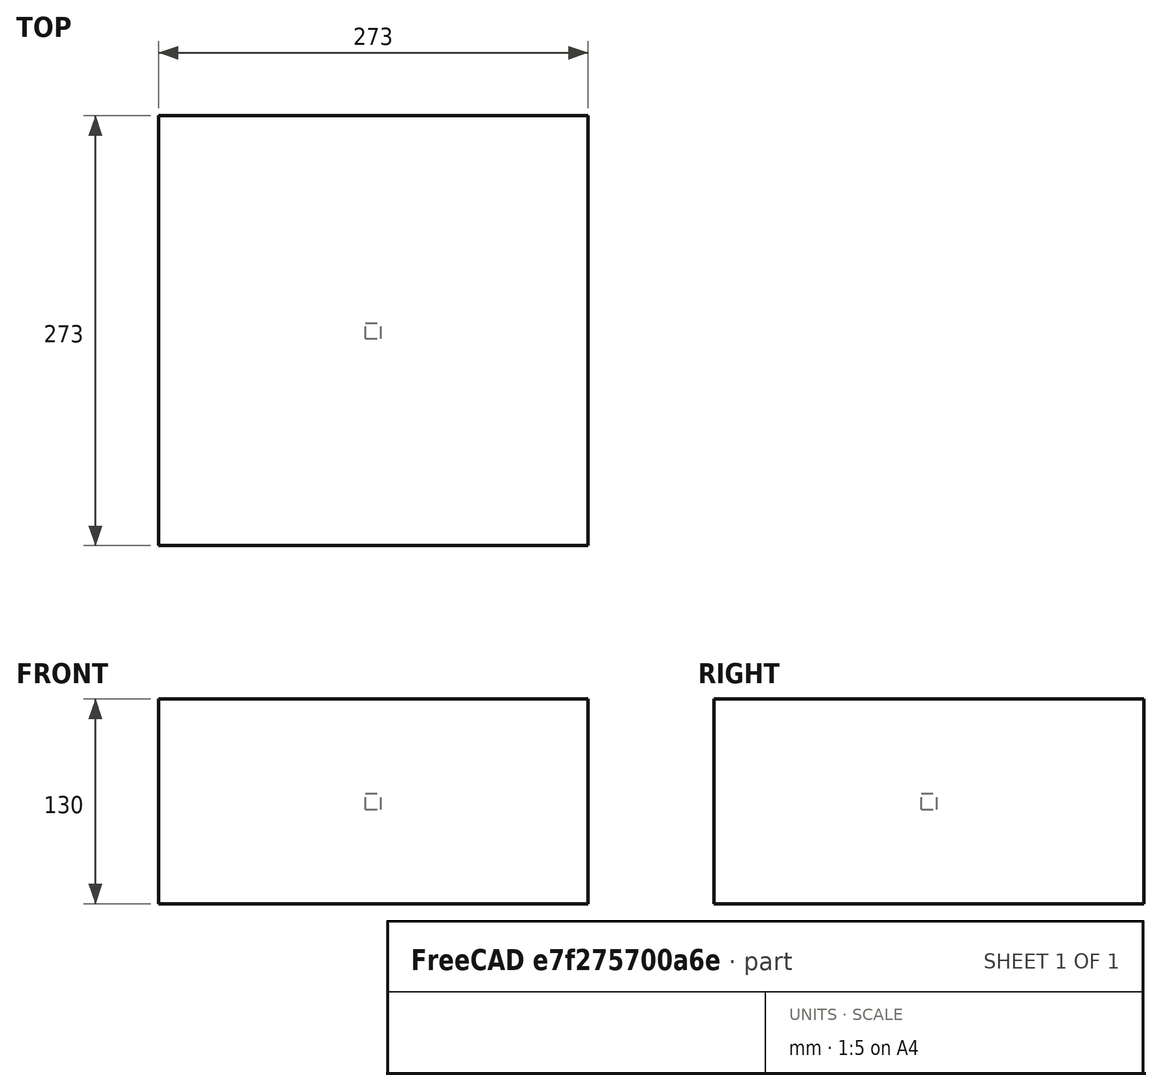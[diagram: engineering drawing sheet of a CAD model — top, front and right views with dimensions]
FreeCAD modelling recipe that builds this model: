
FCSTD DOCUMENT  (FreeCAD 0.20RUnknown)
Label: polarArray-3
License: All rights reserved
LicenseURL: http://en.wikipedia.org/wiki/All_rights_reserved
objects: App::DocumentObjectGroupPython×1251, Part::FeaturePython×3, App::Part×3
note: 2 computed .brp shape members not serialized (recipe doc carries the construction recipe); baked Part::Feature solids carry a one-line shape summary decoded from their .brp

FEATURE [App::DocumentObjectGroupPython] HALFPI  # scripted group (container) (typed FeaturePython)
  name = HALFPI
  value = pi/2.
FEATURE [App::DocumentObjectGroupPython] PI  # scripted group (container) (typed FeaturePython)
  name = PI
  value = 1.*pi
FEATURE [App::DocumentObjectGroupPython] TWOPI  # scripted group (container) (typed FeaturePython)
  name = TWOPI
  value = 2.*pi
FEATURE [App::DocumentObjectGroupPython] Constants  # scripted group (container) (typed FeaturePython)
  Group = -> [HALFPI,PI,TWOPI]
FEATURE [App::DocumentObjectGroupPython] Variables  # scripted group (container) (typed FeaturePython)
FEATURE [App::DocumentObjectGroupPython] Quantities  # scripted group (container) (typed FeaturePython)
FEATURE [App::DocumentObjectGroupPython] Isotopes  # scripted group (container) (typed FeaturePython)
FEATURE [App::DocumentObjectGroupPython] Elements  # scripted group (container) (typed FeaturePython)
FEATURE [App::DocumentObjectGroupPython] Matrix  # scripted group (container) (typed FeaturePython)
FEATURE [App::DocumentObjectGroupPython] Surfaces  # scripted group (container) (typed FeaturePython)
FEATURE [App::DocumentObjectGroupPython] Opticals  # scripted group (container) (typed FeaturePython)
  Group = -> [Matrix,Surfaces]
FEATURE [App::DocumentObjectGroupPython] G4Isotopes  # scripted group (container) (typed FeaturePython)
FEATURE [App::DocumentObjectGroupPython] H_element  # scripted group (container) (typed FeaturePython)
  Z = 1
  atom_value = 1.008
  formula = H
  name = H_element
FEATURE [App::DocumentObjectGroupPython] He_element  # scripted group (container) (typed FeaturePython)
  Z = 2
  atom_value = 4.0026
  formula = He
  name = He_element
FEATURE [App::DocumentObjectGroupPython] Li_element  # scripted group (container) (typed FeaturePython)
  Z = 3
  atom_value = 6.94
  formula = Li
  name = Li_element
FEATURE [App::DocumentObjectGroupPython] Be_element  # scripted group (container) (typed FeaturePython)
  Z = 4
  atom_value = 9.01218
  formula = Be
  name = Be_element
FEATURE [App::DocumentObjectGroupPython] B_element  # scripted group (container) (typed FeaturePython)
  Z = 5
  atom_value = 10.81
  formula = B
  name = B_element
FEATURE [App::DocumentObjectGroupPython] C_element  # scripted group (container) (typed FeaturePython)
  Z = 6
  atom_value = 12.011
  formula = C
  name = C_element
FEATURE [App::DocumentObjectGroupPython] N_element  # scripted group (container) (typed FeaturePython)
  Z = 7
  atom_value = 14.007
  formula = N
  name = N_element
FEATURE [App::DocumentObjectGroupPython] O_element  # scripted group (container) (typed FeaturePython)
  Z = 8
  atom_value = 15.999
  formula = O
  name = O_element
FEATURE [App::DocumentObjectGroupPython] F_element  # scripted group (container) (typed FeaturePython)
  Z = 9
  atom_value = 18.9984
  formula = F
  name = F_element
FEATURE [App::DocumentObjectGroupPython] Ne_element  # scripted group (container) (typed FeaturePython)
  Z = 10
  atom_value = 20.1797
  formula = Ne
  name = Ne_element
FEATURE [App::DocumentObjectGroupPython] Na_element  # scripted group (container) (typed FeaturePython)
  Z = 11
  atom_value = 22.9898
  formula = Na
  name = Na_element
FEATURE [App::DocumentObjectGroupPython] Mg_element  # scripted group (container) (typed FeaturePython)
  Z = 12
  atom_value = 24.305
  formula = Mg
  name = Mg_element
FEATURE [App::DocumentObjectGroupPython] Al_element  # scripted group (container) (typed FeaturePython)
  Z = 13
  atom_value = 26.9815
  formula = Al
  name = Al_element
FEATURE [App::DocumentObjectGroupPython] Si_element  # scripted group (container) (typed FeaturePython)
  Z = 14
  atom_value = 28.085
  formula = Si
  name = Si_element
FEATURE [App::DocumentObjectGroupPython] P_element  # scripted group (container) (typed FeaturePython)
  Z = 15
  atom_value = 30.9738
  formula = P
  name = P_element
FEATURE [App::DocumentObjectGroupPython] S_element  # scripted group (container) (typed FeaturePython)
  Z = 16
  atom_value = 32.06
  formula = S
  name = S_element
FEATURE [App::DocumentObjectGroupPython] Cl_element  # scripted group (container) (typed FeaturePython)
  Z = 17
  atom_value = 35.45
  formula = Cl
  name = Cl_element
FEATURE [App::DocumentObjectGroupPython] Ar_element  # scripted group (container) (typed FeaturePython)
  Z = 18
  atom_value = 39.95
  formula = Ar
  name = Ar_element
FEATURE [App::DocumentObjectGroupPython] K_element  # scripted group (container) (typed FeaturePython)
  Z = 19
  atom_value = 39.0983
  formula = K
  name = K_element
FEATURE [App::DocumentObjectGroupPython] Ca_element  # scripted group (container) (typed FeaturePython)
  Z = 20
  atom_value = 40.078
  formula = Ca
  name = Ca_element
FEATURE [App::DocumentObjectGroupPython] Sc_element  # scripted group (container) (typed FeaturePython)
  Z = 21
  atom_value = 44.9559
  formula = Sc
  name = Sc_element
FEATURE [App::DocumentObjectGroupPython] Ti_element  # scripted group (container) (typed FeaturePython)
  Z = 22
  atom_value = 47.867
  formula = Ti
  name = Ti_element
FEATURE [App::DocumentObjectGroupPython] V_element  # scripted group (container) (typed FeaturePython)
  Z = 23
  atom_value = 50.9415
  formula = V
  name = V_element
FEATURE [App::DocumentObjectGroupPython] Cr_element  # scripted group (container) (typed FeaturePython)
  Z = 24
  atom_value = 51.9961
  formula = Cr
  name = Cr_element
FEATURE [App::DocumentObjectGroupPython] Mn_element  # scripted group (container) (typed FeaturePython)
  Z = 25
  atom_value = 54.938
  formula = Mn
  name = Mn_element
FEATURE [App::DocumentObjectGroupPython] Fe_element  # scripted group (container) (typed FeaturePython)
  Z = 26
  atom_value = 55.845
  formula = Fe
  name = Fe_element
FEATURE [App::DocumentObjectGroupPython] Co_element  # scripted group (container) (typed FeaturePython)
  Z = 27
  atom_value = 58.9332
  formula = Co
  name = Co_element
FEATURE [App::DocumentObjectGroupPython] Ni_element  # scripted group (container) (typed FeaturePython)
  Z = 28
  atom_value = 58.6934
  formula = Ni
  name = Ni_element
FEATURE [App::DocumentObjectGroupPython] Cu_element  # scripted group (container) (typed FeaturePython)
  Z = 29
  atom_value = 63.546
  formula = Cu
  name = Cu_element
FEATURE [App::DocumentObjectGroupPython] Zn_element  # scripted group (container) (typed FeaturePython)
  Z = 30
  atom_value = 65.38
  formula = Zn
  name = Zn_element
FEATURE [App::DocumentObjectGroupPython] Ga_element  # scripted group (container) (typed FeaturePython)
  Z = 31
  atom_value = 69.723
  formula = Ga
  name = Ga_element
FEATURE [App::DocumentObjectGroupPython] Ge_element  # scripted group (container) (typed FeaturePython)
  Z = 32
  atom_value = 72.63
  formula = Ge
  name = Ge_element
FEATURE [App::DocumentObjectGroupPython] As_element  # scripted group (container) (typed FeaturePython)
  Z = 33
  atom_value = 74.9216
  formula = As
  name = As_element
FEATURE [App::DocumentObjectGroupPython] Se_element  # scripted group (container) (typed FeaturePython)
  Z = 34
  atom_value = 78.971
  formula = Se
  name = Se_element
FEATURE [App::DocumentObjectGroupPython] Br_element  # scripted group (container) (typed FeaturePython)
  Z = 35
  atom_value = 79.904
  formula = Br
  name = Br_element
FEATURE [App::DocumentObjectGroupPython] Kr_element  # scripted group (container) (typed FeaturePython)
  Z = 36
  atom_value = 83.798
  formula = Kr
  name = Kr_element
FEATURE [App::DocumentObjectGroupPython] Rb_element  # scripted group (container) (typed FeaturePython)
  Z = 37
  atom_value = 85.4678
  formula = Rb
  name = Rb_element
FEATURE [App::DocumentObjectGroupPython] Sr_element  # scripted group (container) (typed FeaturePython)
  Z = 38
  atom_value = 87.62
  formula = Sr
  name = Sr_element
FEATURE [App::DocumentObjectGroupPython] Y_element  # scripted group (container) (typed FeaturePython)
  Z = 39
  atom_value = 88.9058
  formula = Y
  name = Y_element
FEATURE [App::DocumentObjectGroupPython] Zr_element  # scripted group (container) (typed FeaturePython)
  Z = 40
  atom_value = 91.224
  formula = Zr
  name = Zr_element
FEATURE [App::DocumentObjectGroupPython] Nb_element  # scripted group (container) (typed FeaturePython)
  Z = 41
  atom_value = 92.9064
  formula = Nb
  name = Nb_element
FEATURE [App::DocumentObjectGroupPython] Mo_element  # scripted group (container) (typed FeaturePython)
  Z = 42
  atom_value = 95.95
  formula = Mo
  name = Mo_element
FEATURE [App::DocumentObjectGroupPython] Tc_element  # scripted group (container) (typed FeaturePython)
  Z = 43
  atom_value = 97
  formula = Tc
  name = Tc_element
FEATURE [App::DocumentObjectGroupPython] Ru_element  # scripted group (container) (typed FeaturePython)
  Z = 44
  atom_value = 101.07
  formula = Ru
  name = Ru_element
FEATURE [App::DocumentObjectGroupPython] Rh_element  # scripted group (container) (typed FeaturePython)
  Z = 45
  atom_value = 102.905
  formula = Rh
  name = Rh_element
FEATURE [App::DocumentObjectGroupPython] Pd_element  # scripted group (container) (typed FeaturePython)
  Z = 46
  atom_value = 106.42
  formula = Pd
  name = Pd_element
FEATURE [App::DocumentObjectGroupPython] Ag_element  # scripted group (container) (typed FeaturePython)
  Z = 47
  atom_value = 107.868
  formula = Ag
  name = Ag_element
FEATURE [App::DocumentObjectGroupPython] Cd_element  # scripted group (container) (typed FeaturePython)
  Z = 48
  atom_value = 112.414
  formula = Cd
  name = Cd_element
FEATURE [App::DocumentObjectGroupPython] In_element  # scripted group (container) (typed FeaturePython)
  Z = 49
  atom_value = 114.818
  formula = In
  name = In_element
FEATURE [App::DocumentObjectGroupPython] Sn_element  # scripted group (container) (typed FeaturePython)
  Z = 50
  atom_value = 118.71
  formula = Sn
  name = Sn_element
FEATURE [App::DocumentObjectGroupPython] Sb_element  # scripted group (container) (typed FeaturePython)
  Z = 51
  atom_value = 121.76
  formula = Sb
  name = Sb_element
FEATURE [App::DocumentObjectGroupPython] Te_element  # scripted group (container) (typed FeaturePython)
  Z = 52
  atom_value = 127.6
  formula = Te
  name = Te_element
FEATURE [App::DocumentObjectGroupPython] I_element  # scripted group (container) (typed FeaturePython)
  Z = 53
  atom_value = 126.904
  formula = I
  name = I_element
FEATURE [App::DocumentObjectGroupPython] Xe_element  # scripted group (container) (typed FeaturePython)
  Z = 54
  atom_value = 131.293
  formula = Xe
  name = Xe_element
FEATURE [App::DocumentObjectGroupPython] Cs_element  # scripted group (container) (typed FeaturePython)
  Z = 55
  atom_value = 132.905
  formula = Cs
  name = Cs_element
FEATURE [App::DocumentObjectGroupPython] Ba_element  # scripted group (container) (typed FeaturePython)
  Z = 56
  atom_value = 137.327
  formula = Ba
  name = Ba_element
FEATURE [App::DocumentObjectGroupPython] La_element  # scripted group (container) (typed FeaturePython)
  Z = 57
  atom_value = 138.905
  formula = La
  name = La_element
FEATURE [App::DocumentObjectGroupPython] Ce_element  # scripted group (container) (typed FeaturePython)
  Z = 58
  atom_value = 140.116
  formula = Ce
  name = Ce_element
FEATURE [App::DocumentObjectGroupPython] Pr_element  # scripted group (container) (typed FeaturePython)
  Z = 59
  atom_value = 140.908
  formula = Pr
  name = Pr_element
FEATURE [App::DocumentObjectGroupPython] Nd_element  # scripted group (container) (typed FeaturePython)
  Z = 60
  atom_value = 144.242
  formula = Nd
  name = Nd_element
FEATURE [App::DocumentObjectGroupPython] Pm_element  # scripted group (container) (typed FeaturePython)
  Z = 61
  atom_value = 145
  formula = Pm
  name = Pm_element
FEATURE [App::DocumentObjectGroupPython] Sm_element  # scripted group (container) (typed FeaturePython)
  Z = 62
  atom_value = 150.36
  formula = Sm
  name = Sm_element
FEATURE [App::DocumentObjectGroupPython] Eu_element  # scripted group (container) (typed FeaturePython)
  Z = 63
  atom_value = 151.964
  formula = Eu
  name = Eu_element
FEATURE [App::DocumentObjectGroupPython] Gd_element  # scripted group (container) (typed FeaturePython)
  Z = 64
  atom_value = 157.25
  formula = Gd
  name = Gd_element
FEATURE [App::DocumentObjectGroupPython] Tb_element  # scripted group (container) (typed FeaturePython)
  Z = 65
  atom_value = 158.925
  formula = Tb
  name = Tb_element
FEATURE [App::DocumentObjectGroupPython] Dy_element  # scripted group (container) (typed FeaturePython)
  Z = 66
  atom_value = 162.5
  formula = Dy
  name = Dy_element
FEATURE [App::DocumentObjectGroupPython] Ho_element  # scripted group (container) (typed FeaturePython)
  Z = 67
  atom_value = 164.93
  formula = Ho
  name = Ho_element
FEATURE [App::DocumentObjectGroupPython] Er_element  # scripted group (container) (typed FeaturePython)
  Z = 68
  atom_value = 167.259
  formula = Er
  name = Er_element
FEATURE [App::DocumentObjectGroupPython] Tm_element  # scripted group (container) (typed FeaturePython)
  Z = 69
  atom_value = 168.934
  formula = Tm
  name = Tm_element
FEATURE [App::DocumentObjectGroupPython] Yb_element  # scripted group (container) (typed FeaturePython)
  Z = 70
  atom_value = 173.045
  formula = Yb
  name = Yb_element
FEATURE [App::DocumentObjectGroupPython] Lu_element  # scripted group (container) (typed FeaturePython)
  Z = 71
  atom_value = 174.967
  formula = Lu
  name = Lu_element
FEATURE [App::DocumentObjectGroupPython] Hf_element  # scripted group (container) (typed FeaturePython)
  Z = 72
  atom_value = 178.49
  formula = Hf
  name = Hf_element
FEATURE [App::DocumentObjectGroupPython] Ta_element  # scripted group (container) (typed FeaturePython)
  Z = 73
  atom_value = 180.948
  formula = Ta
  name = Ta_element
FEATURE [App::DocumentObjectGroupPython] W_element  # scripted group (container) (typed FeaturePython)
  Z = 74
  atom_value = 183.84
  formula = W
  name = W_element
FEATURE [App::DocumentObjectGroupPython] Re_element  # scripted group (container) (typed FeaturePython)
  Z = 75
  atom_value = 186.207
  formula = Re
  name = Re_element
FEATURE [App::DocumentObjectGroupPython] Os_element  # scripted group (container) (typed FeaturePython)
  Z = 76
  atom_value = 190.23
  formula = Os
  name = Os_element
FEATURE [App::DocumentObjectGroupPython] Ir_element  # scripted group (container) (typed FeaturePython)
  Z = 77
  atom_value = 192.217
  formula = Ir
  name = Ir_element
FEATURE [App::DocumentObjectGroupPython] Pt_element  # scripted group (container) (typed FeaturePython)
  Z = 78
  atom_value = 195.084
  formula = Pt
  name = Pt_element
FEATURE [App::DocumentObjectGroupPython] Au_element  # scripted group (container) (typed FeaturePython)
  Z = 79
  atom_value = 196.967
  formula = Au
  name = Au_element
FEATURE [App::DocumentObjectGroupPython] Hg_element  # scripted group (container) (typed FeaturePython)
  Z = 80
  atom_value = 200.592
  formula = Hg
  name = Hg_element
FEATURE [App::DocumentObjectGroupPython] Tl_element  # scripted group (container) (typed FeaturePython)
  Z = 81
  atom_value = 204.38
  formula = Tl
  name = Tl_element
FEATURE [App::DocumentObjectGroupPython] Pb_element  # scripted group (container) (typed FeaturePython)
  Z = 82
  atom_value = 207.2
  formula = Pb
  name = Pb_element
FEATURE [App::DocumentObjectGroupPython] Bi_element  # scripted group (container) (typed FeaturePython)
  Z = 83
  atom_value = 208.98
  formula = Bi
  name = Bi_element
FEATURE [App::DocumentObjectGroupPython] Po_element  # scripted group (container) (typed FeaturePython)
  Z = 84
  atom_value = 209
  formula = Po
  name = Po_element
FEATURE [App::DocumentObjectGroupPython] At_element  # scripted group (container) (typed FeaturePython)
  Z = 85
  atom_value = 210
  formula = At
  name = At_element
FEATURE [App::DocumentObjectGroupPython] Rn_element  # scripted group (container) (typed FeaturePython)
  Z = 86
  atom_value = 222
  formula = Rn
  name = Rn_element
FEATURE [App::DocumentObjectGroupPython] Fr_element  # scripted group (container) (typed FeaturePython)
  Z = 87
  atom_value = 223
  formula = Fr
  name = Fr_element
FEATURE [App::DocumentObjectGroupPython] Ra_element  # scripted group (container) (typed FeaturePython)
  Z = 88
  atom_value = 226
  formula = Ra
  name = Ra_element
FEATURE [App::DocumentObjectGroupPython] Ac_element  # scripted group (container) (typed FeaturePython)
  Z = 89
  atom_value = 227
  formula = Ac
  name = Ac_element
FEATURE [App::DocumentObjectGroupPython] Th_element  # scripted group (container) (typed FeaturePython)
  Z = 90
  atom_value = 232.038
  formula = Th
  name = Th_element
FEATURE [App::DocumentObjectGroupPython] Pa_element  # scripted group (container) (typed FeaturePython)
  Z = 91
  atom_value = 231.036
  formula = Pa
  name = Pa_element
FEATURE [App::DocumentObjectGroupPython] U_element  # scripted group (container) (typed FeaturePython)
  Z = 92
  atom_value = 238.029
  formula = U
  name = U_element
FEATURE [App::DocumentObjectGroupPython] Np_element  # scripted group (container) (typed FeaturePython)
  Z = 93
  atom_value = 237
  formula = Np
  name = Np_element
FEATURE [App::DocumentObjectGroupPython] Pu_element  # scripted group (container) (typed FeaturePython)
  Z = 94
  atom_value = 244
  formula = Pu
  name = Pu_element
FEATURE [App::DocumentObjectGroupPython] Am_element  # scripted group (container) (typed FeaturePython)
  Z = 95
  atom_value = 243
  formula = Am
  name = Am_element
FEATURE [App::DocumentObjectGroupPython] Cm_element  # scripted group (container) (typed FeaturePython)
  Z = 96
  atom_value = 247
  formula = Cm
  name = Cm_element
FEATURE [App::DocumentObjectGroupPython] Bk_element  # scripted group (container) (typed FeaturePython)
  Z = 97
  atom_value = 247
  formula = Bk
  name = Bk_element
FEATURE [App::DocumentObjectGroupPython] Cf_element  # scripted group (container) (typed FeaturePython)
  Z = 98
  atom_value = 251
  formula = Cf
  name = Cf_element
FEATURE [App::DocumentObjectGroupPython] G4Elements  # scripted group (container) (typed FeaturePython)
  Group = -> [H_element,He_element,Li_element,Be_element,B_element,C_element,N_element,O_element,F_element,Ne_element,Na_element,Mg_element,Al_element,Si_element,P_element,S_element,Cl_element,Ar_element,K_element,Ca_element,Sc_element,Ti_element,V_element,Cr_element,Mn_element,Fe_element,Co_element,Ni_element,Cu_element,Zn_element,Ga_element,Ge_element,As_element,Se_element,Br_element,Kr_element,Rb_element,+61 more]
FEATURE [App::DocumentObjectGroupPython] H_element001  label="H_element : 0.101"  # scripted group (container) (typed FeaturePython)
  n = 0.101327
FEATURE [App::DocumentObjectGroupPython] C_element001  label="C_element : 0.775"  # scripted group (container) (typed FeaturePython)
  n = 0.7755
FEATURE [App::DocumentObjectGroupPython] N_element001  label="N_element : 0.035"  # scripted group (container) (typed FeaturePython)
  n = 0.035057
FEATURE [App::DocumentObjectGroupPython] O_element001  label="O_element : 0.052"  # scripted group (container) (typed FeaturePython)
  n = 0.0523159
FEATURE [App::DocumentObjectGroupPython] F_element001  label="F_element : 0.017"  # scripted group (container) (typed FeaturePython)
  n = 0.017422
FEATURE [App::DocumentObjectGroupPython] Ca_element001  label="Ca_element : 0.018"  # scripted group (container) (typed FeaturePython)
  n = 0.018378
FEATURE [App::DocumentObjectGroupPython] G4_A_150_TISSUE  label="G4_A-150_TISSUE"  # scripted group (container) (typed FeaturePython)
  Dunit = g/cm3
  Dvalue = 1.127
  Group = -> [H_element001,C_element001,N_element001,O_element001,F_element001,Ca_element001]
  conduct = 2
  density = 1
  expand = 3
  formula = G4_A-150_TISSUE
  name = G4_A-150_TISSUE
  specific = 4
FEATURE [App::DocumentObjectGroupPython] C_element002  label="C_element : 3"  # scripted group (container) (typed FeaturePython)
  n = 3
  ref = C_element
FEATURE [App::DocumentObjectGroupPython] H_element002  label="H_element : 6"  # scripted group (container) (typed FeaturePython)
  n = 6
  ref = H_element
FEATURE [App::DocumentObjectGroupPython] O_element002  label="O_element : 1"  # scripted group (container) (typed FeaturePython)
  n = 1
  ref = O_element
FEATURE [App::DocumentObjectGroupPython] G4_ACETONE  # scripted group (container) (typed FeaturePython)
  Dunit = g/cm3
  Dvalue = 0.7899
  Group = -> [C_element002,H_element002,O_element002]
  conduct = 2
  density = 1
  expand = 3
  formula = G4_ACETONE
  name = G4_ACETONE
  specific = 4
FEATURE [App::DocumentObjectGroupPython] C_element003  label="C_element : 2"  # scripted group (container) (typed FeaturePython)
  n = 2
  ref = C_element
FEATURE [App::DocumentObjectGroupPython] H_element003  label="H_element : 2"  # scripted group (container) (typed FeaturePython)
  n = 2
  ref = H_element
FEATURE [App::DocumentObjectGroupPython] G4_ACETYLENE  # scripted group (container) (typed FeaturePython)
  Dunit = g/cm3
  Dvalue = 0.0010967
  Group = -> [C_element003,H_element003]
  conduct = 2
  density = 1
  expand = 3
  formula = G4_ACETYLENE
  name = G4_ACETYLENE
  specific = 4
FEATURE [App::DocumentObjectGroupPython] C_element004  label="C_element : 5"  # scripted group (container) (typed FeaturePython)
  n = 5
  ref = C_element
FEATURE [App::DocumentObjectGroupPython] H_element004  label="H_element : 5"  # scripted group (container) (typed FeaturePython)
  n = 5
  ref = H_element
FEATURE [App::DocumentObjectGroupPython] N_element002  label="N_element : 5"  # scripted group (container) (typed FeaturePython)
  n = 5
  ref = N_element
FEATURE [App::DocumentObjectGroupPython] G4_ADENINE  # scripted group (container) (typed FeaturePython)
  Dunit = g/cm3
  Dvalue = 1.6
  Group = -> [C_element004,H_element004,N_element002]
  conduct = 2
  density = 1
  expand = 3
  formula = G4_ADENINE
  name = G4_ADENINE
  specific = 4
FEATURE [App::DocumentObjectGroupPython] H_element005  label="H_element : 0.114"  # scripted group (container) (typed FeaturePython)
  n = 0.114
FEATURE [App::DocumentObjectGroupPython] C_element005  label="C_element : 0.598"  # scripted group (container) (typed FeaturePython)
  n = 0.598
FEATURE [App::DocumentObjectGroupPython] N_element003  label="N_element : 0.007"  # scripted group (container) (typed FeaturePython)
  n = 0.007
FEATURE [App::DocumentObjectGroupPython] O_element003  label="O_element : 0.278"  # scripted group (container) (typed FeaturePython)
  n = 0.278
FEATURE [App::DocumentObjectGroupPython] Na_element001  label="Na_element : 0.001"  # scripted group (container) (typed FeaturePython)
  n = 0.001
FEATURE [App::DocumentObjectGroupPython] S_element001  label="S_element : 0.001"  # scripted group (container) (typed FeaturePython)
  n = 0.001
FEATURE [App::DocumentObjectGroupPython] Cl_element001  label="Cl_element : 0.001"  # scripted group (container) (typed FeaturePython)
  n = 0.001
FEATURE [App::DocumentObjectGroupPython] G4_ADIPOSE_TISSUE_ICRP  # scripted group (container) (typed FeaturePython)
  Dunit = g/cm3
  Dvalue = 0.95
  Group = -> [H_element005,C_element005,N_element003,O_element003,Na_element001,S_element001,Cl_element001]
  conduct = 2
  density = 1
  expand = 3
  formula = G4_ADIPOSE_TISSUE_ICRP
  name = G4_ADIPOSE_TISSUE_ICRP
  specific = 4
FEATURE [App::DocumentObjectGroupPython] C_element006  label="C_element : 0.000"  # scripted group (container) (typed FeaturePython)
  n = 0.000124
FEATURE [App::DocumentObjectGroupPython] N_element004  label="N_element : 0.755"  # scripted group (container) (typed FeaturePython)
  n = 0.755268
FEATURE [App::DocumentObjectGroupPython] O_element004  label="O_element : 0.232"  # scripted group (container) (typed FeaturePython)
  n = 0.231781
FEATURE [App::DocumentObjectGroupPython] Ar_element001  label="Ar_element : 0.013"  # scripted group (container) (typed FeaturePython)
  n = 0.012827
FEATURE [App::DocumentObjectGroupPython] G4_AIR  # scripted group (container) (typed FeaturePython)
  Dunit = g/cm3
  Dvalue = 0.00120479
  Group = -> [C_element006,N_element004,O_element004,Ar_element001]
  conduct = 2
  density = 1
  expand = 3
  formula = G4_AIR
  name = G4_AIR
  specific = 4
FEATURE [App::DocumentObjectGroupPython] C_element007  label="C_element : 006"  # scripted group (container) (typed FeaturePython)
  n = 3
  ref = C_element
FEATURE [App::DocumentObjectGroupPython] H_element006  label="H_element : 7"  # scripted group (container) (typed FeaturePython)
  n = 7
  ref = H_element
FEATURE [App::DocumentObjectGroupPython] N_element005  label="N_element : 1"  # scripted group (container) (typed FeaturePython)
  n = 1
  ref = N_element
FEATURE [App::DocumentObjectGroupPython] O_element005  label="O_element : 2"  # scripted group (container) (typed FeaturePython)
  n = 2
  ref = O_element
FEATURE [App::DocumentObjectGroupPython] G4_ALANINE  # scripted group (container) (typed FeaturePython)
  Dunit = g/cm3
  Dvalue = 1.42
  Group = -> [C_element007,H_element006,N_element005,O_element005]
  conduct = 2
  density = 1
  expand = 3
  formula = G4_ALANINE
  name = G4_ALANINE
  specific = 4
FEATURE [App::DocumentObjectGroupPython] Al_element001  label="Al_element : 2"  # scripted group (container) (typed FeaturePython)
  n = 2
  ref = Al_element
FEATURE [App::DocumentObjectGroupPython] O_element006  label="O_element : 3"  # scripted group (container) (typed FeaturePython)
  n = 3
  ref = O_element
FEATURE [App::DocumentObjectGroupPython] G4_ALUMINUM_OXIDE  # scripted group (container) (typed FeaturePython)
  Dunit = g/cm3
  Dvalue = 3.97
  Group = -> [Al_element001,O_element006]
  conduct = 2
  density = 1
  expand = 3
  formula = G4_ALUMINUM_OXIDE
  name = G4_ALUMINUM_OXIDE
  specific = 4
FEATURE [App::DocumentObjectGroupPython] H_element007  label="H_element : 0.106"  # scripted group (container) (typed FeaturePython)
  n = 0.10593
FEATURE [App::DocumentObjectGroupPython] C_element008  label="C_element : 0.789"  # scripted group (container) (typed FeaturePython)
  n = 0.788974
FEATURE [App::DocumentObjectGroupPython] O_element007  label="O_element : 0.105"  # scripted group (container) (typed FeaturePython)
  n = 0.105096
FEATURE [App::DocumentObjectGroupPython] G4_AMBER  # scripted group (container) (typed FeaturePython)
  Dunit = g/cm3
  Dvalue = 1.1
  Group = -> [H_element007,C_element008,O_element007]
  conduct = 2
  density = 1
  expand = 3
  formula = G4_AMBER
  name = G4_AMBER
  specific = 4
FEATURE [App::DocumentObjectGroupPython] N_element006  label="N_element : 006"  # scripted group (container) (typed FeaturePython)
  n = 1
  ref = N_element
FEATURE [App::DocumentObjectGroupPython] H_element008  label="H_element : 3"  # scripted group (container) (typed FeaturePython)
  n = 3
  ref = H_element
FEATURE [App::DocumentObjectGroupPython] G4_AMMONIA  # scripted group (container) (typed FeaturePython)
  Dunit = g/cm3
  Dvalue = 0.000826019
  Group = -> [N_element006,H_element008]
  conduct = 2
  density = 1
  expand = 3
  formula = G4_AMMONIA
  name = G4_AMMONIA
  specific = 4
FEATURE [App::DocumentObjectGroupPython] C_element009  label="C_element : 6"  # scripted group (container) (typed FeaturePython)
  n = 6
  ref = C_element
FEATURE [App::DocumentObjectGroupPython] H_element009  label="H_element : 008"  # scripted group (container) (typed FeaturePython)
  n = 7
  ref = H_element
FEATURE [App::DocumentObjectGroupPython] N_element007  label="N_element : 007"  # scripted group (container) (typed FeaturePython)
  n = 1
  ref = N_element
FEATURE [App::DocumentObjectGroupPython] G4_ANILINE  # scripted group (container) (typed FeaturePython)
  Dunit = g/cm3
  Dvalue = 1.0235
  Group = -> [C_element009,H_element009,N_element007]
  conduct = 2
  density = 1
  expand = 3
  formula = G4_ANILINE
  name = G4_ANILINE
  specific = 4
FEATURE [App::DocumentObjectGroupPython] C_element010  label="C_element : 14"  # scripted group (container) (typed FeaturePython)
  n = 14
  ref = C_element
FEATURE [App::DocumentObjectGroupPython] H_element010  label="H_element : 10"  # scripted group (container) (typed FeaturePython)
  n = 10
  ref = H_element
FEATURE [App::DocumentObjectGroupPython] G4_ANTHRACENE  # scripted group (container) (typed FeaturePython)
  Dunit = g/cm3
  Dvalue = 1.283
  Group = -> [C_element010,H_element010]
  conduct = 2
  density = 1
  expand = 3
  formula = G4_ANTHRACENE
  name = G4_ANTHRACENE
  specific = 4
FEATURE [App::DocumentObjectGroupPython] H_element011  label="H_element : 0.065"  # scripted group (container) (typed FeaturePython)
  n = 0.0654709
FEATURE [App::DocumentObjectGroupPython] C_element011  label="C_element : 0.537"  # scripted group (container) (typed FeaturePython)
  n = 0.536944
FEATURE [App::DocumentObjectGroupPython] N_element008  label="N_element : 0.021"  # scripted group (container) (typed FeaturePython)
  n = 0.0215
FEATURE [App::DocumentObjectGroupPython] O_element008  label="O_element : 0.032"  # scripted group (container) (typed FeaturePython)
  n = 0.032085
FEATURE [App::DocumentObjectGroupPython] F_element002  label="F_element : 0.167"  # scripted group (container) (typed FeaturePython)
  n = 0.167411
FEATURE [App::DocumentObjectGroupPython] Ca_element002  label="Ca_element : 0.177"  # scripted group (container) (typed FeaturePython)
  n = 0.176589
FEATURE [App::DocumentObjectGroupPython] G4_B_100_BONE  label="G4_B-100_BONE"  # scripted group (container) (typed FeaturePython)
  Dunit = g/cm3
  Dvalue = 1.45
  Group = -> [H_element011,C_element011,N_element008,O_element008,F_element002,Ca_element002]
  conduct = 2
  density = 1
  expand = 3
  formula = G4_B-100_BONE
  name = G4_B-100_BONE
  specific = 4
FEATURE [App::DocumentObjectGroupPython] H_element012  label="H_element : 0.057"  # scripted group (container) (typed FeaturePython)
  n = 0.057441
FEATURE [App::DocumentObjectGroupPython] C_element012  label="C_element : 0.790"  # scripted group (container) (typed FeaturePython)
  n = 0.774591
FEATURE [App::DocumentObjectGroupPython] O_element009  label="O_element : 0.168"  # scripted group (container) (typed FeaturePython)
  n = 0.167968
FEATURE [App::DocumentObjectGroupPython] G4_BAKELITE  # scripted group (container) (typed FeaturePython)
  Dunit = g/cm3
  Dvalue = 1.25
  Group = -> [H_element012,C_element012,O_element009]
  conduct = 2
  density = 1
  expand = 3
  formula = G4_BAKELITE
  name = G4_BAKELITE
  specific = 4
FEATURE [App::DocumentObjectGroupPython] Ba_element001  label="Ba_element : 1"  # scripted group (container) (typed FeaturePython)
  n = 1
  ref = Ba_element
FEATURE [App::DocumentObjectGroupPython] F_element003  label="F_element : 2"  # scripted group (container) (typed FeaturePython)
  n = 2
  ref = F_element
FEATURE [App::DocumentObjectGroupPython] G4_BARIUM_FLUORIDE  # scripted group (container) (typed FeaturePython)
  Dunit = g/cm3
  Dvalue = 4.89
  Group = -> [Ba_element001,F_element003]
  conduct = 2
  density = 1
  expand = 3
  formula = G4_BARIUM_FLUORIDE
  name = G4_BARIUM_FLUORIDE
  specific = 4
FEATURE [App::DocumentObjectGroupPython] Ba_element002  label="Ba_element : 002"  # scripted group (container) (typed FeaturePython)
  n = 1
  ref = Ba_element
FEATURE [App::DocumentObjectGroupPython] S_element002  label="S_element : 1"  # scripted group (container) (typed FeaturePython)
  n = 1
  ref = S_element
FEATURE [App::DocumentObjectGroupPython] O_element010  label="O_element : 4"  # scripted group (container) (typed FeaturePython)
  n = 4
  ref = O_element
FEATURE [App::DocumentObjectGroupPython] G4_BARIUM_SULFATE  # scripted group (container) (typed FeaturePython)
  Dunit = g/cm3
  Dvalue = 4.5
  Group = -> [Ba_element002,S_element002,O_element010]
  conduct = 2
  density = 1
  expand = 3
  formula = G4_BARIUM_SULFATE
  name = G4_BARIUM_SULFATE
  specific = 4
FEATURE [App::DocumentObjectGroupPython] C_element013  label="C_element : 007"  # scripted group (container) (typed FeaturePython)
  n = 6
  ref = C_element
FEATURE [App::DocumentObjectGroupPython] H_element013  label="H_element : 009"  # scripted group (container) (typed FeaturePython)
  n = 6
  ref = H_element
FEATURE [App::DocumentObjectGroupPython] G4_BENZENE  # scripted group (container) (typed FeaturePython)
  Dunit = g/cm3
  Dvalue = 0.87865
  Group = -> [C_element013,H_element013]
  conduct = 2
  density = 1
  expand = 3
  formula = G4_BENZENE
  name = G4_BENZENE
  specific = 4
FEATURE [App::DocumentObjectGroupPython] Be_element001  label="Be_element : 1"  # scripted group (container) (typed FeaturePython)
  n = 1
  ref = Be_element
FEATURE [App::DocumentObjectGroupPython] O_element011  label="O_element : 005"  # scripted group (container) (typed FeaturePython)
  n = 1
  ref = O_element
FEATURE [App::DocumentObjectGroupPython] G4_BERYLLIUM_OXIDE  # scripted group (container) (typed FeaturePython)
  Dunit = g/cm3
  Dvalue = 3.01
  Group = -> [Be_element001,O_element011]
  conduct = 2
  density = 1
  expand = 3
  formula = G4_BERYLLIUM_OXIDE
  name = G4_BERYLLIUM_OXIDE
  specific = 4
FEATURE [App::DocumentObjectGroupPython] Bi_element001  label="Bi_element : 4"  # scripted group (container) (typed FeaturePython)
  n = 4
  ref = Bi_element
FEATURE [App::DocumentObjectGroupPython] Ge_element001  label="Ge_element : 3"  # scripted group (container) (typed FeaturePython)
  n = 3
  ref = Ge_element
FEATURE [App::DocumentObjectGroupPython] O_element012  label="O_element : 12"  # scripted group (container) (typed FeaturePython)
  n = 12
  ref = O_element
FEATURE [App::DocumentObjectGroupPython] G4_BGO  # scripted group (container) (typed FeaturePython)
  Dunit = g/cm3
  Dvalue = 7.13
  Group = -> [Bi_element001,Ge_element001,O_element012]
  conduct = 2
  density = 1
  expand = 3
  formula = G4_BGO
  name = G4_BGO
  specific = 4
FEATURE [App::DocumentObjectGroupPython] H_element014  label="H_element : 0.102"  # scripted group (container) (typed FeaturePython)
  n = 0.102
FEATURE [App::DocumentObjectGroupPython] C_element014  label="C_element : 0.110"  # scripted group (container) (typed FeaturePython)
  n = 0.11
FEATURE [App::DocumentObjectGroupPython] N_element009  label="N_element : 0.033"  # scripted group (container) (typed FeaturePython)
  n = 0.033
FEATURE [App::DocumentObjectGroupPython] O_element013  label="O_element : 0.745"  # scripted group (container) (typed FeaturePython)
  n = 0.745
FEATURE [App::DocumentObjectGroupPython] Na_element002  label="Na_element : 0.002"  # scripted group (container) (typed FeaturePython)
  n = 0.001
FEATURE [App::DocumentObjectGroupPython] P_element001  label="P_element : 0.001"  # scripted group (container) (typed FeaturePython)
  n = 0.001
FEATURE [App::DocumentObjectGroupPython] S_element003  label="S_element : 0.002"  # scripted group (container) (typed FeaturePython)
  n = 0.002
FEATURE [App::DocumentObjectGroupPython] Cl_element002  label="Cl_element : 0.003"  # scripted group (container) (typed FeaturePython)
  n = 0.003
FEATURE [App::DocumentObjectGroupPython] K_element001  label="K_element : 0.002"  # scripted group (container) (typed FeaturePython)
  n = 0.002
FEATURE [App::DocumentObjectGroupPython] Fe_element001  label="Fe_element : 0.001"  # scripted group (container) (typed FeaturePython)
  n = 0.001
FEATURE [App::DocumentObjectGroupPython] G4_BLOOD_ICRP  # scripted group (container) (typed FeaturePython)
  Dunit = g/cm3
  Dvalue = 1.06
  Group = -> [H_element014,C_element014,N_element009,O_element013,Na_element002,P_element001,S_element003,Cl_element002,K_element001,Fe_element001]
  conduct = 2
  density = 1
  expand = 3
  formula = G4_BLOOD_ICRP
  name = G4_BLOOD_ICRP
  specific = 4
FEATURE [App::DocumentObjectGroupPython] H_element015  label="H_element : 0.064"  # scripted group (container) (typed FeaturePython)
  n = 0.064
FEATURE [App::DocumentObjectGroupPython] C_element015  label="C_element : 0.278"  # scripted group (container) (typed FeaturePython)
  n = 0.278
FEATURE [App::DocumentObjectGroupPython] N_element010  label="N_element : 0.027"  # scripted group (container) (typed FeaturePython)
  n = 0.027
FEATURE [App::DocumentObjectGroupPython] O_element014  label="O_element : 0.410"  # scripted group (container) (typed FeaturePython)
  n = 0.41
FEATURE [App::DocumentObjectGroupPython] Mg_element001  label="Mg_element : 0.002"  # scripted group (container) (typed FeaturePython)
  n = 0.002
FEATURE [App::DocumentObjectGroupPython] P_element002  label="P_element : 0.070"  # scripted group (container) (typed FeaturePython)
  n = 0.07
FEATURE [App::DocumentObjectGroupPython] S_element004  label="S_element : 0.003"  # scripted group (container) (typed FeaturePython)
  n = 0.002
FEATURE [App::DocumentObjectGroupPython] Ca_element003  label="Ca_element : 0.147"  # scripted group (container) (typed FeaturePython)
  n = 0.147
FEATURE [App::DocumentObjectGroupPython] G4_BONE_COMPACT_ICRU  # scripted group (container) (typed FeaturePython)
  Dunit = g/cm3
  Dvalue = 1.85
  Group = -> [H_element015,C_element015,N_element010,O_element014,Mg_element001,P_element002,S_element004,Ca_element003]
  conduct = 2
  density = 1
  expand = 3
  formula = G4_BONE_COMPACT_ICRU
  name = G4_BONE_COMPACT_ICRU
  specific = 4
FEATURE [App::DocumentObjectGroupPython] H_element016  label="H_element : 0.034"  # scripted group (container) (typed FeaturePython)
  n = 0.034
FEATURE [App::DocumentObjectGroupPython] C_element016  label="C_element : 0.155"  # scripted group (container) (typed FeaturePython)
  n = 0.155
FEATURE [App::DocumentObjectGroupPython] N_element011  label="N_element : 0.042"  # scripted group (container) (typed FeaturePython)
  n = 0.042
FEATURE [App::DocumentObjectGroupPython] O_element015  label="O_element : 0.435"  # scripted group (container) (typed FeaturePython)
  n = 0.435
FEATURE [App::DocumentObjectGroupPython] Na_element003  label="Na_element : 0.003"  # scripted group (container) (typed FeaturePython)
  n = 0.001
FEATURE [App::DocumentObjectGroupPython] Mg_element002  label="Mg_element : 0.003"  # scripted group (container) (typed FeaturePython)
  n = 0.002
FEATURE [App::DocumentObjectGroupPython] P_element003  label="P_element : 0.103"  # scripted group (container) (typed FeaturePython)
  n = 0.103
FEATURE [App::DocumentObjectGroupPython] S_element005  label="S_element : 0.004"  # scripted group (container) (typed FeaturePython)
  n = 0.003
FEATURE [App::DocumentObjectGroupPython] Ca_element004  label="Ca_element : 0.225"  # scripted group (container) (typed FeaturePython)
  n = 0.225
FEATURE [App::DocumentObjectGroupPython] G4_BONE_CORTICAL_ICRP  # scripted group (container) (typed FeaturePython)
  Dunit = g/cm3
  Dvalue = 1.92
  Group = -> [H_element016,C_element016,N_element011,O_element015,Na_element003,Mg_element002,P_element003,S_element005,Ca_element004]
  conduct = 2
  density = 1
  expand = 3
  formula = G4_BONE_CORTICAL_ICRP
  name = G4_BONE_CORTICAL_ICRP
  specific = 4
FEATURE [App::DocumentObjectGroupPython] B_element001  label="B_element : 4"  # scripted group (container) (typed FeaturePython)
  n = 4
  ref = B_element
FEATURE [App::DocumentObjectGroupPython] C_element017  label="C_element : 1"  # scripted group (container) (typed FeaturePython)
  n = 1
  ref = C_element
FEATURE [App::DocumentObjectGroupPython] G4_BORON_CARBIDE  # scripted group (container) (typed FeaturePython)
  Dunit = g/cm3
  Dvalue = 2.52
  Group = -> [B_element001,C_element017]
  conduct = 2
  density = 1
  expand = 3
  formula = G4_BORON_CARBIDE
  name = G4_BORON_CARBIDE
  specific = 4
FEATURE [App::DocumentObjectGroupPython] B_element002  label="B_element : 2"  # scripted group (container) (typed FeaturePython)
  n = 2
  ref = B_element
FEATURE [App::DocumentObjectGroupPython] O_element016  label="O_element : 006"  # scripted group (container) (typed FeaturePython)
  n = 3
  ref = O_element
FEATURE [App::DocumentObjectGroupPython] G4_BORON_OXIDE  # scripted group (container) (typed FeaturePython)
  Dunit = g/cm3
  Dvalue = 1.812
  Group = -> [B_element002,O_element016]
  conduct = 2
  density = 1
  expand = 3
  formula = G4_BORON_OXIDE
  name = G4_BORON_OXIDE
  specific = 4
FEATURE [App::DocumentObjectGroupPython] H_element017  label="H_element : 0.107"  # scripted group (container) (typed FeaturePython)
  n = 0.107
FEATURE [App::DocumentObjectGroupPython] C_element018  label="C_element : 0.145"  # scripted group (container) (typed FeaturePython)
  n = 0.145
FEATURE [App::DocumentObjectGroupPython] N_element012  label="N_element : 0.022"  # scripted group (container) (typed FeaturePython)
  n = 0.022
FEATURE [App::DocumentObjectGroupPython] O_element017  label="O_element : 0.712"  # scripted group (container) (typed FeaturePython)
  n = 0.712
FEATURE [App::DocumentObjectGroupPython] Na_element004  label="Na_element : 0.004"  # scripted group (container) (typed FeaturePython)
  n = 0.002
FEATURE [App::DocumentObjectGroupPython] P_element004  label="P_element : 0.004"  # scripted group (container) (typed FeaturePython)
  n = 0.004
FEATURE [App::DocumentObjectGroupPython] S_element006  label="S_element : 0.005"  # scripted group (container) (typed FeaturePython)
  n = 0.002
FEATURE [App::DocumentObjectGroupPython] Cl_element003  label="Cl_element : 0.004"  # scripted group (container) (typed FeaturePython)
  n = 0.003
FEATURE [App::DocumentObjectGroupPython] K_element002  label="K_element : 0.003"  # scripted group (container) (typed FeaturePython)
  n = 0.003
FEATURE [App::DocumentObjectGroupPython] G4_BRAIN_ICRP  # scripted group (container) (typed FeaturePython)
  Dunit = g/cm3
  Dvalue = 1.04
  Group = -> [H_element017,C_element018,N_element012,O_element017,Na_element004,P_element004,S_element006,Cl_element003,K_element002]
  conduct = 2
  density = 1
  expand = 3
  formula = G4_BRAIN_ICRP
  name = G4_BRAIN_ICRP
  specific = 4
FEATURE [App::DocumentObjectGroupPython] C_element019  label="C_element : 4"  # scripted group (container) (typed FeaturePython)
  n = 4
  ref = C_element
FEATURE [App::DocumentObjectGroupPython] H_element018  label="H_element : 010"  # scripted group (container) (typed FeaturePython)
  n = 10
  ref = H_element
FEATURE [App::DocumentObjectGroupPython] G4_BUTANE  # scripted group (container) (typed FeaturePython)
  Dunit = g/cm3
  Dvalue = 0.00249343
  Group = -> [C_element019,H_element018]
  conduct = 2
  density = 1
  expand = 3
  formula = G4_BUTANE
  name = G4_BUTANE
  specific = 4
FEATURE [App::DocumentObjectGroupPython] C_element020  label="C_element : 008"  # scripted group (container) (typed FeaturePython)
  n = 4
  ref = C_element
FEATURE [App::DocumentObjectGroupPython] H_element019  label="H_element : 011"  # scripted group (container) (typed FeaturePython)
  n = 10
  ref = H_element
FEATURE [App::DocumentObjectGroupPython] O_element018  label="O_element : 007"  # scripted group (container) (typed FeaturePython)
  n = 1
  ref = O_element
FEATURE [App::DocumentObjectGroupPython] G4_N_BUTYL_ALCOHOL  label="G4_N-BUTYL_ALCOHOL"  # scripted group (container) (typed FeaturePython)
  Dunit = g/cm3
  Dvalue = 0.8098
  Group = -> [C_element020,H_element019,O_element018]
  conduct = 2
  density = 1
  expand = 3
  formula = G4_N-BUTYL_ALCOHOL
  name = G4_N-BUTYL_ALCOHOL
  specific = 4
FEATURE [App::DocumentObjectGroupPython] H_element020  label="H_element : 0.025"  # scripted group (container) (typed FeaturePython)
  n = 0.02468
FEATURE [App::DocumentObjectGroupPython] C_element021  label="C_element : 0.502"  # scripted group (container) (typed FeaturePython)
  n = 0.501611
FEATURE [App::DocumentObjectGroupPython] O_element019  label="O_element : 0.005"  # scripted group (container) (typed FeaturePython)
  n = 0.004527
FEATURE [App::DocumentObjectGroupPython] F_element004  label="F_element : 0.465"  # scripted group (container) (typed FeaturePython)
  n = 0.465209
FEATURE [App::DocumentObjectGroupPython] Si_element001  label="Si_element : 0.004"  # scripted group (container) (typed FeaturePython)
  n = 0.003973
FEATURE [App::DocumentObjectGroupPython] G4_C_552  label="G4_C-552"  # scripted group (container) (typed FeaturePython)
  Dunit = g/cm3
  Dvalue = 1.76
  Group = -> [H_element020,C_element021,O_element019,F_element004,Si_element001]
  conduct = 2
  density = 1
  expand = 3
  formula = G4_C-552
  name = G4_C-552
  specific = 4
FEATURE [App::DocumentObjectGroupPython] Cd_element001  label="Cd_element : 1"  # scripted group (container) (typed FeaturePython)
  n = 1
  ref = Cd_element
FEATURE [App::DocumentObjectGroupPython] Te_element001  label="Te_element : 1"  # scripted group (container) (typed FeaturePython)
  n = 1
  ref = Te_element
FEATURE [App::DocumentObjectGroupPython] G4_CADMIUM_TELLURIDE  # scripted group (container) (typed FeaturePython)
  Dunit = g/cm3
  Dvalue = 6.2
  Group = -> [Cd_element001,Te_element001]
  conduct = 2
  density = 1
  expand = 3
  formula = G4_CADMIUM_TELLURIDE
  name = G4_CADMIUM_TELLURIDE
  specific = 4
FEATURE [App::DocumentObjectGroupPython] Cd_element002  label="Cd_element : 002"  # scripted group (container) (typed FeaturePython)
  n = 1
  ref = Cd_element
FEATURE [App::DocumentObjectGroupPython] W_element001  label="W_element : 1"  # scripted group (container) (typed FeaturePython)
  n = 1
  ref = W_element
FEATURE [App::DocumentObjectGroupPython] O_element020  label="O_element : 008"  # scripted group (container) (typed FeaturePython)
  n = 4
  ref = O_element
FEATURE [App::DocumentObjectGroupPython] G4_CADMIUM_TUNGSTATE  # scripted group (container) (typed FeaturePython)
  Dunit = g/cm3
  Dvalue = 7.9
  Group = -> [Cd_element002,W_element001,O_element020]
  conduct = 2
  density = 1
  expand = 3
  formula = G4_CADMIUM_TUNGSTATE
  name = G4_CADMIUM_TUNGSTATE
  specific = 4
FEATURE [App::DocumentObjectGroupPython] Ca_element005  label="Ca_element : 1"  # scripted group (container) (typed FeaturePython)
  n = 1
  ref = Ca_element
FEATURE [App::DocumentObjectGroupPython] C_element022  label="C_element : 009"  # scripted group (container) (typed FeaturePython)
  n = 1
  ref = C_element
FEATURE [App::DocumentObjectGroupPython] O_element021  label="O_element : 009"  # scripted group (container) (typed FeaturePython)
  n = 3
  ref = O_element
FEATURE [App::DocumentObjectGroupPython] G4_CALCIUM_CARBONATE  # scripted group (container) (typed FeaturePython)
  Dunit = g/cm3
  Dvalue = 2.8
  Group = -> [Ca_element005,C_element022,O_element021]
  conduct = 2
  density = 1
  expand = 3
  formula = G4_CALCIUM_CARBONATE
  name = G4_CALCIUM_CARBONATE
  specific = 4
FEATURE [App::DocumentObjectGroupPython] Ca_element006  label="Ca_element : 002"  # scripted group (container) (typed FeaturePython)
  n = 1
  ref = Ca_element
FEATURE [App::DocumentObjectGroupPython] F_element005  label="F_element : 003"  # scripted group (container) (typed FeaturePython)
  n = 2
  ref = F_element
FEATURE [App::DocumentObjectGroupPython] G4_CALCIUM_FLUORIDE  # scripted group (container) (typed FeaturePython)
  Dunit = g/cm3
  Dvalue = 3.18
  Group = -> [Ca_element006,F_element005]
  conduct = 2
  density = 1
  expand = 3
  formula = G4_CALCIUM_FLUORIDE
  name = G4_CALCIUM_FLUORIDE
  specific = 4
FEATURE [App::DocumentObjectGroupPython] Ca_element007  label="Ca_element : 003"  # scripted group (container) (typed FeaturePython)
  n = 1
  ref = Ca_element
FEATURE [App::DocumentObjectGroupPython] O_element022  label="O_element : 010"  # scripted group (container) (typed FeaturePython)
  n = 1
  ref = O_element
FEATURE [App::DocumentObjectGroupPython] G4_CALCIUM_OXIDE  # scripted group (container) (typed FeaturePython)
  Dunit = g/cm3
  Dvalue = 3.3
  Group = -> [Ca_element007,O_element022]
  conduct = 2
  density = 1
  expand = 3
  formula = G4_CALCIUM_OXIDE
  name = G4_CALCIUM_OXIDE
  specific = 4
FEATURE [App::DocumentObjectGroupPython] Ca_element008  label="Ca_element : 004"  # scripted group (container) (typed FeaturePython)
  n = 1
  ref = Ca_element
FEATURE [App::DocumentObjectGroupPython] S_element007  label="S_element : 002"  # scripted group (container) (typed FeaturePython)
  n = 1
  ref = S_element
FEATURE [App::DocumentObjectGroupPython] O_element023  label="O_element : 011"  # scripted group (container) (typed FeaturePython)
  n = 4
  ref = O_element
FEATURE [App::DocumentObjectGroupPython] G4_CALCIUM_SULFATE  # scripted group (container) (typed FeaturePython)
  Dunit = g/cm3
  Dvalue = 2.96
  Group = -> [Ca_element008,S_element007,O_element023]
  conduct = 2
  density = 1
  expand = 3
  formula = G4_CALCIUM_SULFATE
  name = G4_CALCIUM_SULFATE
  specific = 4
FEATURE [App::DocumentObjectGroupPython] Ca_element009  label="Ca_element : 005"  # scripted group (container) (typed FeaturePython)
  n = 1
  ref = Ca_element
FEATURE [App::DocumentObjectGroupPython] W_element002  label="W_element : 002"  # scripted group (container) (typed FeaturePython)
  n = 1
  ref = W_element
FEATURE [App::DocumentObjectGroupPython] O_element024  label="O_element : 012"  # scripted group (container) (typed FeaturePython)
  n = 4
  ref = O_element
FEATURE [App::DocumentObjectGroupPython] G4_CALCIUM_TUNGSTATE  # scripted group (container) (typed FeaturePython)
  Dunit = g/cm3
  Dvalue = 6.062
  Group = -> [Ca_element009,W_element002,O_element024]
  conduct = 2
  density = 1
  expand = 3
  formula = G4_CALCIUM_TUNGSTATE
  name = G4_CALCIUM_TUNGSTATE
  specific = 4
FEATURE [App::DocumentObjectGroupPython] C_element023  label="C_element : 010"  # scripted group (container) (typed FeaturePython)
  n = 1
  ref = C_element
FEATURE [App::DocumentObjectGroupPython] O_element025  label="O_element : 013"  # scripted group (container) (typed FeaturePython)
  n = 2
  ref = O_element
FEATURE [App::DocumentObjectGroupPython] G4_CARBON_DIOXIDE  # scripted group (container) (typed FeaturePython)
  Dunit = g/cm3
  Dvalue = 0.00184212
  Group = -> [C_element023,O_element025]
  conduct = 2
  density = 1
  expand = 3
  formula = G4_CARBON_DIOXIDE
  name = G4_CARBON_DIOXIDE
  specific = 4
FEATURE [App::DocumentObjectGroupPython] C_element024  label="C_element : 011"  # scripted group (container) (typed FeaturePython)
  n = 1
  ref = C_element
FEATURE [App::DocumentObjectGroupPython] Cl_element004  label="Cl_element : 4"  # scripted group (container) (typed FeaturePython)
  n = 4
  ref = Cl_element
FEATURE [App::DocumentObjectGroupPython] G4_CARBON_TETRACHLORIDE  # scripted group (container) (typed FeaturePython)
  Dunit = g/cm3
  Dvalue = 1.594
  Group = -> [C_element024,Cl_element004]
  conduct = 2
  density = 1
  expand = 3
  formula = G4_CARBON_TETRACHLORIDE
  name = G4_CARBON_TETRACHLORIDE
  specific = 4
FEATURE [App::DocumentObjectGroupPython] C_element025  label="C_element : 012"  # scripted group (container) (typed FeaturePython)
  n = 6
  ref = C_element
FEATURE [App::DocumentObjectGroupPython] H_element021  label="H_element : 012"  # scripted group (container) (typed FeaturePython)
  n = 10
  ref = H_element
FEATURE [App::DocumentObjectGroupPython] O_element026  label="O_element : 5"  # scripted group (container) (typed FeaturePython)
  n = 5
  ref = O_element
FEATURE [App::DocumentObjectGroupPython] G4_CELLULOSE_CELLOPHANE  # scripted group (container) (typed FeaturePython)
  Dunit = g/cm3
  Dvalue = 1.42
  Group = -> [C_element025,H_element021,O_element026]
  conduct = 2
  density = 1
  expand = 3
  formula = G4_CELLULOSE_CELLOPHANE
  name = G4_CELLULOSE_CELLOPHANE
  specific = 4
FEATURE [App::DocumentObjectGroupPython] H_element022  label="H_element : 0.067"  # scripted group (container) (typed FeaturePython)
  n = 0.067125
FEATURE [App::DocumentObjectGroupPython] C_element026  label="C_element : 0.545"  # scripted group (container) (typed FeaturePython)
  n = 0.545403
FEATURE [App::DocumentObjectGroupPython] O_element027  label="O_element : 0.387"  # scripted group (container) (typed FeaturePython)
  n = 0.387472
FEATURE [App::DocumentObjectGroupPython] G4_CELLULOSE_BUTYRATE  # scripted group (container) (typed FeaturePython)
  Dunit = g/cm3
  Dvalue = 1.2
  Group = -> [H_element022,C_element026,O_element027]
  conduct = 2
  density = 1
  expand = 3
  formula = G4_CELLULOSE_BUTYRATE
  name = G4_CELLULOSE_BUTYRATE
  specific = 4
FEATURE [App::DocumentObjectGroupPython] H_element023  label="H_element : 0.029"  # scripted group (container) (typed FeaturePython)
  n = 0.029216
FEATURE [App::DocumentObjectGroupPython] C_element027  label="C_element : 0.271"  # scripted group (container) (typed FeaturePython)
  n = 0.271296
FEATURE [App::DocumentObjectGroupPython] N_element013  label="N_element : 0.121"  # scripted group (container) (typed FeaturePython)
  n = 0.121276
FEATURE [App::DocumentObjectGroupPython] O_element028  label="O_element : 0.578"  # scripted group (container) (typed FeaturePython)
  n = 0.578212
FEATURE [App::DocumentObjectGroupPython] G4_CELLULOSE_NITRATE  # scripted group (container) (typed FeaturePython)
  Dunit = g/cm3
  Dvalue = 1.49
  Group = -> [H_element023,C_element027,N_element013,O_element028]
  conduct = 2
  density = 1
  expand = 3
  formula = G4_CELLULOSE_NITRATE
  name = G4_CELLULOSE_NITRATE
  specific = 4
FEATURE [App::DocumentObjectGroupPython] H_element024  label="H_element : 0.108"  # scripted group (container) (typed FeaturePython)
  n = 0.107596
FEATURE [App::DocumentObjectGroupPython] N_element014  label="N_element : 0.001"  # scripted group (container) (typed FeaturePython)
  n = 0.0008
FEATURE [App::DocumentObjectGroupPython] O_element029  label="O_element : 0.875"  # scripted group (container) (typed FeaturePython)
  n = 0.874976
FEATURE [App::DocumentObjectGroupPython] S_element008  label="S_element : 0.015"  # scripted group (container) (typed FeaturePython)
  n = 0.014627
FEATURE [App::DocumentObjectGroupPython] Ce_element001  label="Ce_element : 0.002"  # scripted group (container) (typed FeaturePython)
  n = 0.002001
FEATURE [App::DocumentObjectGroupPython] G4_CERIC_SULFATE  # scripted group (container) (typed FeaturePython)
  Dunit = g/cm3
  Dvalue = 1.03
  Group = -> [H_element024,N_element014,O_element029,S_element008,Ce_element001]
  conduct = 2
  density = 1
  expand = 3
  formula = G4_CERIC_SULFATE
  name = G4_CERIC_SULFATE
  specific = 4
FEATURE [App::DocumentObjectGroupPython] Cs_element001  label="Cs_element : 1"  # scripted group (container) (typed FeaturePython)
  n = 1
  ref = Cs_element
FEATURE [App::DocumentObjectGroupPython] F_element006  label="F_element : 1"  # scripted group (container) (typed FeaturePython)
  n = 1
  ref = F_element
FEATURE [App::DocumentObjectGroupPython] G4_CESIUM_FLUORIDE  # scripted group (container) (typed FeaturePython)
  Dunit = g/cm3
  Dvalue = 4.115
  Group = -> [Cs_element001,F_element006]
  conduct = 2
  density = 1
  expand = 3
  formula = G4_CESIUM_FLUORIDE
  name = G4_CESIUM_FLUORIDE
  specific = 4
FEATURE [App::DocumentObjectGroupPython] Cs_element002  label="Cs_element : 002"  # scripted group (container) (typed FeaturePython)
  n = 1
  ref = Cs_element
FEATURE [App::DocumentObjectGroupPython] I_element001  label="I_element : 1"  # scripted group (container) (typed FeaturePython)
  n = 1
  ref = I_element
FEATURE [App::DocumentObjectGroupPython] G4_CESIUM_IODIDE  # scripted group (container) (typed FeaturePython)
  Dunit = g/cm3
  Dvalue = 4.51
  Group = -> [Cs_element002,I_element001]
  conduct = 2
  density = 1
  expand = 3
  formula = G4_CESIUM_IODIDE
  name = G4_CESIUM_IODIDE
  specific = 4
FEATURE [App::DocumentObjectGroupPython] C_element028  label="C_element : 013"  # scripted group (container) (typed FeaturePython)
  n = 6
  ref = C_element
FEATURE [App::DocumentObjectGroupPython] H_element025  label="H_element : 013"  # scripted group (container) (typed FeaturePython)
  n = 5
  ref = H_element
FEATURE [App::DocumentObjectGroupPython] Cl_element005  label="Cl_element : 1"  # scripted group (container) (typed FeaturePython)
  n = 1
  ref = Cl_element
FEATURE [App::DocumentObjectGroupPython] G4_CHLOROBENZENE  # scripted group (container) (typed FeaturePython)
  Dunit = g/cm3
  Dvalue = 1.1058
  Group = -> [C_element028,H_element025,Cl_element005]
  conduct = 2
  density = 1
  expand = 3
  formula = G4_CHLOROBENZENE
  name = G4_CHLOROBENZENE
  specific = 4
FEATURE [App::DocumentObjectGroupPython] C_element029  label="C_element : 014"  # scripted group (container) (typed FeaturePython)
  n = 1
  ref = C_element
FEATURE [App::DocumentObjectGroupPython] H_element026  label="H_element : 1"  # scripted group (container) (typed FeaturePython)
  n = 1
  ref = H_element
FEATURE [App::DocumentObjectGroupPython] Cl_element006  label="Cl_element : 3"  # scripted group (container) (typed FeaturePython)
  n = 3
  ref = Cl_element
FEATURE [App::DocumentObjectGroupPython] G4_CHLOROFORM  # scripted group (container) (typed FeaturePython)
  Dunit = g/cm3
  Dvalue = 1.4832
  Group = -> [C_element029,H_element026,Cl_element006]
  conduct = 2
  density = 1
  expand = 3
  formula = G4_CHLOROFORM
  name = G4_CHLOROFORM
  specific = 4
FEATURE [App::DocumentObjectGroupPython] H_element027  label="H_element : 0.010"  # scripted group (container) (typed FeaturePython)
  n = 0.01
FEATURE [App::DocumentObjectGroupPython] C_element030  label="C_element : 0.001"  # scripted group (container) (typed FeaturePython)
  n = 0.001
FEATURE [App::DocumentObjectGroupPython] O_element030  label="O_element : 0.529"  # scripted group (container) (typed FeaturePython)
  n = 0.529107
FEATURE [App::DocumentObjectGroupPython] Na_element005  label="Na_element : 0.016"  # scripted group (container) (typed FeaturePython)
  n = 0.016
FEATURE [App::DocumentObjectGroupPython] Mg_element003  label="Mg_element : 0.004"  # scripted group (container) (typed FeaturePython)
  n = 0.002
FEATURE [App::DocumentObjectGroupPython] Al_element002  label="Al_element : 0.034"  # scripted group (container) (typed FeaturePython)
  n = 0.033872
FEATURE [App::DocumentObjectGroupPython] Si_element002  label="Si_element : 0.337"  # scripted group (container) (typed FeaturePython)
  n = 0.337021
FEATURE [App::DocumentObjectGroupPython] K_element003  label="K_element : 0.013"  # scripted group (container) (typed FeaturePython)
  n = 0.013
FEATURE [App::DocumentObjectGroupPython] Ca_element010  label="Ca_element : 0.044"  # scripted group (container) (typed FeaturePython)
  n = 0.044
FEATURE [App::DocumentObjectGroupPython] Fe_element002  label="Fe_element : 0.014"  # scripted group (container) (typed FeaturePython)
  n = 0.014
FEATURE [App::DocumentObjectGroupPython] G4_CONCRETE  # scripted group (container) (typed FeaturePython)
  Dunit = g/cm3
  Dvalue = 2.3
  Group = -> [H_element027,C_element030,O_element030,Na_element005,Mg_element003,Al_element002,Si_element002,K_element003,Ca_element010,Fe_element002]
  conduct = 2
  density = 1
  expand = 3
  formula = G4_CONCRETE
  name = G4_CONCRETE
  specific = 4
FEATURE [App::DocumentObjectGroupPython] C_element031  label="C_element : 015"  # scripted group (container) (typed FeaturePython)
  n = 6
  ref = C_element
FEATURE [App::DocumentObjectGroupPython] H_element028  label="H_element : 12"  # scripted group (container) (typed FeaturePython)
  n = 12
  ref = H_element
FEATURE [App::DocumentObjectGroupPython] G4_CYCLOHEXANE  # scripted group (container) (typed FeaturePython)
  Dunit = g/cm3
  Dvalue = 0.779
  Group = -> [C_element031,H_element028]
  conduct = 2
  density = 1
  expand = 3
  formula = G4_CYCLOHEXANE
  name = G4_CYCLOHEXANE
  specific = 4
FEATURE [App::DocumentObjectGroupPython] C_element032  label="C_element : 016"  # scripted group (container) (typed FeaturePython)
  n = 6
  ref = C_element
FEATURE [App::DocumentObjectGroupPython] H_element029  label="H_element : 4"  # scripted group (container) (typed FeaturePython)
  n = 4
  ref = H_element
FEATURE [App::DocumentObjectGroupPython] Cl_element007  label="Cl_element : 2"  # scripted group (container) (typed FeaturePython)
  n = 2
  ref = Cl_element
FEATURE [App::DocumentObjectGroupPython] G4_1_2_DICHLOROBENZENE  label="G4_1.2-DICHLOROBENZENE"  # scripted group (container) (typed FeaturePython)
  Dunit = g/cm3
  Dvalue = 1.3048
  Group = -> [C_element032,H_element029,Cl_element007]
  conduct = 2
  density = 1
  expand = 3
  formula = G4_1.2-DICHLOROBENZENE
  name = G4_1.2-DICHLOROBENZENE
  specific = 4
FEATURE [App::DocumentObjectGroupPython] C_element033  label="C_element : 017"  # scripted group (container) (typed FeaturePython)
  n = 4
  ref = C_element
FEATURE [App::DocumentObjectGroupPython] H_element030  label="H_element : 8"  # scripted group (container) (typed FeaturePython)
  n = 8
  ref = H_element
FEATURE [App::DocumentObjectGroupPython] O_element031  label="O_element : 014"  # scripted group (container) (typed FeaturePython)
  n = 1
  ref = O_element
FEATURE [App::DocumentObjectGroupPython] Cl_element008  label="Cl_element : 005"  # scripted group (container) (typed FeaturePython)
  n = 2
  ref = Cl_element
FEATURE [App::DocumentObjectGroupPython] G4_DICHLORODIETHYL_ETHER  # scripted group (container) (typed FeaturePython)
  Dunit = g/cm3
  Dvalue = 1.2199
  Group = -> [C_element033,H_element030,O_element031,Cl_element008]
  conduct = 2
  density = 1
  expand = 3
  formula = G4_DICHLORODIETHYL_ETHER
  name = G4_DICHLORODIETHYL_ETHER
  specific = 4
FEATURE [App::DocumentObjectGroupPython] C_element034  label="C_element : 018"  # scripted group (container) (typed FeaturePython)
  n = 2
  ref = C_element
FEATURE [App::DocumentObjectGroupPython] H_element031  label="H_element : 014"  # scripted group (container) (typed FeaturePython)
  n = 4
  ref = H_element
FEATURE [App::DocumentObjectGroupPython] Cl_element009  label="Cl_element : 006"  # scripted group (container) (typed FeaturePython)
  n = 2
  ref = Cl_element
FEATURE [App::DocumentObjectGroupPython] G4_1_2_DICHLOROETHANE  label="G4_1.2-DICHLOROETHANE"  # scripted group (container) (typed FeaturePython)
  Dunit = g/cm3
  Dvalue = 1.2351
  Group = -> [C_element034,H_element031,Cl_element009]
  conduct = 2
  density = 1
  expand = 3
  formula = G4_1.2-DICHLOROETHANE
  name = G4_1.2-DICHLOROETHANE
  specific = 4
FEATURE [App::DocumentObjectGroupPython] C_element035  label="C_element : 019"  # scripted group (container) (typed FeaturePython)
  n = 4
  ref = C_element
FEATURE [App::DocumentObjectGroupPython] H_element032  label="H_element : 015"  # scripted group (container) (typed FeaturePython)
  n = 10
  ref = H_element
FEATURE [App::DocumentObjectGroupPython] O_element032  label="O_element : 015"  # scripted group (container) (typed FeaturePython)
  n = 1
  ref = O_element
FEATURE [App::DocumentObjectGroupPython] G4_DIETHYL_ETHER  # scripted group (container) (typed FeaturePython)
  Dunit = g/cm3
  Dvalue = 0.71378
  Group = -> [C_element035,H_element032,O_element032]
  conduct = 2
  density = 1
  expand = 3
  formula = G4_DIETHYL_ETHER
  name = G4_DIETHYL_ETHER
  specific = 4
FEATURE [App::DocumentObjectGroupPython] C_element036  label="C_element : 020"  # scripted group (container) (typed FeaturePython)
  n = 3
  ref = C_element
FEATURE [App::DocumentObjectGroupPython] H_element033  label="H_element : 016"  # scripted group (container) (typed FeaturePython)
  n = 7
  ref = H_element
FEATURE [App::DocumentObjectGroupPython] N_element015  label="N_element : 008"  # scripted group (container) (typed FeaturePython)
  n = 1
  ref = N_element
FEATURE [App::DocumentObjectGroupPython] O_element033  label="O_element : 016"  # scripted group (container) (typed FeaturePython)
  n = 1
  ref = O_element
FEATURE [App::DocumentObjectGroupPython] G4_N_N_DIMETHYL_FORMAMIDE  label="G4_N.N-DIMETHYL_FORMAMIDE"  # scripted group (container) (typed FeaturePython)
  Dunit = g/cm3
  Dvalue = 0.9487
  Group = -> [C_element036,H_element033,N_element015,O_element033]
  conduct = 2
  density = 1
  expand = 3
  formula = G4_N.N-DIMETHYL_FORMAMIDE
  name = G4_N.N-DIMETHYL_FORMAMIDE
  specific = 4
FEATURE [App::DocumentObjectGroupPython] C_element037  label="C_element : 021"  # scripted group (container) (typed FeaturePython)
  n = 2
  ref = C_element
FEATURE [App::DocumentObjectGroupPython] H_element034  label="H_element : 017"  # scripted group (container) (typed FeaturePython)
  n = 6
  ref = H_element
FEATURE [App::DocumentObjectGroupPython] O_element034  label="O_element : 017"  # scripted group (container) (typed FeaturePython)
  n = 1
  ref = O_element
FEATURE [App::DocumentObjectGroupPython] S_element009  label="S_element : 003"  # scripted group (container) (typed FeaturePython)
  n = 1
  ref = S_element
FEATURE [App::DocumentObjectGroupPython] G4_DIMETHYL_SULFOXIDE  # scripted group (container) (typed FeaturePython)
  Dunit = g/cm3
  Dvalue = 1.1014
  Group = -> [C_element037,H_element034,O_element034,S_element009]
  conduct = 2
  density = 1
  expand = 3
  formula = G4_DIMETHYL_SULFOXIDE
  name = G4_DIMETHYL_SULFOXIDE
  specific = 4
FEATURE [App::DocumentObjectGroupPython] C_element038  label="C_element : 022"  # scripted group (container) (typed FeaturePython)
  n = 2
  ref = C_element
FEATURE [App::DocumentObjectGroupPython] H_element035  label="H_element : 018"  # scripted group (container) (typed FeaturePython)
  n = 6
  ref = H_element
FEATURE [App::DocumentObjectGroupPython] G4_ETHANE  # scripted group (container) (typed FeaturePython)
  Dunit = g/cm3
  Dvalue = 0.00125324
  Group = -> [C_element038,H_element035]
  conduct = 2
  density = 1
  expand = 3
  formula = G4_ETHANE
  name = G4_ETHANE
  specific = 4
FEATURE [App::DocumentObjectGroupPython] C_element039  label="C_element : 023"  # scripted group (container) (typed FeaturePython)
  n = 2
  ref = C_element
FEATURE [App::DocumentObjectGroupPython] H_element036  label="H_element : 019"  # scripted group (container) (typed FeaturePython)
  n = 6
  ref = H_element
FEATURE [App::DocumentObjectGroupPython] O_element035  label="O_element : 018"  # scripted group (container) (typed FeaturePython)
  n = 1
  ref = O_element
FEATURE [App::DocumentObjectGroupPython] G4_ETHYL_ALCOHOL  # scripted group (container) (typed FeaturePython)
  Dunit = g/cm3
  Dvalue = 0.7893
  Group = -> [C_element039,H_element036,O_element035]
  conduct = 2
  density = 1
  expand = 3
  formula = G4_ETHYL_ALCOHOL
  name = G4_ETHYL_ALCOHOL
  specific = 4
FEATURE [App::DocumentObjectGroupPython] H_element037  label="H_element : 0.090"  # scripted group (container) (typed FeaturePython)
  n = 0.090027
FEATURE [App::DocumentObjectGroupPython] C_element040  label="C_element : 0.585"  # scripted group (container) (typed FeaturePython)
  n = 0.585182
FEATURE [App::DocumentObjectGroupPython] O_element036  label="O_element : 0.325"  # scripted group (container) (typed FeaturePython)
  n = 0.324791
FEATURE [App::DocumentObjectGroupPython] G4_ETHYL_CELLULOSE  # scripted group (container) (typed FeaturePython)
  Dunit = g/cm3
  Dvalue = 1.13
  Group = -> [H_element037,C_element040,O_element036]
  conduct = 2
  density = 1
  expand = 3
  formula = G4_ETHYL_CELLULOSE
  name = G4_ETHYL_CELLULOSE
  specific = 4
FEATURE [App::DocumentObjectGroupPython] C_element041  label="C_element : 024"  # scripted group (container) (typed FeaturePython)
  n = 2
  ref = C_element
FEATURE [App::DocumentObjectGroupPython] H_element038  label="H_element : 020"  # scripted group (container) (typed FeaturePython)
  n = 4
  ref = H_element
FEATURE [App::DocumentObjectGroupPython] G4_ETHYLENE  # scripted group (container) (typed FeaturePython)
  Dunit = g/cm3
  Dvalue = 0.00117497
  Group = -> [C_element041,H_element038]
  conduct = 2
  density = 1
  expand = 3
  formula = G4_ETHYLENE
  name = G4_ETHYLENE
  specific = 4
FEATURE [App::DocumentObjectGroupPython] H_element039  label="H_element : 0.096"  # scripted group (container) (typed FeaturePython)
  n = 0.096
FEATURE [App::DocumentObjectGroupPython] C_element042  label="C_element : 0.195"  # scripted group (container) (typed FeaturePython)
  n = 0.195
FEATURE [App::DocumentObjectGroupPython] N_element016  label="N_element : 0.057"  # scripted group (container) (typed FeaturePython)
  n = 0.057
FEATURE [App::DocumentObjectGroupPython] O_element037  label="O_element : 0.646"  # scripted group (container) (typed FeaturePython)
  n = 0.646
FEATURE [App::DocumentObjectGroupPython] Na_element006  label="Na_element : 0.017"  # scripted group (container) (typed FeaturePython)
  n = 0.001
FEATURE [App::DocumentObjectGroupPython] P_element005  label="P_element : 0.104"  # scripted group (container) (typed FeaturePython)
  n = 0.001
FEATURE [App::DocumentObjectGroupPython] S_element010  label="S_element : 0.016"  # scripted group (container) (typed FeaturePython)
  n = 0.003
FEATURE [App::DocumentObjectGroupPython] Cl_element010  label="Cl_element : 0.005"  # scripted group (container) (typed FeaturePython)
  n = 0.001
FEATURE [App::DocumentObjectGroupPython] G4_EYE_LENS_ICRP  # scripted group (container) (typed FeaturePython)
  Dunit = g/cm3
  Dvalue = 1.07
  Group = -> [H_element039,C_element042,N_element016,O_element037,Na_element006,P_element005,S_element010,Cl_element010]
  conduct = 2
  density = 1
  expand = 3
  formula = G4_EYE_LENS_ICRP
  name = G4_EYE_LENS_ICRP
  specific = 4
FEATURE [App::DocumentObjectGroupPython] Fe_element003  label="Fe_element : 2"  # scripted group (container) (typed FeaturePython)
  n = 2
  ref = Fe_element
FEATURE [App::DocumentObjectGroupPython] O_element038  label="O_element : 019"  # scripted group (container) (typed FeaturePython)
  n = 3
  ref = O_element
FEATURE [App::DocumentObjectGroupPython] G4_FERRIC_OXIDE  # scripted group (container) (typed FeaturePython)
  Dunit = g/cm3
  Dvalue = 5.2
  Group = -> [Fe_element003,O_element038]
  conduct = 2
  density = 1
  expand = 3
  formula = G4_FERRIC_OXIDE
  name = G4_FERRIC_OXIDE
  specific = 4
FEATURE [App::DocumentObjectGroupPython] Fe_element004  label="Fe_element : 1"  # scripted group (container) (typed FeaturePython)
  n = 1
  ref = Fe_element
FEATURE [App::DocumentObjectGroupPython] B_element003  label="B_element : 1"  # scripted group (container) (typed FeaturePython)
  n = 1
  ref = B_element
FEATURE [App::DocumentObjectGroupPython] G4_FERROBORIDE  # scripted group (container) (typed FeaturePython)
  Dunit = g/cm3
  Dvalue = 7.15
  Group = -> [Fe_element004,B_element003]
  conduct = 2
  density = 1
  expand = 3
  formula = G4_FERROBORIDE
  name = G4_FERROBORIDE
  specific = 4
FEATURE [App::DocumentObjectGroupPython] Fe_element005  label="Fe_element : 003"  # scripted group (container) (typed FeaturePython)
  n = 1
  ref = Fe_element
FEATURE [App::DocumentObjectGroupPython] O_element039  label="O_element : 020"  # scripted group (container) (typed FeaturePython)
  n = 1
  ref = O_element
FEATURE [App::DocumentObjectGroupPython] G4_FERROUS_OXIDE  # scripted group (container) (typed FeaturePython)
  Dunit = g/cm3
  Dvalue = 5.7
  Group = -> [Fe_element005,O_element039]
  conduct = 2
  density = 1
  expand = 3
  formula = G4_FERROUS_OXIDE
  name = G4_FERROUS_OXIDE
  specific = 4
FEATURE [App::DocumentObjectGroupPython] H_element040  label="H_element : 0.115"  # scripted group (container) (typed FeaturePython)
  n = 0.108259
FEATURE [App::DocumentObjectGroupPython] N_element017  label="N_element : 0.000"  # scripted group (container) (typed FeaturePython)
  n = 2.7e-05
FEATURE [App::DocumentObjectGroupPython] O_element040  label="O_element : 0.879"  # scripted group (container) (typed FeaturePython)
  n = 0.878636
FEATURE [App::DocumentObjectGroupPython] Na_element007  label="Na_element : 0.000"  # scripted group (container) (typed FeaturePython)
  n = 2.2e-05
FEATURE [App::DocumentObjectGroupPython] S_element011  label="S_element : 0.013"  # scripted group (container) (typed FeaturePython)
  n = 0.012968
FEATURE [App::DocumentObjectGroupPython] Cl_element011  label="Cl_element : 0.000"  # scripted group (container) (typed FeaturePython)
  n = 3.4e-05
FEATURE [App::DocumentObjectGroupPython] Fe_element006  label="Fe_element : 0.000"  # scripted group (container) (typed FeaturePython)
  n = 5.4e-05
FEATURE [App::DocumentObjectGroupPython] G4_FERROUS_SULFATE  # scripted group (container) (typed FeaturePython)
  Dunit = g/cm3
  Dvalue = 1.024
  Group = -> [H_element040,N_element017,O_element040,Na_element007,S_element011,Cl_element011,Fe_element006]
  conduct = 2
  density = 1
  expand = 3
  formula = G4_FERROUS_SULFATE
  name = G4_FERROUS_SULFATE
  specific = 4
FEATURE [App::DocumentObjectGroupPython] C_element043  label="C_element : 0.099"  # scripted group (container) (typed FeaturePython)
  n = 0.099335
FEATURE [App::DocumentObjectGroupPython] F_element007  label="F_element : 0.314"  # scripted group (container) (typed FeaturePython)
  n = 0.314247
FEATURE [App::DocumentObjectGroupPython] Cl_element012  label="Cl_element : 0.586"  # scripted group (container) (typed FeaturePython)
  n = 0.586418
FEATURE [App::DocumentObjectGroupPython] G4_FREON_12  label="G4_FREON-12"  # scripted group (container) (typed FeaturePython)
  Dunit = g/cm3
  Dvalue = 1.12
  Group = -> [C_element043,F_element007,Cl_element012]
  conduct = 2
  density = 1
  expand = 3
  formula = G4_FREON-12
  name = G4_FREON-12
  specific = 4
FEATURE [App::DocumentObjectGroupPython] C_element044  label="C_element : 0.057"  # scripted group (container) (typed FeaturePython)
  n = 0.057245
FEATURE [App::DocumentObjectGroupPython] F_element008  label="F_element : 0.181"  # scripted group (container) (typed FeaturePython)
  n = 0.181096
FEATURE [App::DocumentObjectGroupPython] Br_element001  label="Br_element : 0.762"  # scripted group (container) (typed FeaturePython)
  n = 0.761659
FEATURE [App::DocumentObjectGroupPython] G4_FREON_12B2  label="G4_FREON-12B2"  # scripted group (container) (typed FeaturePython)
  Dunit = g/cm3
  Dvalue = 1.8
  Group = -> [C_element044,F_element008,Br_element001]
  conduct = 2
  density = 1
  expand = 3
  formula = G4_FREON-12B2
  name = G4_FREON-12B2
  specific = 4
FEATURE [App::DocumentObjectGroupPython] C_element045  label="C_element : 0.115"  # scripted group (container) (typed FeaturePython)
  n = 0.114983
FEATURE [App::DocumentObjectGroupPython] F_element009  label="F_element : 0.546"  # scripted group (container) (typed FeaturePython)
  n = 0.545621
FEATURE [App::DocumentObjectGroupPython] Cl_element013  label="Cl_element : 0.339"  # scripted group (container) (typed FeaturePython)
  n = 0.339396
FEATURE [App::DocumentObjectGroupPython] G4_FREON_13  label="G4_FREON-13"  # scripted group (container) (typed FeaturePython)
  Dunit = g/cm3
  Dvalue = 0.95
  Group = -> [C_element045,F_element009,Cl_element013]
  conduct = 2
  density = 1
  expand = 3
  formula = G4_FREON-13
  name = G4_FREON-13
  specific = 4
FEATURE [App::DocumentObjectGroupPython] C_element046  label="C_element : 025"  # scripted group (container) (typed FeaturePython)
  n = 1
  ref = C_element
FEATURE [App::DocumentObjectGroupPython] F_element010  label="F_element : 3"  # scripted group (container) (typed FeaturePython)
  n = 3
  ref = F_element
FEATURE [App::DocumentObjectGroupPython] Br_element002  label="Br_element : 1"  # scripted group (container) (typed FeaturePython)
  n = 1
  ref = Br_element
FEATURE [App::DocumentObjectGroupPython] G4_FREON_13B1  label="G4_FREON-13B1"  # scripted group (container) (typed FeaturePython)
  Dunit = g/cm3
  Dvalue = 1.5
  Group = -> [C_element046,F_element010,Br_element002]
  conduct = 2
  density = 1
  expand = 3
  formula = G4_FREON-13B1
  name = G4_FREON-13B1
  specific = 4
FEATURE [App::DocumentObjectGroupPython] C_element047  label="C_element : 0.061"  # scripted group (container) (typed FeaturePython)
  n = 0.061309
FEATURE [App::DocumentObjectGroupPython] F_element011  label="F_element : 0.291"  # scripted group (container) (typed FeaturePython)
  n = 0.290924
FEATURE [App::DocumentObjectGroupPython] I_element002  label="I_element : 0.648"  # scripted group (container) (typed FeaturePython)
  n = 0.647767
FEATURE [App::DocumentObjectGroupPython] G4_FREON_13I1  label="G4_FREON-13I1"  # scripted group (container) (typed FeaturePython)
  Dunit = g/cm3
  Dvalue = 1.8
  Group = -> [C_element047,F_element011,I_element002]
  conduct = 2
  density = 1
  expand = 3
  formula = G4_FREON-13I1
  name = G4_FREON-13I1
  specific = 4
FEATURE [App::DocumentObjectGroupPython] Gd_element001  label="Gd_element : 2"  # scripted group (container) (typed FeaturePython)
  n = 2
  ref = Gd_element
FEATURE [App::DocumentObjectGroupPython] O_element041  label="O_element : 021"  # scripted group (container) (typed FeaturePython)
  n = 2
  ref = O_element
FEATURE [App::DocumentObjectGroupPython] S_element012  label="S_element : 004"  # scripted group (container) (typed FeaturePython)
  n = 1
  ref = S_element
FEATURE [App::DocumentObjectGroupPython] G4_GADOLINIUM_OXYSULFIDE  # scripted group (container) (typed FeaturePython)
  Dunit = g/cm3
  Dvalue = 7.44
  Group = -> [Gd_element001,O_element041,S_element012]
  conduct = 2
  density = 1
  expand = 3
  formula = G4_GADOLINIUM_OXYSULFIDE
  name = G4_GADOLINIUM_OXYSULFIDE
  specific = 4
FEATURE [App::DocumentObjectGroupPython] Ga_element001  label="Ga_element : 1"  # scripted group (container) (typed FeaturePython)
  n = 1
  ref = Ga_element
FEATURE [App::DocumentObjectGroupPython] As_element001  label="As_element : 1"  # scripted group (container) (typed FeaturePython)
  n = 1
  ref = As_element
FEATURE [App::DocumentObjectGroupPython] G4_GALLIUM_ARSENIDE  # scripted group (container) (typed FeaturePython)
  Dunit = g/cm3
  Dvalue = 5.31
  Group = -> [Ga_element001,As_element001]
  conduct = 2
  density = 1
  expand = 3
  formula = G4_GALLIUM_ARSENIDE
  name = G4_GALLIUM_ARSENIDE
  specific = 4
FEATURE [App::DocumentObjectGroupPython] H_element041  label="H_element : 0.081"  # scripted group (container) (typed FeaturePython)
  n = 0.08118
FEATURE [App::DocumentObjectGroupPython] C_element048  label="C_element : 0.416"  # scripted group (container) (typed FeaturePython)
  n = 0.41606
FEATURE [App::DocumentObjectGroupPython] N_element018  label="N_element : 0.111"  # scripted group (container) (typed FeaturePython)
  n = 0.11124
FEATURE [App::DocumentObjectGroupPython] O_element042  label="O_element : 0.381"  # scripted group (container) (typed FeaturePython)
  n = 0.38064
FEATURE [App::DocumentObjectGroupPython] S_element013  label="S_element : 0.011"  # scripted group (container) (typed FeaturePython)
  n = 0.01088
FEATURE [App::DocumentObjectGroupPython] G4_GEL_PHOTO_EMULSION  # scripted group (container) (typed FeaturePython)
  Dunit = g/cm3
  Dvalue = 1.2914
  Group = -> [H_element041,C_element048,N_element018,O_element042,S_element013]
  conduct = 2
  density = 1
  expand = 3
  formula = G4_GEL_PHOTO_EMULSION
  name = G4_GEL_PHOTO_EMULSION
  specific = 4
FEATURE [App::DocumentObjectGroupPython] B_element004  label="B_element : 0.040"  # scripted group (container) (typed FeaturePython)
  n = 0.0400639
FEATURE [App::DocumentObjectGroupPython] O_element043  label="O_element : 0.540"  # scripted group (container) (typed FeaturePython)
  n = 0.539561
FEATURE [App::DocumentObjectGroupPython] Na_element008  label="Na_element : 0.028"  # scripted group (container) (typed FeaturePython)
  n = 0.0281909
FEATURE [App::DocumentObjectGroupPython] Al_element003  label="Al_element : 0.012"  # scripted group (container) (typed FeaturePython)
  n = 0.011644
FEATURE [App::DocumentObjectGroupPython] Si_element003  label="Si_element : 0.377"  # scripted group (container) (typed FeaturePython)
  n = 0.377219
FEATURE [App::DocumentObjectGroupPython] K_element004  label="K_element : 0.014"  # scripted group (container) (typed FeaturePython)
  n = 0.00332099
FEATURE [App::DocumentObjectGroupPython] G4_Pyrex_Glass  # scripted group (container) (typed FeaturePython)
  Dunit = g/cm3
  Dvalue = 2.23
  Group = -> [B_element004,O_element043,Na_element008,Al_element003,Si_element003,K_element004]
  conduct = 2
  density = 1
  expand = 3
  formula = G4_Pyrex_Glass
  name = G4_Pyrex_Glass
  specific = 4
FEATURE [App::DocumentObjectGroupPython] O_element044  label="O_element : 0.156"  # scripted group (container) (typed FeaturePython)
  n = 0.156453
FEATURE [App::DocumentObjectGroupPython] Si_element004  label="Si_element : 0.081"  # scripted group (container) (typed FeaturePython)
  n = 0.080866
FEATURE [App::DocumentObjectGroupPython] Ti_element001  label="Ti_element : 0.008"  # scripted group (container) (typed FeaturePython)
  n = 0.008092
FEATURE [App::DocumentObjectGroupPython] As_element002  label="As_element : 0.003"  # scripted group (container) (typed FeaturePython)
  n = 0.002651
FEATURE [App::DocumentObjectGroupPython] Pb_element001  label="Pb_element : 0.752"  # scripted group (container) (typed FeaturePython)
  n = 0.751938
FEATURE [App::DocumentObjectGroupPython] G4_GLASS_LEAD  # scripted group (container) (typed FeaturePython)
  Dunit = g/cm3
  Dvalue = 6.22
  Group = -> [O_element044,Si_element004,Ti_element001,As_element002,Pb_element001]
  conduct = 2
  density = 1
  expand = 3
  formula = G4_GLASS_LEAD
  name = G4_GLASS_LEAD
  specific = 4
FEATURE [App::DocumentObjectGroupPython] O_element045  label="O_element : 0.460"  # scripted group (container) (typed FeaturePython)
  n = 0.4598
FEATURE [App::DocumentObjectGroupPython] Na_element009  label="Na_element : 0.096"  # scripted group (container) (typed FeaturePython)
  n = 0.0964411
FEATURE [App::DocumentObjectGroupPython] Si_element005  label="Si_element : 0.378"  # scripted group (container) (typed FeaturePython)
  n = 0.336553
FEATURE [App::DocumentObjectGroupPython] Ca_element011  label="Ca_element : 0.107"  # scripted group (container) (typed FeaturePython)
  n = 0.107205
FEATURE [App::DocumentObjectGroupPython] G4_GLASS_PLATE  # scripted group (container) (typed FeaturePython)
  Dunit = g/cm3
  Dvalue = 2.4
  Group = -> [O_element045,Na_element009,Si_element005,Ca_element011]
  conduct = 2
  density = 1
  expand = 3
  formula = G4_GLASS_PLATE
  name = G4_GLASS_PLATE
  specific = 4
FEATURE [App::DocumentObjectGroupPython] C_element049  label="C_element : 026"  # scripted group (container) (typed FeaturePython)
  n = 5
  ref = C_element
FEATURE [App::DocumentObjectGroupPython] H_element042  label="H_element : 021"  # scripted group (container) (typed FeaturePython)
  n = 10
  ref = H_element
FEATURE [App::DocumentObjectGroupPython] N_element019  label="N_element : 2"  # scripted group (container) (typed FeaturePython)
  n = 2
  ref = N_element
FEATURE [App::DocumentObjectGroupPython] O_element046  label="O_element : 022"  # scripted group (container) (typed FeaturePython)
  n = 3
  ref = O_element
FEATURE [App::DocumentObjectGroupPython] G4_GLUTAMINE  # scripted group (container) (typed FeaturePython)
  Dunit = g/cm3
  Dvalue = 1.46
  Group = -> [C_element049,H_element042,N_element019,O_element046]
  conduct = 2
  density = 1
  expand = 3
  formula = G4_GLUTAMINE
  name = G4_GLUTAMINE
  specific = 4
FEATURE [App::DocumentObjectGroupPython] C_element050  label="C_element : 027"  # scripted group (container) (typed FeaturePython)
  n = 3
  ref = C_element
FEATURE [App::DocumentObjectGroupPython] H_element043  label="H_element : 022"  # scripted group (container) (typed FeaturePython)
  n = 8
  ref = H_element
FEATURE [App::DocumentObjectGroupPython] O_element047  label="O_element : 023"  # scripted group (container) (typed FeaturePython)
  n = 3
  ref = O_element
FEATURE [App::DocumentObjectGroupPython] G4_GLYCEROL  # scripted group (container) (typed FeaturePython)
  Dunit = g/cm3
  Dvalue = 1.2613
  Group = -> [C_element050,H_element043,O_element047]
  conduct = 2
  density = 1
  expand = 3
  formula = G4_GLYCEROL
  name = G4_GLYCEROL
  specific = 4
FEATURE [App::DocumentObjectGroupPython] C_element051  label="C_element : 028"  # scripted group (container) (typed FeaturePython)
  n = 5
  ref = C_element
FEATURE [App::DocumentObjectGroupPython] H_element044  label="H_element : 023"  # scripted group (container) (typed FeaturePython)
  n = 5
  ref = H_element
FEATURE [App::DocumentObjectGroupPython] N_element020  label="N_element : 009"  # scripted group (container) (typed FeaturePython)
  n = 5
  ref = N_element
FEATURE [App::DocumentObjectGroupPython] O_element048  label="O_element : 024"  # scripted group (container) (typed FeaturePython)
  n = 1
  ref = O_element
FEATURE [App::DocumentObjectGroupPython] G4_GUANINE  # scripted group (container) (typed FeaturePython)
  Dunit = g/cm3
  Dvalue = 2.2
  Group = -> [C_element051,H_element044,N_element020,O_element048]
  conduct = 2
  density = 1
  expand = 3
  formula = G4_GUANINE
  name = G4_GUANINE
  specific = 4
FEATURE [App::DocumentObjectGroupPython] Ca_element012  label="Ca_element : 006"  # scripted group (container) (typed FeaturePython)
  n = 1
  ref = Ca_element
FEATURE [App::DocumentObjectGroupPython] S_element014  label="S_element : 005"  # scripted group (container) (typed FeaturePython)
  n = 1
  ref = S_element
FEATURE [App::DocumentObjectGroupPython] O_element049  label="O_element : 6"  # scripted group (container) (typed FeaturePython)
  n = 6
  ref = O_element
FEATURE [App::DocumentObjectGroupPython] H_element045  label="H_element : 024"  # scripted group (container) (typed FeaturePython)
  n = 4
  ref = H_element
FEATURE [App::DocumentObjectGroupPython] G4_GYPSUM  # scripted group (container) (typed FeaturePython)
  Dunit = g/cm3
  Dvalue = 2.32
  Group = -> [Ca_element012,S_element014,O_element049,H_element045]
  conduct = 2
  density = 1
  expand = 3
  formula = G4_GYPSUM
  name = G4_GYPSUM
  specific = 4
FEATURE [App::DocumentObjectGroupPython] C_element052  label="C_element : 7"  # scripted group (container) (typed FeaturePython)
  n = 7
  ref = C_element
FEATURE [App::DocumentObjectGroupPython] H_element046  label="H_element : 16"  # scripted group (container) (typed FeaturePython)
  n = 16
  ref = H_element
FEATURE [App::DocumentObjectGroupPython] G4_N_HEPTANE  label="G4_N-HEPTANE"  # scripted group (container) (typed FeaturePython)
  Dunit = g/cm3
  Dvalue = 0.68376
  Group = -> [C_element052,H_element046]
  conduct = 2
  density = 1
  expand = 3
  formula = G4_N-HEPTANE
  name = G4_N-HEPTANE
  specific = 4
FEATURE [App::DocumentObjectGroupPython] C_element053  label="C_element : 029"  # scripted group (container) (typed FeaturePython)
  n = 6
  ref = C_element
FEATURE [App::DocumentObjectGroupPython] H_element047  label="H_element : 14"  # scripted group (container) (typed FeaturePython)
  n = 14
  ref = H_element
FEATURE [App::DocumentObjectGroupPython] G4_N_HEXANE  label="G4_N-HEXANE"  # scripted group (container) (typed FeaturePython)
  Dunit = g/cm3
  Dvalue = 0.6603
  Group = -> [C_element053,H_element047]
  conduct = 2
  density = 1
  expand = 3
  formula = G4_N-HEXANE
  name = G4_N-HEXANE
  specific = 4
FEATURE [App::DocumentObjectGroupPython] C_element054  label="C_element : 22"  # scripted group (container) (typed FeaturePython)
  n = 22
  ref = C_element
FEATURE [App::DocumentObjectGroupPython] H_element048  label="H_element : 025"  # scripted group (container) (typed FeaturePython)
  n = 10
  ref = H_element
FEATURE [App::DocumentObjectGroupPython] N_element021  label="N_element : 010"  # scripted group (container) (typed FeaturePython)
  n = 2
  ref = N_element
FEATURE [App::DocumentObjectGroupPython] O_element050  label="O_element : 025"  # scripted group (container) (typed FeaturePython)
  n = 5
  ref = O_element
FEATURE [App::DocumentObjectGroupPython] G4_KAPTON  # scripted group (container) (typed FeaturePython)
  Dunit = g/cm3
  Dvalue = 1.42
  Group = -> [C_element054,H_element048,N_element021,O_element050]
  conduct = 2
  density = 1
  expand = 3
  formula = G4_KAPTON
  name = G4_KAPTON
  specific = 4
FEATURE [App::DocumentObjectGroupPython] La_element001  label="La_element : 1"  # scripted group (container) (typed FeaturePython)
  n = 1
  ref = La_element
FEATURE [App::DocumentObjectGroupPython] Br_element003  label="Br_element : 002"  # scripted group (container) (typed FeaturePython)
  n = 1
  ref = Br_element
FEATURE [App::DocumentObjectGroupPython] O_element051  label="O_element : 026"  # scripted group (container) (typed FeaturePython)
  n = 1
  ref = O_element
FEATURE [App::DocumentObjectGroupPython] G4_LANTHANUM_OXYBROMIDE  # scripted group (container) (typed FeaturePython)
  Dunit = g/cm3
  Dvalue = 6.28
  Group = -> [La_element001,Br_element003,O_element051]
  conduct = 2
  density = 1
  expand = 3
  formula = G4_LANTHANUM_OXYBROMIDE
  name = G4_LANTHANUM_OXYBROMIDE
  specific = 4
FEATURE [App::DocumentObjectGroupPython] La_element002  label="La_element : 2"  # scripted group (container) (typed FeaturePython)
  n = 2
  ref = La_element
FEATURE [App::DocumentObjectGroupPython] O_element052  label="O_element : 027"  # scripted group (container) (typed FeaturePython)
  n = 2
  ref = O_element
FEATURE [App::DocumentObjectGroupPython] S_element015  label="S_element : 006"  # scripted group (container) (typed FeaturePython)
  n = 1
  ref = S_element
FEATURE [App::DocumentObjectGroupPython] G4_LANTHANUM_OXYSULFIDE  # scripted group (container) (typed FeaturePython)
  Dunit = g/cm3
  Dvalue = 5.86
  Group = -> [La_element002,O_element052,S_element015]
  conduct = 2
  density = 1
  expand = 3
  formula = G4_LANTHANUM_OXYSULFIDE
  name = G4_LANTHANUM_OXYSULFIDE
  specific = 4
FEATURE [App::DocumentObjectGroupPython] O_element053  label="O_element : 0.072"  # scripted group (container) (typed FeaturePython)
  n = 0.071682
FEATURE [App::DocumentObjectGroupPython] Pb_element002  label="Pb_element : 0.928"  # scripted group (container) (typed FeaturePython)
  n = 0.928318
FEATURE [App::DocumentObjectGroupPython] G4_LEAD_OXIDE  # scripted group (container) (typed FeaturePython)
  Dunit = g/cm3
  Dvalue = 9.53
  Group = -> [O_element053,Pb_element002]
  conduct = 2
  density = 1
  expand = 3
  formula = G4_LEAD_OXIDE
  name = G4_LEAD_OXIDE
  specific = 4
FEATURE [App::DocumentObjectGroupPython] Li_element001  label="Li_element : 1"  # scripted group (container) (typed FeaturePython)
  n = 1
  ref = Li_element
FEATURE [App::DocumentObjectGroupPython] N_element022  label="N_element : 011"  # scripted group (container) (typed FeaturePython)
  n = 1
  ref = N_element
FEATURE [App::DocumentObjectGroupPython] H_element049  label="H_element : 026"  # scripted group (container) (typed FeaturePython)
  n = 2
  ref = H_element
FEATURE [App::DocumentObjectGroupPython] G4_LITHIUM_AMIDE  # scripted group (container) (typed FeaturePython)
  Dunit = g/cm3
  Dvalue = 1.178
  Group = -> [Li_element001,N_element022,H_element049]
  conduct = 2
  density = 1
  expand = 3
  formula = G4_LITHIUM_AMIDE
  name = G4_LITHIUM_AMIDE
  specific = 4
FEATURE [App::DocumentObjectGroupPython] Li_element002  label="Li_element : 2"  # scripted group (container) (typed FeaturePython)
  n = 2
  ref = Li_element
FEATURE [App::DocumentObjectGroupPython] C_element055  label="C_element : 030"  # scripted group (container) (typed FeaturePython)
  n = 1
  ref = C_element
FEATURE [App::DocumentObjectGroupPython] O_element054  label="O_element : 028"  # scripted group (container) (typed FeaturePython)
  n = 3
  ref = O_element
FEATURE [App::DocumentObjectGroupPython] G4_LITHIUM_CARBONATE  # scripted group (container) (typed FeaturePython)
  Dunit = g/cm3
  Dvalue = 2.11
  Group = -> [Li_element002,C_element055,O_element054]
  conduct = 2
  density = 1
  expand = 3
  formula = G4_LITHIUM_CARBONATE
  name = G4_LITHIUM_CARBONATE
  specific = 4
FEATURE [App::DocumentObjectGroupPython] Li_element003  label="Li_element : 003"  # scripted group (container) (typed FeaturePython)
  n = 1
  ref = Li_element
FEATURE [App::DocumentObjectGroupPython] F_element012  label="F_element : 004"  # scripted group (container) (typed FeaturePython)
  n = 1
  ref = F_element
FEATURE [App::DocumentObjectGroupPython] G4_LITHIUM_FLUORIDE  # scripted group (container) (typed FeaturePython)
  Dunit = g/cm3
  Dvalue = 2.635
  Group = -> [Li_element003,F_element012]
  conduct = 2
  density = 1
  expand = 3
  formula = G4_LITHIUM_FLUORIDE
  name = G4_LITHIUM_FLUORIDE
  specific = 4
FEATURE [App::DocumentObjectGroupPython] Li_element004  label="Li_element : 004"  # scripted group (container) (typed FeaturePython)
  n = 1
  ref = Li_element
FEATURE [App::DocumentObjectGroupPython] H_element050  label="H_element : 027"  # scripted group (container) (typed FeaturePython)
  n = 1
  ref = H_element
FEATURE [App::DocumentObjectGroupPython] G4_LITHIUM_HYDRIDE  # scripted group (container) (typed FeaturePython)
  Dunit = g/cm3
  Dvalue = 0.82
  Group = -> [Li_element004,H_element050]
  conduct = 2
  density = 1
  expand = 3
  formula = G4_LITHIUM_HYDRIDE
  name = G4_LITHIUM_HYDRIDE
  specific = 4
FEATURE [App::DocumentObjectGroupPython] Li_element005  label="Li_element : 005"  # scripted group (container) (typed FeaturePython)
  n = 1
  ref = Li_element
FEATURE [App::DocumentObjectGroupPython] I_element003  label="I_element : 002"  # scripted group (container) (typed FeaturePython)
  n = 1
  ref = I_element
FEATURE [App::DocumentObjectGroupPython] G4_LITHIUM_IODIDE  # scripted group (container) (typed FeaturePython)
  Dunit = g/cm3
  Dvalue = 3.494
  Group = -> [Li_element005,I_element003]
  conduct = 2
  density = 1
  expand = 3
  formula = G4_LITHIUM_IODIDE
  name = G4_LITHIUM_IODIDE
  specific = 4
FEATURE [App::DocumentObjectGroupPython] Li_element006  label="Li_element : 006"  # scripted group (container) (typed FeaturePython)
  n = 2
  ref = Li_element
FEATURE [App::DocumentObjectGroupPython] O_element055  label="O_element : 029"  # scripted group (container) (typed FeaturePython)
  n = 1
  ref = O_element
FEATURE [App::DocumentObjectGroupPython] G4_LITHIUM_OXIDE  # scripted group (container) (typed FeaturePython)
  Dunit = g/cm3
  Dvalue = 2.013
  Group = -> [Li_element006,O_element055]
  conduct = 2
  density = 1
  expand = 3
  formula = G4_LITHIUM_OXIDE
  name = G4_LITHIUM_OXIDE
  specific = 4
FEATURE [App::DocumentObjectGroupPython] Li_element007  label="Li_element : 007"  # scripted group (container) (typed FeaturePython)
  n = 2
  ref = Li_element
FEATURE [App::DocumentObjectGroupPython] B_element005  label="B_element : 005"  # scripted group (container) (typed FeaturePython)
  n = 4
  ref = B_element
FEATURE [App::DocumentObjectGroupPython] O_element056  label="O_element : 7"  # scripted group (container) (typed FeaturePython)
  n = 7
  ref = O_element
FEATURE [App::DocumentObjectGroupPython] G4_LITHIUM_TETRABORATE  # scripted group (container) (typed FeaturePython)
  Dunit = g/cm3
  Dvalue = 2.44
  Group = -> [Li_element007,B_element005,O_element056]
  conduct = 2
  density = 1
  expand = 3
  formula = G4_LITHIUM_TETRABORATE
  name = G4_LITHIUM_TETRABORATE
  specific = 4
FEATURE [App::DocumentObjectGroupPython] H_element051  label="H_element : 0.105"  # scripted group (container) (typed FeaturePython)
  n = 0.105
FEATURE [App::DocumentObjectGroupPython] C_element056  label="C_element : 0.083"  # scripted group (container) (typed FeaturePython)
  n = 0.083
FEATURE [App::DocumentObjectGroupPython] N_element023  label="N_element : 0.023"  # scripted group (container) (typed FeaturePython)
  n = 0.023
FEATURE [App::DocumentObjectGroupPython] O_element057  label="O_element : 0.779"  # scripted group (container) (typed FeaturePython)
  n = 0.779
FEATURE [App::DocumentObjectGroupPython] Na_element010  label="Na_element : 0.097"  # scripted group (container) (typed FeaturePython)
  n = 0.002
FEATURE [App::DocumentObjectGroupPython] P_element006  label="P_element : 0.105"  # scripted group (container) (typed FeaturePython)
  n = 0.001
FEATURE [App::DocumentObjectGroupPython] S_element016  label="S_element : 0.017"  # scripted group (container) (typed FeaturePython)
  n = 0.002
FEATURE [App::DocumentObjectGroupPython] Cl_element014  label="Cl_element : 0.587"  # scripted group (container) (typed FeaturePython)
  n = 0.003
FEATURE [App::DocumentObjectGroupPython] K_element005  label="K_element : 0.015"  # scripted group (container) (typed FeaturePython)
  n = 0.002
FEATURE [App::DocumentObjectGroupPython] G4_LUNG_ICRP  # scripted group (container) (typed FeaturePython)
  Dunit = g/cm3
  Dvalue = 1.04
  Group = -> [H_element051,C_element056,N_element023,O_element057,Na_element010,P_element006,S_element016,Cl_element014,K_element005]
  conduct = 2
  density = 1
  expand = 3
  formula = G4_LUNG_ICRP
  name = G4_LUNG_ICRP
  specific = 4
FEATURE [App::DocumentObjectGroupPython] H_element052  label="H_element : 0.116"  # scripted group (container) (typed FeaturePython)
  n = 0.114318
FEATURE [App::DocumentObjectGroupPython] C_element057  label="C_element : 0.656"  # scripted group (container) (typed FeaturePython)
  n = 0.655824
FEATURE [App::DocumentObjectGroupPython] O_element058  label="O_element : 0.092"  # scripted group (container) (typed FeaturePython)
  n = 0.0921831
FEATURE [App::DocumentObjectGroupPython] Mg_element004  label="Mg_element : 0.135"  # scripted group (container) (typed FeaturePython)
  n = 0.134792
FEATURE [App::DocumentObjectGroupPython] Ca_element013  label="Ca_element : 0.003"  # scripted group (container) (typed FeaturePython)
  n = 0.002883
FEATURE [App::DocumentObjectGroupPython] G4_M3_WAX  # scripted group (container) (typed FeaturePython)
  Dunit = g/cm3
  Dvalue = 1.05
  Group = -> [H_element052,C_element057,O_element058,Mg_element004,Ca_element013]
  conduct = 2
  density = 1
  expand = 3
  formula = G4_M3_WAX
  name = G4_M3_WAX
  specific = 4
FEATURE [App::DocumentObjectGroupPython] Mg_element005  label="Mg_element : 1"  # scripted group (container) (typed FeaturePython)
  n = 1
  ref = Mg_element
FEATURE [App::DocumentObjectGroupPython] C_element058  label="C_element : 031"  # scripted group (container) (typed FeaturePython)
  n = 1
  ref = C_element
FEATURE [App::DocumentObjectGroupPython] O_element059  label="O_element : 030"  # scripted group (container) (typed FeaturePython)
  n = 3
  ref = O_element
FEATURE [App::DocumentObjectGroupPython] G4_MAGNESIUM_CARBONATE  # scripted group (container) (typed FeaturePython)
  Dunit = g/cm3
  Dvalue = 2.958
  Group = -> [Mg_element005,C_element058,O_element059]
  conduct = 2
  density = 1
  expand = 3
  formula = G4_MAGNESIUM_CARBONATE
  name = G4_MAGNESIUM_CARBONATE
  specific = 4
FEATURE [App::DocumentObjectGroupPython] Mg_element006  label="Mg_element : 002"  # scripted group (container) (typed FeaturePython)
  n = 1
  ref = Mg_element
FEATURE [App::DocumentObjectGroupPython] F_element013  label="F_element : 005"  # scripted group (container) (typed FeaturePython)
  n = 2
  ref = F_element
FEATURE [App::DocumentObjectGroupPython] G4_MAGNESIUM_FLUORIDE  # scripted group (container) (typed FeaturePython)
  Dunit = g/cm3
  Dvalue = 3
  Group = -> [Mg_element006,F_element013]
  conduct = 2
  density = 1
  expand = 3
  formula = G4_MAGNESIUM_FLUORIDE
  name = G4_MAGNESIUM_FLUORIDE
  specific = 4
FEATURE [App::DocumentObjectGroupPython] Mg_element007  label="Mg_element : 003"  # scripted group (container) (typed FeaturePython)
  n = 1
  ref = Mg_element
FEATURE [App::DocumentObjectGroupPython] O_element060  label="O_element : 031"  # scripted group (container) (typed FeaturePython)
  n = 1
  ref = O_element
FEATURE [App::DocumentObjectGroupPython] G4_MAGNESIUM_OXIDE  # scripted group (container) (typed FeaturePython)
  Dunit = g/cm3
  Dvalue = 3.58
  Group = -> [Mg_element007,O_element060]
  conduct = 2
  density = 1
  expand = 3
  formula = G4_MAGNESIUM_OXIDE
  name = G4_MAGNESIUM_OXIDE
  specific = 4
FEATURE [App::DocumentObjectGroupPython] Mg_element008  label="Mg_element : 004"  # scripted group (container) (typed FeaturePython)
  n = 1
  ref = Mg_element
FEATURE [App::DocumentObjectGroupPython] B_element006  label="B_element : 006"  # scripted group (container) (typed FeaturePython)
  n = 4
  ref = B_element
FEATURE [App::DocumentObjectGroupPython] O_element061  label="O_element : 032"  # scripted group (container) (typed FeaturePython)
  n = 7
  ref = O_element
FEATURE [App::DocumentObjectGroupPython] G4_MAGNESIUM_TETRABORATE  # scripted group (container) (typed FeaturePython)
  Dunit = g/cm3
  Dvalue = 2.53
  Group = -> [Mg_element008,B_element006,O_element061]
  conduct = 2
  density = 1
  expand = 3
  formula = G4_MAGNESIUM_TETRABORATE
  name = G4_MAGNESIUM_TETRABORATE
  specific = 4
FEATURE [App::DocumentObjectGroupPython] Hg_element001  label="Hg_element : 1"  # scripted group (container) (typed FeaturePython)
  n = 1
  ref = Hg_element
FEATURE [App::DocumentObjectGroupPython] I_element004  label="I_element : 2"  # scripted group (container) (typed FeaturePython)
  n = 2
  ref = I_element
FEATURE [App::DocumentObjectGroupPython] G4_MERCURIC_IODIDE  # scripted group (container) (typed FeaturePython)
  Dunit = g/cm3
  Dvalue = 6.36
  Group = -> [Hg_element001,I_element004]
  conduct = 2
  density = 1
  expand = 3
  formula = G4_MERCURIC_IODIDE
  name = G4_MERCURIC_IODIDE
  specific = 4
FEATURE [App::DocumentObjectGroupPython] C_element059  label="C_element : 032"  # scripted group (container) (typed FeaturePython)
  n = 1
  ref = C_element
FEATURE [App::DocumentObjectGroupPython] H_element053  label="H_element : 028"  # scripted group (container) (typed FeaturePython)
  n = 4
  ref = H_element
FEATURE [App::DocumentObjectGroupPython] G4_METHANE  # scripted group (container) (typed FeaturePython)
  Dunit = g/cm3
  Dvalue = 0.000667151
  Group = -> [C_element059,H_element053]
  conduct = 2
  density = 1
  expand = 3
  formula = G4_METHANE
  name = G4_METHANE
  specific = 4
FEATURE [App::DocumentObjectGroupPython] C_element060  label="C_element : 033"  # scripted group (container) (typed FeaturePython)
  n = 1
  ref = C_element
FEATURE [App::DocumentObjectGroupPython] H_element054  label="H_element : 029"  # scripted group (container) (typed FeaturePython)
  n = 4
  ref = H_element
FEATURE [App::DocumentObjectGroupPython] O_element062  label="O_element : 033"  # scripted group (container) (typed FeaturePython)
  n = 1
  ref = O_element
FEATURE [App::DocumentObjectGroupPython] G4_METHANOL  # scripted group (container) (typed FeaturePython)
  Dunit = g/cm3
  Dvalue = 0.7914
  Group = -> [C_element060,H_element054,O_element062]
  conduct = 2
  density = 1
  expand = 3
  formula = G4_METHANOL
  name = G4_METHANOL
  specific = 4
FEATURE [App::DocumentObjectGroupPython] H_element055  label="H_element : 0.134"  # scripted group (container) (typed FeaturePython)
  n = 0.13404
FEATURE [App::DocumentObjectGroupPython] C_element061  label="C_element : 0.778"  # scripted group (container) (typed FeaturePython)
  n = 0.77796
FEATURE [App::DocumentObjectGroupPython] O_element063  label="O_element : 0.035"  # scripted group (container) (typed FeaturePython)
  n = 0.03502
FEATURE [App::DocumentObjectGroupPython] Mg_element009  label="Mg_element : 0.039"  # scripted group (container) (typed FeaturePython)
  n = 0.038594
FEATURE [App::DocumentObjectGroupPython] Ti_element002  label="Ti_element : 0.014"  # scripted group (container) (typed FeaturePython)
  n = 0.014386
FEATURE [App::DocumentObjectGroupPython] G4_MIX_D_WAX  # scripted group (container) (typed FeaturePython)
  Dunit = g/cm3
  Dvalue = 0.99
  Group = -> [H_element055,C_element061,O_element063,Mg_element009,Ti_element002]
  conduct = 2
  density = 1
  expand = 3
  formula = G4_MIX_D_WAX
  name = G4_MIX_D_WAX
  specific = 4
FEATURE [App::DocumentObjectGroupPython] H_element056  label="H_element : 0.135"  # scripted group (container) (typed FeaturePython)
  n = 0.081192
FEATURE [App::DocumentObjectGroupPython] C_element062  label="C_element : 0.583"  # scripted group (container) (typed FeaturePython)
  n = 0.583442
FEATURE [App::DocumentObjectGroupPython] N_element024  label="N_element : 0.018"  # scripted group (container) (typed FeaturePython)
  n = 0.017798
FEATURE [App::DocumentObjectGroupPython] O_element064  label="O_element : 0.186"  # scripted group (container) (typed FeaturePython)
  n = 0.186381
FEATURE [App::DocumentObjectGroupPython] Mg_element010  label="Mg_element : 0.130"  # scripted group (container) (typed FeaturePython)
  n = 0.130287
FEATURE [App::DocumentObjectGroupPython] Cl_element015  label="Cl_element : 0.588"  # scripted group (container) (typed FeaturePython)
  n = 0.0009
FEATURE [App::DocumentObjectGroupPython] G4_MS20_TISSUE  # scripted group (container) (typed FeaturePython)
  Dunit = g/cm3
  Dvalue = 1
  Group = -> [H_element056,C_element062,N_element024,O_element064,Mg_element010,Cl_element015]
  conduct = 2
  density = 1
  expand = 3
  formula = G4_MS20_TISSUE
  name = G4_MS20_TISSUE
  specific = 4
FEATURE [App::DocumentObjectGroupPython] H_element057  label="H_element : 0.136"  # scripted group (container) (typed FeaturePython)
  n = 0.102
FEATURE [App::DocumentObjectGroupPython] C_element063  label="C_element : 0.143"  # scripted group (container) (typed FeaturePython)
  n = 0.143
FEATURE [App::DocumentObjectGroupPython] N_element025  label="N_element : 0.034"  # scripted group (container) (typed FeaturePython)
  n = 0.034
FEATURE [App::DocumentObjectGroupPython] O_element065  label="O_element : 0.710"  # scripted group (container) (typed FeaturePython)
  n = 0.71
FEATURE [App::DocumentObjectGroupPython] Na_element011  label="Na_element : 0.098"  # scripted group (container) (typed FeaturePython)
  n = 0.001
FEATURE [App::DocumentObjectGroupPython] P_element007  label="P_element : 0.002"  # scripted group (container) (typed FeaturePython)
  n = 0.002
FEATURE [App::DocumentObjectGroupPython] S_element017  label="S_element : 0.018"  # scripted group (container) (typed FeaturePython)
  n = 0.003
FEATURE [App::DocumentObjectGroupPython] Cl_element016  label="Cl_element : 0.589"  # scripted group (container) (typed FeaturePython)
  n = 0.001
FEATURE [App::DocumentObjectGroupPython] K_element006  label="K_element : 0.004"  # scripted group (container) (typed FeaturePython)
  n = 0.004
FEATURE [App::DocumentObjectGroupPython] G4_MUSCLE_SKELETAL_ICRP  # scripted group (container) (typed FeaturePython)
  Dunit = g/cm3
  Dvalue = 1.05
  Group = -> [H_element057,C_element063,N_element025,O_element065,Na_element011,P_element007,S_element017,Cl_element016,K_element006]
  conduct = 2
  density = 1
  expand = 3
  formula = G4_MUSCLE_SKELETAL_ICRP
  name = G4_MUSCLE_SKELETAL_ICRP
  specific = 4
FEATURE [App::DocumentObjectGroupPython] H_element058  label="H_element : 0.137"  # scripted group (container) (typed FeaturePython)
  n = 0.102102
FEATURE [App::DocumentObjectGroupPython] C_element064  label="C_element : 0.123"  # scripted group (container) (typed FeaturePython)
  n = 0.123123
FEATURE [App::DocumentObjectGroupPython] N_element026  label="N_element : 0.756"  # scripted group (container) (typed FeaturePython)
  n = 0.035035
FEATURE [App::DocumentObjectGroupPython] O_element066  label="O_element : 0.730"  # scripted group (container) (typed FeaturePython)
  n = 0.72973
FEATURE [App::DocumentObjectGroupPython] Na_element012  label="Na_element : 0.099"  # scripted group (container) (typed FeaturePython)
  n = 0.001001
FEATURE [App::DocumentObjectGroupPython] P_element008  label="P_element : 0.106"  # scripted group (container) (typed FeaturePython)
  n = 0.002002
FEATURE [App::DocumentObjectGroupPython] S_element018  label="S_element : 0.019"  # scripted group (container) (typed FeaturePython)
  n = 0.004004
FEATURE [App::DocumentObjectGroupPython] K_element007  label="K_element : 0.016"  # scripted group (container) (typed FeaturePython)
  n = 0.003003
FEATURE [App::DocumentObjectGroupPython] G4_MUSCLE_STRIATED_ICRU  # scripted group (container) (typed FeaturePython)
  Dunit = g/cm3
  Dvalue = 1.04
  Group = -> [H_element058,C_element064,N_element026,O_element066,Na_element012,P_element008,S_element018,K_element007]
  conduct = 2
  density = 1
  expand = 3
  formula = G4_MUSCLE_STRIATED_ICRU
  name = G4_MUSCLE_STRIATED_ICRU
  specific = 4
FEATURE [App::DocumentObjectGroupPython] H_element059  label="H_element : 0.098"  # scripted group (container) (typed FeaturePython)
  n = 0.0982341
FEATURE [App::DocumentObjectGroupPython] C_element065  label="C_element : 0.156"  # scripted group (container) (typed FeaturePython)
  n = 0.156214
FEATURE [App::DocumentObjectGroupPython] N_element027  label="N_element : 0.757"  # scripted group (container) (typed FeaturePython)
  n = 0.035451
FEATURE [App::DocumentObjectGroupPython] O_element067  label="O_element : 0.880"  # scripted group (container) (typed FeaturePython)
  n = 0.710101
FEATURE [App::DocumentObjectGroupPython] G4_MUSCLE_WITH_SUCROSE  # scripted group (container) (typed FeaturePython)
  Dunit = g/cm3
  Dvalue = 1.11
  Group = -> [H_element059,C_element065,N_element027,O_element067]
  conduct = 2
  density = 1
  expand = 3
  formula = G4_MUSCLE_WITH_SUCROSE
  name = G4_MUSCLE_WITH_SUCROSE
  specific = 4
FEATURE [App::DocumentObjectGroupPython] H_element060  label="H_element : 0.138"  # scripted group (container) (typed FeaturePython)
  n = 0.101969
FEATURE [App::DocumentObjectGroupPython] C_element066  label="C_element : 0.120"  # scripted group (container) (typed FeaturePython)
  n = 0.120058
FEATURE [App::DocumentObjectGroupPython] N_element028  label="N_element : 0.758"  # scripted group (container) (typed FeaturePython)
  n = 0.035451
FEATURE [App::DocumentObjectGroupPython] O_element068  label="O_element : 0.743"  # scripted group (container) (typed FeaturePython)
  n = 0.742522
FEATURE [App::DocumentObjectGroupPython] G4_MUSCLE_WITHOUT_SUCROSE  # scripted group (container) (typed FeaturePython)
  Dunit = g/cm3
  Dvalue = 1.07
  Group = -> [H_element060,C_element066,N_element028,O_element068]
  conduct = 2
  density = 1
  expand = 3
  formula = G4_MUSCLE_WITHOUT_SUCROSE
  name = G4_MUSCLE_WITHOUT_SUCROSE
  specific = 4
FEATURE [App::DocumentObjectGroupPython] C_element067  label="C_element : 10"  # scripted group (container) (typed FeaturePython)
  n = 10
  ref = C_element
FEATURE [App::DocumentObjectGroupPython] H_element061  label="H_element : 030"  # scripted group (container) (typed FeaturePython)
  n = 8
  ref = H_element
FEATURE [App::DocumentObjectGroupPython] G4_NAPHTHALENE  # scripted group (container) (typed FeaturePython)
  Dunit = g/cm3
  Dvalue = 1.145
  Group = -> [C_element067,H_element061]
  conduct = 2
  density = 1
  expand = 3
  formula = G4_NAPHTHALENE
  name = G4_NAPHTHALENE
  specific = 4
FEATURE [App::DocumentObjectGroupPython] C_element068  label="C_element : 034"  # scripted group (container) (typed FeaturePython)
  n = 6
  ref = C_element
FEATURE [App::DocumentObjectGroupPython] H_element062  label="H_element : 031"  # scripted group (container) (typed FeaturePython)
  n = 5
  ref = H_element
FEATURE [App::DocumentObjectGroupPython] N_element029  label="N_element : 012"  # scripted group (container) (typed FeaturePython)
  n = 1
  ref = N_element
FEATURE [App::DocumentObjectGroupPython] O_element069  label="O_element : 034"  # scripted group (container) (typed FeaturePython)
  n = 2
  ref = O_element
FEATURE [App::DocumentObjectGroupPython] G4_NITROBENZENE  # scripted group (container) (typed FeaturePython)
  Dunit = g/cm3
  Dvalue = 1.19867
  Group = -> [C_element068,H_element062,N_element029,O_element069]
  conduct = 2
  density = 1
  expand = 3
  formula = G4_NITROBENZENE
  name = G4_NITROBENZENE
  specific = 4
FEATURE [App::DocumentObjectGroupPython] N_element030  label="N_element : 013"  # scripted group (container) (typed FeaturePython)
  n = 2
  ref = N_element
FEATURE [App::DocumentObjectGroupPython] O_element070  label="O_element : 035"  # scripted group (container) (typed FeaturePython)
  n = 1
  ref = O_element
FEATURE [App::DocumentObjectGroupPython] G4_NITROUS_OXIDE  # scripted group (container) (typed FeaturePython)
  Dunit = g/cm3
  Dvalue = 0.00183094
  Group = -> [N_element030,O_element070]
  conduct = 2
  density = 1
  expand = 3
  formula = G4_NITROUS_OXIDE
  name = G4_NITROUS_OXIDE
  specific = 4
FEATURE [App::DocumentObjectGroupPython] H_element063  label="H_element : 0.104"  # scripted group (container) (typed FeaturePython)
  n = 0.103509
FEATURE [App::DocumentObjectGroupPython] C_element069  label="C_element : 0.648"  # scripted group (container) (typed FeaturePython)
  n = 0.648416
FEATURE [App::DocumentObjectGroupPython] N_element031  label="N_element : 0.100"  # scripted group (container) (typed FeaturePython)
  n = 0.0995361
FEATURE [App::DocumentObjectGroupPython] O_element071  label="O_element : 0.149"  # scripted group (container) (typed FeaturePython)
  n = 0.148539
FEATURE [App::DocumentObjectGroupPython] G4_NYLON_8062  label="G4_NYLON-8062"  # scripted group (container) (typed FeaturePython)
  Dunit = g/cm3
  Dvalue = 1.08
  Group = -> [H_element063,C_element069,N_element031,O_element071]
  conduct = 2
  density = 1
  expand = 3
  formula = G4_NYLON-8062
  name = G4_NYLON-8062
  specific = 4
FEATURE [App::DocumentObjectGroupPython] C_element070  label="C_element : 035"  # scripted group (container) (typed FeaturePython)
  n = 6
  ref = C_element
FEATURE [App::DocumentObjectGroupPython] H_element064  label="H_element : 11"  # scripted group (container) (typed FeaturePython)
  n = 11
  ref = H_element
FEATURE [App::DocumentObjectGroupPython] N_element032  label="N_element : 014"  # scripted group (container) (typed FeaturePython)
  n = 1
  ref = N_element
FEATURE [App::DocumentObjectGroupPython] O_element072  label="O_element : 036"  # scripted group (container) (typed FeaturePython)
  n = 1
  ref = O_element
FEATURE [App::DocumentObjectGroupPython] G4_NYLON_6_6  label="G4_NYLON-6-6"  # scripted group (container) (typed FeaturePython)
  Dunit = g/cm3
  Dvalue = 1.14
  Group = -> [C_element070,H_element064,N_element032,O_element072]
  conduct = 2
  density = 1
  expand = 3
  formula = G4_NYLON-6-6
  name = G4_NYLON-6-6
  specific = 4
FEATURE [App::DocumentObjectGroupPython] H_element065  label="H_element : 0.139"  # scripted group (container) (typed FeaturePython)
  n = 0.107062
FEATURE [App::DocumentObjectGroupPython] C_element071  label="C_element : 0.680"  # scripted group (container) (typed FeaturePython)
  n = 0.680449
FEATURE [App::DocumentObjectGroupPython] N_element033  label="N_element : 0.099"  # scripted group (container) (typed FeaturePython)
  n = 0.099189
FEATURE [App::DocumentObjectGroupPython] O_element073  label="O_element : 0.113"  # scripted group (container) (typed FeaturePython)
  n = 0.1133
FEATURE [App::DocumentObjectGroupPython] G4_NYLON_6_10  label="G4_NYLON-6-10"  # scripted group (container) (typed FeaturePython)
  Dunit = g/cm3
  Dvalue = 1.14
  Group = -> [H_element065,C_element071,N_element033,O_element073]
  conduct = 2
  density = 1
  expand = 3
  formula = G4_NYLON-6-10
  name = G4_NYLON-6-10
  specific = 4
FEATURE [App::DocumentObjectGroupPython] H_element066  label="H_element : 0.140"  # scripted group (container) (typed FeaturePython)
  n = 0.115476
FEATURE [App::DocumentObjectGroupPython] C_element072  label="C_element : 0.721"  # scripted group (container) (typed FeaturePython)
  n = 0.720818
FEATURE [App::DocumentObjectGroupPython] N_element034  label="N_element : 0.076"  # scripted group (container) (typed FeaturePython)
  n = 0.0764169
FEATURE [App::DocumentObjectGroupPython] O_element074  label="O_element : 0.087"  # scripted group (container) (typed FeaturePython)
  n = 0.0872889
FEATURE [App::DocumentObjectGroupPython] G4_NYLON_11_RILSAN  label="G4_NYLON-11_RILSAN"  # scripted group (container) (typed FeaturePython)
  Dunit = g/cm3
  Dvalue = 1.425
  Group = -> [H_element066,C_element072,N_element034,O_element074]
  conduct = 2
  density = 1
  expand = 3
  formula = G4_NYLON-11_RILSAN
  name = G4_NYLON-11_RILSAN
  specific = 4
FEATURE [App::DocumentObjectGroupPython] C_element073  label="C_element : 8"  # scripted group (container) (typed FeaturePython)
  n = 8
  ref = C_element
FEATURE [App::DocumentObjectGroupPython] H_element067  label="H_element : 18"  # scripted group (container) (typed FeaturePython)
  n = 18
  ref = H_element
FEATURE [App::DocumentObjectGroupPython] G4_OCTANE  # scripted group (container) (typed FeaturePython)
  Dunit = g/cm3
  Dvalue = 0.7026
  Group = -> [C_element073,H_element067]
  conduct = 2
  density = 1
  expand = 3
  formula = G4_OCTANE
  name = G4_OCTANE
  specific = 4
FEATURE [App::DocumentObjectGroupPython] C_element074  label="C_element : 25"  # scripted group (container) (typed FeaturePython)
  n = 25
  ref = C_element
FEATURE [App::DocumentObjectGroupPython] H_element068  label="H_element : 52"  # scripted group (container) (typed FeaturePython)
  n = 52
  ref = H_element
FEATURE [App::DocumentObjectGroupPython] G4_PARAFFIN  # scripted group (container) (typed FeaturePython)
  Dunit = g/cm3
  Dvalue = 0.93
  Group = -> [C_element074,H_element068]
  conduct = 2
  density = 1
  expand = 3
  formula = G4_PARAFFIN
  name = G4_PARAFFIN
  specific = 4
FEATURE [App::DocumentObjectGroupPython] C_element075  label="C_element : 036"  # scripted group (container) (typed FeaturePython)
  n = 5
  ref = C_element
FEATURE [App::DocumentObjectGroupPython] H_element069  label="H_element : 032"  # scripted group (container) (typed FeaturePython)
  n = 12
  ref = H_element
FEATURE [App::DocumentObjectGroupPython] G4_N_PENTANE  label="G4_N-PENTANE"  # scripted group (container) (typed FeaturePython)
  Dunit = g/cm3
  Dvalue = 0.6262
  Group = -> [C_element075,H_element069]
  conduct = 2
  density = 1
  expand = 3
  formula = G4_N-PENTANE
  name = G4_N-PENTANE
  specific = 4
FEATURE [App::DocumentObjectGroupPython] H_element070  label="H_element : 0.014"  # scripted group (container) (typed FeaturePython)
  n = 0.0141
FEATURE [App::DocumentObjectGroupPython] C_element076  label="C_element : 0.072"  # scripted group (container) (typed FeaturePython)
  n = 0.072261
FEATURE [App::DocumentObjectGroupPython] N_element035  label="N_element : 0.019"  # scripted group (container) (typed FeaturePython)
  n = 0.01932
FEATURE [App::DocumentObjectGroupPython] O_element075  label="O_element : 0.066"  # scripted group (container) (typed FeaturePython)
  n = 0.066101
FEATURE [App::DocumentObjectGroupPython] S_element019  label="S_element : 0.020"  # scripted group (container) (typed FeaturePython)
  n = 0.00189
FEATURE [App::DocumentObjectGroupPython] Br_element004  label="Br_element : 0.349"  # scripted group (container) (typed FeaturePython)
  n = 0.349103
FEATURE [App::DocumentObjectGroupPython] Ag_element001  label="Ag_element : 0.474"  # scripted group (container) (typed FeaturePython)
  n = 0.474105
FEATURE [App::DocumentObjectGroupPython] I_element005  label="I_element : 0.003"  # scripted group (container) (typed FeaturePython)
  n = 0.00312
FEATURE [App::DocumentObjectGroupPython] G4_PHOTO_EMULSION  # scripted group (container) (typed FeaturePython)
  Dunit = g/cm3
  Dvalue = 3.815
  Group = -> [H_element070,C_element076,N_element035,O_element075,S_element019,Br_element004,Ag_element001,I_element005]
  conduct = 2
  density = 1
  expand = 3
  formula = G4_PHOTO_EMULSION
  name = G4_PHOTO_EMULSION
  specific = 4
FEATURE [App::DocumentObjectGroupPython] C_element077  label="C_element : 9"  # scripted group (container) (typed FeaturePython)
  n = 9
  ref = C_element
FEATURE [App::DocumentObjectGroupPython] H_element071  label="H_element : 033"  # scripted group (container) (typed FeaturePython)
  n = 10
  ref = H_element
FEATURE [App::DocumentObjectGroupPython] G4_PLASTIC_SC_VINYLTOLUENE  # scripted group (container) (typed FeaturePython)
  Dunit = g/cm3
  Dvalue = 1.032
  Group = -> [C_element077,H_element071]
  conduct = 2
  density = 1
  expand = 3
  formula = G4_PLASTIC_SC_VINYLTOLUENE
  name = G4_PLASTIC_SC_VINYLTOLUENE
  specific = 4
FEATURE [App::DocumentObjectGroupPython] Pu_element001  label="Pu_element : 1"  # scripted group (container) (typed FeaturePython)
  n = 1
  ref = Pu_element
FEATURE [App::DocumentObjectGroupPython] O_element076  label="O_element : 037"  # scripted group (container) (typed FeaturePython)
  n = 2
  ref = O_element
FEATURE [App::DocumentObjectGroupPython] G4_PLUTONIUM_DIOXIDE  # scripted group (container) (typed FeaturePython)
  Dunit = g/cm3
  Dvalue = 11.46
  Group = -> [Pu_element001,O_element076]
  conduct = 2
  density = 1
  expand = 3
  formula = G4_PLUTONIUM_DIOXIDE
  name = G4_PLUTONIUM_DIOXIDE
  specific = 4
FEATURE [App::DocumentObjectGroupPython] C_element078  label="C_element : 037"  # scripted group (container) (typed FeaturePython)
  n = 3
  ref = C_element
FEATURE [App::DocumentObjectGroupPython] H_element072  label="H_element : 034"  # scripted group (container) (typed FeaturePython)
  n = 3
  ref = H_element
FEATURE [App::DocumentObjectGroupPython] N_element036  label="N_element : 015"  # scripted group (container) (typed FeaturePython)
  n = 1
  ref = N_element
FEATURE [App::DocumentObjectGroupPython] G4_POLYACRYLONITRILE  # scripted group (container) (typed FeaturePython)
  Dunit = g/cm3
  Dvalue = 1.17
  Group = -> [C_element078,H_element072,N_element036]
  conduct = 2
  density = 1
  expand = 3
  formula = G4_POLYACRYLONITRILE
  name = G4_POLYACRYLONITRILE
  specific = 4
FEATURE [App::DocumentObjectGroupPython] C_element079  label="C_element : 16"  # scripted group (container) (typed FeaturePython)
  n = 16
  ref = C_element
FEATURE [App::DocumentObjectGroupPython] H_element073  label="H_element : 035"  # scripted group (container) (typed FeaturePython)
  n = 14
  ref = H_element
FEATURE [App::DocumentObjectGroupPython] O_element077  label="O_element : 038"  # scripted group (container) (typed FeaturePython)
  n = 3
  ref = O_element
FEATURE [App::DocumentObjectGroupPython] G4_POLYCARBONATE  # scripted group (container) (typed FeaturePython)
  Dunit = g/cm3
  Dvalue = 1.2
  Group = -> [C_element079,H_element073,O_element077]
  conduct = 2
  density = 1
  expand = 3
  formula = G4_POLYCARBONATE
  name = G4_POLYCARBONATE
  specific = 4
FEATURE [App::DocumentObjectGroupPython] C_element080  label="C_element : 038"  # scripted group (container) (typed FeaturePython)
  n = 8
  ref = C_element
FEATURE [App::DocumentObjectGroupPython] H_element074  label="H_element : 036"  # scripted group (container) (typed FeaturePython)
  n = 7
  ref = H_element
FEATURE [App::DocumentObjectGroupPython] Cl_element017  label="Cl_element : 007"  # scripted group (container) (typed FeaturePython)
  n = 1
  ref = Cl_element
FEATURE [App::DocumentObjectGroupPython] G4_POLYCHLOROSTYRENE  # scripted group (container) (typed FeaturePython)
  Dunit = g/cm3
  Dvalue = 1.3
  Group = -> [C_element080,H_element074,Cl_element017]
  conduct = 2
  density = 1
  expand = 3
  formula = G4_POLYCHLOROSTYRENE
  name = G4_POLYCHLOROSTYRENE
  specific = 4
FEATURE [App::DocumentObjectGroupPython] C_element081  label="C_element : 039"  # scripted group (container) (typed FeaturePython)
  n = 1
  ref = C_element
FEATURE [App::DocumentObjectGroupPython] H_element075  label="H_element : 037"  # scripted group (container) (typed FeaturePython)
  n = 2
  ref = H_element
FEATURE [App::DocumentObjectGroupPython] G4_POLYETHYLENE  # scripted group (container) (typed FeaturePython)
  Dunit = g/cm3
  Dvalue = 0.94
  Group = -> [C_element081,H_element075]
  conduct = 2
  density = 1
  expand = 3
  formula = G4_POLYETHYLENE
  name = G4_POLYETHYLENE
  specific = 4
FEATURE [App::DocumentObjectGroupPython] C_element082  label="C_element : 040"  # scripted group (container) (typed FeaturePython)
  n = 10
  ref = C_element
FEATURE [App::DocumentObjectGroupPython] H_element076  label="H_element : 038"  # scripted group (container) (typed FeaturePython)
  n = 8
  ref = H_element
FEATURE [App::DocumentObjectGroupPython] O_element078  label="O_element : 039"  # scripted group (container) (typed FeaturePython)
  n = 4
  ref = O_element
FEATURE [App::DocumentObjectGroupPython] G4_MYLAR  # scripted group (container) (typed FeaturePython)
  Dunit = g/cm3
  Dvalue = 1.4
  Group = -> [C_element082,H_element076,O_element078]
  conduct = 2
  density = 1
  expand = 3
  formula = G4_MYLAR
  name = G4_MYLAR
  specific = 4
FEATURE [App::DocumentObjectGroupPython] C_element083  label="C_element : 041"  # scripted group (container) (typed FeaturePython)
  n = 5
  ref = C_element
FEATURE [App::DocumentObjectGroupPython] H_element077  label="H_element : 039"  # scripted group (container) (typed FeaturePython)
  n = 8
  ref = H_element
FEATURE [App::DocumentObjectGroupPython] O_element079  label="O_element : 040"  # scripted group (container) (typed FeaturePython)
  n = 2
  ref = O_element
FEATURE [App::DocumentObjectGroupPython] G4_PLEXIGLASS  # scripted group (container) (typed FeaturePython)
  Dunit = g/cm3
  Dvalue = 1.19
  Group = -> [C_element083,H_element077,O_element079]
  conduct = 2
  density = 1
  expand = 3
  formula = G4_PLEXIGLASS
  name = G4_PLEXIGLASS
  specific = 4
FEATURE [App::DocumentObjectGroupPython] C_element084  label="C_element : 042"  # scripted group (container) (typed FeaturePython)
  n = 1
  ref = C_element
FEATURE [App::DocumentObjectGroupPython] H_element078  label="H_element : 040"  # scripted group (container) (typed FeaturePython)
  n = 2
  ref = H_element
FEATURE [App::DocumentObjectGroupPython] O_element080  label="O_element : 041"  # scripted group (container) (typed FeaturePython)
  n = 1
  ref = O_element
FEATURE [App::DocumentObjectGroupPython] G4_POLYOXYMETHYLENE  # scripted group (container) (typed FeaturePython)
  Dunit = g/cm3
  Dvalue = 1.425
  Group = -> [C_element084,H_element078,O_element080]
  conduct = 2
  density = 1
  expand = 3
  formula = G4_POLYOXYMETHYLENE
  name = G4_POLYOXYMETHYLENE
  specific = 4
FEATURE [App::DocumentObjectGroupPython] C_element085  label="C_element : 043"  # scripted group (container) (typed FeaturePython)
  n = 2
  ref = C_element
FEATURE [App::DocumentObjectGroupPython] H_element079  label="H_element : 041"  # scripted group (container) (typed FeaturePython)
  n = 4
  ref = H_element
FEATURE [App::DocumentObjectGroupPython] G4_POLYPROPYLENE  # scripted group (container) (typed FeaturePython)
  Dunit = g/cm3
  Dvalue = 0.9
  Group = -> [C_element085,H_element079]
  conduct = 2
  density = 1
  expand = 3
  formula = G4_POLYPROPYLENE
  name = G4_POLYPROPYLENE
  specific = 4
FEATURE [App::DocumentObjectGroupPython] C_element086  label="C_element : 044"  # scripted group (container) (typed FeaturePython)
  n = 8
  ref = C_element
FEATURE [App::DocumentObjectGroupPython] H_element080  label="H_element : 042"  # scripted group (container) (typed FeaturePython)
  n = 8
  ref = H_element
FEATURE [App::DocumentObjectGroupPython] G4_POLYSTYRENE  # scripted group (container) (typed FeaturePython)
  Dunit = g/cm3
  Dvalue = 1.06
  Group = -> [C_element086,H_element080]
  conduct = 2
  density = 1
  expand = 3
  formula = G4_POLYSTYRENE
  name = G4_POLYSTYRENE
  specific = 4
FEATURE [App::DocumentObjectGroupPython] C_element087  label="C_element : 045"  # scripted group (container) (typed FeaturePython)
  n = 2
  ref = C_element
FEATURE [App::DocumentObjectGroupPython] F_element014  label="F_element : 4"  # scripted group (container) (typed FeaturePython)
  n = 4
  ref = F_element
FEATURE [App::DocumentObjectGroupPython] G4_TEFLON  # scripted group (container) (typed FeaturePython)
  Dunit = g/cm3
  Dvalue = 2.2
  Group = -> [C_element087,F_element014]
  conduct = 2
  density = 1
  expand = 3
  formula = G4_TEFLON
  name = G4_TEFLON
  specific = 4
FEATURE [App::DocumentObjectGroupPython] C_element088  label="C_element : 046"  # scripted group (container) (typed FeaturePython)
  n = 2
  ref = C_element
FEATURE [App::DocumentObjectGroupPython] F_element015  label="F_element : 006"  # scripted group (container) (typed FeaturePython)
  n = 3
  ref = F_element
FEATURE [App::DocumentObjectGroupPython] Cl_element018  label="Cl_element : 008"  # scripted group (container) (typed FeaturePython)
  n = 1
  ref = Cl_element
FEATURE [App::DocumentObjectGroupPython] G4_POLYTRIFLUOROCHLOROETHYLENE  # scripted group (container) (typed FeaturePython)
  Dunit = g/cm3
  Dvalue = 2.1
  Group = -> [C_element088,F_element015,Cl_element018]
  conduct = 2
  density = 1
  expand = 3
  formula = G4_POLYTRIFLUOROCHLOROETHYLENE
  name = G4_POLYTRIFLUOROCHLOROETHYLENE
  specific = 4
FEATURE [App::DocumentObjectGroupPython] C_element089  label="C_element : 047"  # scripted group (container) (typed FeaturePython)
  n = 4
  ref = C_element
FEATURE [App::DocumentObjectGroupPython] H_element081  label="H_element : 043"  # scripted group (container) (typed FeaturePython)
  n = 6
  ref = H_element
FEATURE [App::DocumentObjectGroupPython] O_element081  label="O_element : 042"  # scripted group (container) (typed FeaturePython)
  n = 2
  ref = O_element
FEATURE [App::DocumentObjectGroupPython] G4_POLYVINYL_ACETATE  # scripted group (container) (typed FeaturePython)
  Dunit = g/cm3
  Dvalue = 1.19
  Group = -> [C_element089,H_element081,O_element081]
  conduct = 2
  density = 1
  expand = 3
  formula = G4_POLYVINYL_ACETATE
  name = G4_POLYVINYL_ACETATE
  specific = 4
FEATURE [App::DocumentObjectGroupPython] C_element090  label="C_element : 048"  # scripted group (container) (typed FeaturePython)
  n = 2
  ref = C_element
FEATURE [App::DocumentObjectGroupPython] H_element082  label="H_element : 044"  # scripted group (container) (typed FeaturePython)
  n = 4
  ref = H_element
FEATURE [App::DocumentObjectGroupPython] O_element082  label="O_element : 043"  # scripted group (container) (typed FeaturePython)
  n = 1
  ref = O_element
FEATURE [App::DocumentObjectGroupPython] G4_POLYVINYL_ALCOHOL  # scripted group (container) (typed FeaturePython)
  Dunit = g/cm3
  Dvalue = 1.3
  Group = -> [C_element090,H_element082,O_element082]
  conduct = 2
  density = 1
  expand = 3
  formula = G4_POLYVINYL_ALCOHOL
  name = G4_POLYVINYL_ALCOHOL
  specific = 4
FEATURE [App::DocumentObjectGroupPython] C_element091  label="C_element : 049"  # scripted group (container) (typed FeaturePython)
  n = 8
  ref = C_element
FEATURE [App::DocumentObjectGroupPython] H_element083  label="H_element : 045"  # scripted group (container) (typed FeaturePython)
  n = 14
  ref = H_element
FEATURE [App::DocumentObjectGroupPython] O_element083  label="O_element : 044"  # scripted group (container) (typed FeaturePython)
  n = 2
  ref = O_element
FEATURE [App::DocumentObjectGroupPython] G4_POLYVINYL_BUTYRAL  # scripted group (container) (typed FeaturePython)
  Dunit = g/cm3
  Dvalue = 1.12
  Group = -> [C_element091,H_element083,O_element083]
  conduct = 2
  density = 1
  expand = 3
  formula = G4_POLYVINYL_BUTYRAL
  name = G4_POLYVINYL_BUTYRAL
  specific = 4
FEATURE [App::DocumentObjectGroupPython] C_element092  label="C_element : 050"  # scripted group (container) (typed FeaturePython)
  n = 2
  ref = C_element
FEATURE [App::DocumentObjectGroupPython] H_element084  label="H_element : 046"  # scripted group (container) (typed FeaturePython)
  n = 3
  ref = H_element
FEATURE [App::DocumentObjectGroupPython] Cl_element019  label="Cl_element : 009"  # scripted group (container) (typed FeaturePython)
  n = 1
  ref = Cl_element
FEATURE [App::DocumentObjectGroupPython] G4_POLYVINYL_CHLORIDE  # scripted group (container) (typed FeaturePython)
  Dunit = g/cm3
  Dvalue = 1.3
  Group = -> [C_element092,H_element084,Cl_element019]
  conduct = 2
  density = 1
  expand = 3
  formula = G4_POLYVINYL_CHLORIDE
  name = G4_POLYVINYL_CHLORIDE
  specific = 4
FEATURE [App::DocumentObjectGroupPython] C_element093  label="C_element : 051"  # scripted group (container) (typed FeaturePython)
  n = 2
  ref = C_element
FEATURE [App::DocumentObjectGroupPython] H_element085  label="H_element : 047"  # scripted group (container) (typed FeaturePython)
  n = 2
  ref = H_element
FEATURE [App::DocumentObjectGroupPython] Cl_element020  label="Cl_element : 010"  # scripted group (container) (typed FeaturePython)
  n = 2
  ref = Cl_element
FEATURE [App::DocumentObjectGroupPython] G4_POLYVINYLIDENE_CHLORIDE  # scripted group (container) (typed FeaturePython)
  Dunit = g/cm3
  Dvalue = 1.7
  Group = -> [C_element093,H_element085,Cl_element020]
  conduct = 2
  density = 1
  expand = 3
  formula = G4_POLYVINYLIDENE_CHLORIDE
  name = G4_POLYVINYLIDENE_CHLORIDE
  specific = 4
FEATURE [App::DocumentObjectGroupPython] C_element094  label="C_element : 052"  # scripted group (container) (typed FeaturePython)
  n = 2
  ref = C_element
FEATURE [App::DocumentObjectGroupPython] H_element086  label="H_element : 048"  # scripted group (container) (typed FeaturePython)
  n = 2
  ref = H_element
FEATURE [App::DocumentObjectGroupPython] F_element016  label="F_element : 007"  # scripted group (container) (typed FeaturePython)
  n = 2
  ref = F_element
FEATURE [App::DocumentObjectGroupPython] G4_POLYVINYLIDENE_FLUORIDE  # scripted group (container) (typed FeaturePython)
  Dunit = g/cm3
  Dvalue = 1.76
  Group = -> [C_element094,H_element086,F_element016]
  conduct = 2
  density = 1
  expand = 3
  formula = G4_POLYVINYLIDENE_FLUORIDE
  name = G4_POLYVINYLIDENE_FLUORIDE
  specific = 4
FEATURE [App::DocumentObjectGroupPython] C_element095  label="C_element : 053"  # scripted group (container) (typed FeaturePython)
  n = 6
  ref = C_element
FEATURE [App::DocumentObjectGroupPython] H_element087  label="H_element : 9"  # scripted group (container) (typed FeaturePython)
  n = 9
  ref = H_element
FEATURE [App::DocumentObjectGroupPython] N_element037  label="N_element : 016"  # scripted group (container) (typed FeaturePython)
  n = 1
  ref = N_element
FEATURE [App::DocumentObjectGroupPython] O_element084  label="O_element : 045"  # scripted group (container) (typed FeaturePython)
  n = 1
  ref = O_element
FEATURE [App::DocumentObjectGroupPython] G4_POLYVINYL_PYRROLIDONE  # scripted group (container) (typed FeaturePython)
  Dunit = g/cm3
  Dvalue = 1.25
  Group = -> [C_element095,H_element087,N_element037,O_element084]
  conduct = 2
  density = 1
  expand = 3
  formula = G4_POLYVINYL_PYRROLIDONE
  name = G4_POLYVINYL_PYRROLIDONE
  specific = 4
FEATURE [App::DocumentObjectGroupPython] K_element008  label="K_element : 1"  # scripted group (container) (typed FeaturePython)
  n = 1
  ref = K_element
FEATURE [App::DocumentObjectGroupPython] I_element006  label="I_element : 003"  # scripted group (container) (typed FeaturePython)
  n = 1
  ref = I_element
FEATURE [App::DocumentObjectGroupPython] G4_POTASSIUM_IODIDE  # scripted group (container) (typed FeaturePython)
  Dunit = g/cm3
  Dvalue = 3.13
  Group = -> [K_element008,I_element006]
  conduct = 2
  density = 1
  expand = 3
  formula = G4_POTASSIUM_IODIDE
  name = G4_POTASSIUM_IODIDE
  specific = 4
FEATURE [App::DocumentObjectGroupPython] K_element009  label="K_element : 2"  # scripted group (container) (typed FeaturePython)
  n = 2
  ref = K_element
FEATURE [App::DocumentObjectGroupPython] O_element085  label="O_element : 046"  # scripted group (container) (typed FeaturePython)
  n = 1
  ref = O_element
FEATURE [App::DocumentObjectGroupPython] G4_POTASSIUM_OXIDE  # scripted group (container) (typed FeaturePython)
  Dunit = g/cm3
  Dvalue = 2.32
  Group = -> [K_element009,O_element085]
  conduct = 2
  density = 1
  expand = 3
  formula = G4_POTASSIUM_OXIDE
  name = G4_POTASSIUM_OXIDE
  specific = 4
FEATURE [App::DocumentObjectGroupPython] C_element096  label="C_element : 054"  # scripted group (container) (typed FeaturePython)
  n = 3
  ref = C_element
FEATURE [App::DocumentObjectGroupPython] H_element088  label="H_element : 049"  # scripted group (container) (typed FeaturePython)
  n = 8
  ref = H_element
FEATURE [App::DocumentObjectGroupPython] G4_PROPANE  # scripted group (container) (typed FeaturePython)
  Dunit = g/cm3
  Dvalue = 0.00187939
  Group = -> [C_element096,H_element088]
  conduct = 2
  density = 1
  expand = 3
  formula = G4_PROPANE
  name = G4_PROPANE
  specific = 4
FEATURE [App::DocumentObjectGroupPython] C_element097  label="C_element : 055"  # scripted group (container) (typed FeaturePython)
  n = 3
  ref = C_element
FEATURE [App::DocumentObjectGroupPython] H_element089  label="H_element : 050"  # scripted group (container) (typed FeaturePython)
  n = 8
  ref = H_element
FEATURE [App::DocumentObjectGroupPython] G4_lPROPANE  # scripted group (container) (typed FeaturePython)
  Dunit = g/cm3
  Dvalue = 0.43
  Group = -> [C_element097,H_element089]
  conduct = 2
  density = 1
  expand = 3
  formula = G4_lPROPANE
  name = G4_lPROPANE
  specific = 4
FEATURE [App::DocumentObjectGroupPython] C_element098  label="C_element : 056"  # scripted group (container) (typed FeaturePython)
  n = 3
  ref = C_element
FEATURE [App::DocumentObjectGroupPython] H_element090  label="H_element : 051"  # scripted group (container) (typed FeaturePython)
  n = 8
  ref = H_element
FEATURE [App::DocumentObjectGroupPython] O_element086  label="O_element : 047"  # scripted group (container) (typed FeaturePython)
  n = 1
  ref = O_element
FEATURE [App::DocumentObjectGroupPython] G4_N_PROPYL_ALCOHOL  label="G4_N-PROPYL_ALCOHOL"  # scripted group (container) (typed FeaturePython)
  Dunit = g/cm3
  Dvalue = 0.8035
  Group = -> [C_element098,H_element090,O_element086]
  conduct = 2
  density = 1
  expand = 3
  formula = G4_N-PROPYL_ALCOHOL
  name = G4_N-PROPYL_ALCOHOL
  specific = 4
FEATURE [App::DocumentObjectGroupPython] C_element099  label="C_element : 057"  # scripted group (container) (typed FeaturePython)
  n = 5
  ref = C_element
FEATURE [App::DocumentObjectGroupPython] H_element091  label="H_element : 052"  # scripted group (container) (typed FeaturePython)
  n = 5
  ref = H_element
FEATURE [App::DocumentObjectGroupPython] N_element038  label="N_element : 017"  # scripted group (container) (typed FeaturePython)
  n = 1
  ref = N_element
FEATURE [App::DocumentObjectGroupPython] G4_PYRIDINE  # scripted group (container) (typed FeaturePython)
  Dunit = g/cm3
  Dvalue = 0.9819
  Group = -> [C_element099,H_element091,N_element038]
  conduct = 2
  density = 1
  expand = 3
  formula = G4_PYRIDINE
  name = G4_PYRIDINE
  specific = 4
FEATURE [App::DocumentObjectGroupPython] H_element092  label="H_element : 0.144"  # scripted group (container) (typed FeaturePython)
  n = 0.143711
FEATURE [App::DocumentObjectGroupPython] C_element100  label="C_element : 0.856"  # scripted group (container) (typed FeaturePython)
  n = 0.856289
FEATURE [App::DocumentObjectGroupPython] G4_RUBBER_BUTYL  # scripted group (container) (typed FeaturePython)
  Dunit = g/cm3
  Dvalue = 0.92
  Group = -> [H_element092,C_element100]
  conduct = 2
  density = 1
  expand = 3
  formula = G4_RUBBER_BUTYL
  name = G4_RUBBER_BUTYL
  specific = 4
FEATURE [App::DocumentObjectGroupPython] H_element093  label="H_element : 0.118"  # scripted group (container) (typed FeaturePython)
  n = 0.118371
FEATURE [App::DocumentObjectGroupPython] C_element101  label="C_element : 0.882"  # scripted group (container) (typed FeaturePython)
  n = 0.881629
FEATURE [App::DocumentObjectGroupPython] G4_RUBBER_NATURAL  # scripted group (container) (typed FeaturePython)
  Dunit = g/cm3
  Dvalue = 0.92
  Group = -> [H_element093,C_element101]
  conduct = 2
  density = 1
  expand = 3
  formula = G4_RUBBER_NATURAL
  name = G4_RUBBER_NATURAL
  specific = 4
FEATURE [App::DocumentObjectGroupPython] H_element094  label="H_element : 0.145"  # scripted group (container) (typed FeaturePython)
  n = 0.05692
FEATURE [App::DocumentObjectGroupPython] C_element102  label="C_element : 0.543"  # scripted group (container) (typed FeaturePython)
  n = 0.542646
FEATURE [App::DocumentObjectGroupPython] Cl_element021  label="Cl_element : 0.400"  # scripted group (container) (typed FeaturePython)
  n = 0.400434
FEATURE [App::DocumentObjectGroupPython] G4_RUBBER_NEOPRENE  # scripted group (container) (typed FeaturePython)
  Dunit = g/cm3
  Dvalue = 1.23
  Group = -> [H_element094,C_element102,Cl_element021]
  conduct = 2
  density = 1
  expand = 3
  formula = G4_RUBBER_NEOPRENE
  name = G4_RUBBER_NEOPRENE
  specific = 4
FEATURE [App::DocumentObjectGroupPython] Si_element006  label="Si_element : 1"  # scripted group (container) (typed FeaturePython)
  n = 1
  ref = Si_element
FEATURE [App::DocumentObjectGroupPython] O_element087  label="O_element : 048"  # scripted group (container) (typed FeaturePython)
  n = 2
  ref = O_element
FEATURE [App::DocumentObjectGroupPython] G4_SILICON_DIOXIDE  # scripted group (container) (typed FeaturePython)
  Dunit = g/cm3
  Dvalue = 2.32
  Group = -> [Si_element006,O_element087]
  conduct = 2
  density = 1
  expand = 3
  formula = G4_SILICON_DIOXIDE
  name = G4_SILICON_DIOXIDE
  specific = 4
FEATURE [App::DocumentObjectGroupPython] Ag_element002  label="Ag_element : 1"  # scripted group (container) (typed FeaturePython)
  n = 1
  ref = Ag_element
FEATURE [App::DocumentObjectGroupPython] Br_element005  label="Br_element : 003"  # scripted group (container) (typed FeaturePython)
  n = 1
  ref = Br_element
FEATURE [App::DocumentObjectGroupPython] G4_SILVER_BROMIDE  # scripted group (container) (typed FeaturePython)
  Dunit = g/cm3
  Dvalue = 6.473
  Group = -> [Ag_element002,Br_element005]
  conduct = 2
  density = 1
  expand = 3
  formula = G4_SILVER_BROMIDE
  name = G4_SILVER_BROMIDE
  specific = 4
FEATURE [App::DocumentObjectGroupPython] Ag_element003  label="Ag_element : 002"  # scripted group (container) (typed FeaturePython)
  n = 1
  ref = Ag_element
FEATURE [App::DocumentObjectGroupPython] Cl_element022  label="Cl_element : 011"  # scripted group (container) (typed FeaturePython)
  n = 1
  ref = Cl_element
FEATURE [App::DocumentObjectGroupPython] G4_SILVER_CHLORIDE  # scripted group (container) (typed FeaturePython)
  Dunit = g/cm3
  Dvalue = 5.56
  Group = -> [Ag_element003,Cl_element022]
  conduct = 2
  density = 1
  expand = 3
  formula = G4_SILVER_CHLORIDE
  name = G4_SILVER_CHLORIDE
  specific = 4
FEATURE [App::DocumentObjectGroupPython] Br_element006  label="Br_element : 0.423"  # scripted group (container) (typed FeaturePython)
  n = 0.422895
FEATURE [App::DocumentObjectGroupPython] Ag_element004  label="Ag_element : 0.574"  # scripted group (container) (typed FeaturePython)
  n = 0.573748
FEATURE [App::DocumentObjectGroupPython] I_element007  label="I_element : 0.649"  # scripted group (container) (typed FeaturePython)
  n = 0.003357
FEATURE [App::DocumentObjectGroupPython] G4_SILVER_HALIDES  # scripted group (container) (typed FeaturePython)
  Dunit = g/cm3
  Dvalue = 6.47
  Group = -> [Br_element006,Ag_element004,I_element007]
  conduct = 2
  density = 1
  expand = 3
  formula = G4_SILVER_HALIDES
  name = G4_SILVER_HALIDES
  specific = 4
FEATURE [App::DocumentObjectGroupPython] Ag_element005  label="Ag_element : 003"  # scripted group (container) (typed FeaturePython)
  n = 1
  ref = Ag_element
FEATURE [App::DocumentObjectGroupPython] I_element008  label="I_element : 004"  # scripted group (container) (typed FeaturePython)
  n = 1
  ref = I_element
FEATURE [App::DocumentObjectGroupPython] G4_SILVER_IODIDE  # scripted group (container) (typed FeaturePython)
  Dunit = g/cm3
  Dvalue = 6.01
  Group = -> [Ag_element005,I_element008]
  conduct = 2
  density = 1
  expand = 3
  formula = G4_SILVER_IODIDE
  name = G4_SILVER_IODIDE
  specific = 4
FEATURE [App::DocumentObjectGroupPython] H_element095  label="H_element : 0.100"  # scripted group (container) (typed FeaturePython)
  n = 0.1
FEATURE [App::DocumentObjectGroupPython] C_element103  label="C_element : 0.204"  # scripted group (container) (typed FeaturePython)
  n = 0.204
FEATURE [App::DocumentObjectGroupPython] N_element039  label="N_element : 0.759"  # scripted group (container) (typed FeaturePython)
  n = 0.042
FEATURE [App::DocumentObjectGroupPython] O_element088  label="O_element : 0.645"  # scripted group (container) (typed FeaturePython)
  n = 0.645
FEATURE [App::DocumentObjectGroupPython] Na_element013  label="Na_element : 0.100"  # scripted group (container) (typed FeaturePython)
  n = 0.002
FEATURE [App::DocumentObjectGroupPython] P_element009  label="P_element : 0.107"  # scripted group (container) (typed FeaturePython)
  n = 0.001
FEATURE [App::DocumentObjectGroupPython] S_element020  label="S_element : 0.021"  # scripted group (container) (typed FeaturePython)
  n = 0.002
FEATURE [App::DocumentObjectGroupPython] Cl_element023  label="Cl_element : 0.590"  # scripted group (container) (typed FeaturePython)
  n = 0.003
FEATURE [App::DocumentObjectGroupPython] K_element010  label="K_element : 0.001"  # scripted group (container) (typed FeaturePython)
  n = 0.001
FEATURE [App::DocumentObjectGroupPython] G4_SKIN_ICRP  # scripted group (container) (typed FeaturePython)
  Dunit = g/cm3
  Dvalue = 1.09
  Group = -> [H_element095,C_element103,N_element039,O_element088,Na_element013,P_element009,S_element020,Cl_element023,K_element010]
  conduct = 2
  density = 1
  expand = 3
  formula = G4_SKIN_ICRP
  name = G4_SKIN_ICRP
  specific = 4
FEATURE [App::DocumentObjectGroupPython] Na_element014  label="Na_element : 2"  # scripted group (container) (typed FeaturePython)
  n = 2
  ref = Na_element
FEATURE [App::DocumentObjectGroupPython] C_element104  label="C_element : 058"  # scripted group (container) (typed FeaturePython)
  n = 1
  ref = C_element
FEATURE [App::DocumentObjectGroupPython] O_element089  label="O_element : 049"  # scripted group (container) (typed FeaturePython)
  n = 3
  ref = O_element
FEATURE [App::DocumentObjectGroupPython] G4_SODIUM_CARBONATE  # scripted group (container) (typed FeaturePython)
  Dunit = g/cm3
  Dvalue = 2.532
  Group = -> [Na_element014,C_element104,O_element089]
  conduct = 2
  density = 1
  expand = 3
  formula = G4_SODIUM_CARBONATE
  name = G4_SODIUM_CARBONATE
  specific = 4
FEATURE [App::DocumentObjectGroupPython] Na_element015  label="Na_element : 1"  # scripted group (container) (typed FeaturePython)
  n = 1
  ref = Na_element
FEATURE [App::DocumentObjectGroupPython] I_element009  label="I_element : 005"  # scripted group (container) (typed FeaturePython)
  n = 1
  ref = I_element
FEATURE [App::DocumentObjectGroupPython] G4_SODIUM_IODIDE  # scripted group (container) (typed FeaturePython)
  Dunit = g/cm3
  Dvalue = 3.667
  Group = -> [Na_element015,I_element009]
  conduct = 2
  density = 1
  expand = 3
  formula = G4_SODIUM_IODIDE
  name = G4_SODIUM_IODIDE
  specific = 4
FEATURE [App::DocumentObjectGroupPython] Na_element016  label="Na_element : 003"  # scripted group (container) (typed FeaturePython)
  n = 2
  ref = Na_element
FEATURE [App::DocumentObjectGroupPython] O_element090  label="O_element : 050"  # scripted group (container) (typed FeaturePython)
  n = 1
  ref = O_element
FEATURE [App::DocumentObjectGroupPython] G4_SODIUM_MONOXIDE  # scripted group (container) (typed FeaturePython)
  Dunit = g/cm3
  Dvalue = 2.27
  Group = -> [Na_element016,O_element090]
  conduct = 2
  density = 1
  expand = 3
  formula = G4_SODIUM_MONOXIDE
  name = G4_SODIUM_MONOXIDE
  specific = 4
FEATURE [App::DocumentObjectGroupPython] Na_element017  label="Na_element : 004"  # scripted group (container) (typed FeaturePython)
  n = 1
  ref = Na_element
FEATURE [App::DocumentObjectGroupPython] N_element040  label="N_element : 018"  # scripted group (container) (typed FeaturePython)
  n = 1
  ref = N_element
FEATURE [App::DocumentObjectGroupPython] O_element091  label="O_element : 051"  # scripted group (container) (typed FeaturePython)
  n = 3
  ref = O_element
FEATURE [App::DocumentObjectGroupPython] G4_SODIUM_NITRATE  # scripted group (container) (typed FeaturePython)
  Dunit = g/cm3
  Dvalue = 2.261
  Group = -> [Na_element017,N_element040,O_element091]
  conduct = 2
  density = 1
  expand = 3
  formula = G4_SODIUM_NITRATE
  name = G4_SODIUM_NITRATE
  specific = 4
FEATURE [App::DocumentObjectGroupPython] C_element105  label="C_element : 059"  # scripted group (container) (typed FeaturePython)
  n = 14
  ref = C_element
FEATURE [App::DocumentObjectGroupPython] H_element096  label="H_element : 053"  # scripted group (container) (typed FeaturePython)
  n = 12
  ref = H_element
FEATURE [App::DocumentObjectGroupPython] G4_STILBENE  # scripted group (container) (typed FeaturePython)
  Dunit = g/cm3
  Dvalue = 0.9707
  Group = -> [C_element105,H_element096]
  conduct = 2
  density = 1
  expand = 3
  formula = G4_STILBENE
  name = G4_STILBENE
  specific = 4
FEATURE [App::DocumentObjectGroupPython] C_element106  label="C_element : 12"  # scripted group (container) (typed FeaturePython)
  n = 12
  ref = C_element
FEATURE [App::DocumentObjectGroupPython] H_element097  label="H_element : 22"  # scripted group (container) (typed FeaturePython)
  n = 22
  ref = H_element
FEATURE [App::DocumentObjectGroupPython] O_element092  label="O_element : 11"  # scripted group (container) (typed FeaturePython)
  n = 11
  ref = O_element
FEATURE [App::DocumentObjectGroupPython] G4_SUCROSE  # scripted group (container) (typed FeaturePython)
  Dunit = g/cm3
  Dvalue = 1.5805
  Group = -> [C_element106,H_element097,O_element092]
  conduct = 2
  density = 1
  expand = 3
  formula = G4_SUCROSE
  name = G4_SUCROSE
  specific = 4
FEATURE [App::DocumentObjectGroupPython] C_element107  label="C_element : 18"  # scripted group (container) (typed FeaturePython)
  n = 18
  ref = C_element
FEATURE [App::DocumentObjectGroupPython] H_element098  label="H_element : 054"  # scripted group (container) (typed FeaturePython)
  n = 14
  ref = H_element
FEATURE [App::DocumentObjectGroupPython] G4_TERPHENYL  # scripted group (container) (typed FeaturePython)
  Dunit = g/cm3
  Dvalue = 1.24
  Group = -> [C_element107,H_element098]
  conduct = 2
  density = 1
  expand = 3
  formula = G4_TERPHENYL
  name = G4_TERPHENYL
  specific = 4
FEATURE [App::DocumentObjectGroupPython] H_element099  label="H_element : 0.146"  # scripted group (container) (typed FeaturePython)
  n = 0.106
FEATURE [App::DocumentObjectGroupPython] C_element108  label="C_element : 0.883"  # scripted group (container) (typed FeaturePython)
  n = 0.099
FEATURE [App::DocumentObjectGroupPython] N_element041  label="N_element : 0.020"  # scripted group (container) (typed FeaturePython)
  n = 0.02
FEATURE [App::DocumentObjectGroupPython] O_element093  label="O_element : 0.766"  # scripted group (container) (typed FeaturePython)
  n = 0.766
FEATURE [App::DocumentObjectGroupPython] Na_element018  label="Na_element : 0.101"  # scripted group (container) (typed FeaturePython)
  n = 0.002
FEATURE [App::DocumentObjectGroupPython] P_element010  label="P_element : 0.108"  # scripted group (container) (typed FeaturePython)
  n = 0.001
FEATURE [App::DocumentObjectGroupPython] S_element021  label="S_element : 0.022"  # scripted group (container) (typed FeaturePython)
  n = 0.002
FEATURE [App::DocumentObjectGroupPython] Cl_element024  label="Cl_element : 0.002"  # scripted group (container) (typed FeaturePython)
  n = 0.002
FEATURE [App::DocumentObjectGroupPython] K_element011  label="K_element : 0.017"  # scripted group (container) (typed FeaturePython)
  n = 0.002
FEATURE [App::DocumentObjectGroupPython] G4_TESTIS_ICRP  # scripted group (container) (typed FeaturePython)
  Dunit = g/cm3
  Dvalue = 1.04
  Group = -> [H_element099,C_element108,N_element041,O_element093,Na_element018,P_element010,S_element021,Cl_element024,K_element011]
  conduct = 2
  density = 1
  expand = 3
  formula = G4_TESTIS_ICRP
  name = G4_TESTIS_ICRP
  specific = 4
FEATURE [App::DocumentObjectGroupPython] C_element109  label="C_element : 060"  # scripted group (container) (typed FeaturePython)
  n = 2
  ref = C_element
FEATURE [App::DocumentObjectGroupPython] Cl_element025  label="Cl_element : 012"  # scripted group (container) (typed FeaturePython)
  n = 4
  ref = Cl_element
FEATURE [App::DocumentObjectGroupPython] G4_TETRACHLOROETHYLENE  # scripted group (container) (typed FeaturePython)
  Dunit = g/cm3
  Dvalue = 1.625
  Group = -> [C_element109,Cl_element025]
  conduct = 2
  density = 1
  expand = 3
  formula = G4_TETRACHLOROETHYLENE
  name = G4_TETRACHLOROETHYLENE
  specific = 4
FEATURE [App::DocumentObjectGroupPython] Tl_element001  label="Tl_element : 1"  # scripted group (container) (typed FeaturePython)
  n = 1
  ref = Tl_element
FEATURE [App::DocumentObjectGroupPython] Cl_element026  label="Cl_element : 013"  # scripted group (container) (typed FeaturePython)
  n = 1
  ref = Cl_element
FEATURE [App::DocumentObjectGroupPython] G4_THALLIUM_CHLORIDE  # scripted group (container) (typed FeaturePython)
  Dunit = g/cm3
  Dvalue = 7.004
  Group = -> [Tl_element001,Cl_element026]
  conduct = 2
  density = 1
  expand = 3
  formula = G4_THALLIUM_CHLORIDE
  name = G4_THALLIUM_CHLORIDE
  specific = 4
FEATURE [App::DocumentObjectGroupPython] H_element100  label="H_element : 0.147"  # scripted group (container) (typed FeaturePython)
  n = 0.105
FEATURE [App::DocumentObjectGroupPython] C_element110  label="C_element : 0.256"  # scripted group (container) (typed FeaturePython)
  n = 0.256
FEATURE [App::DocumentObjectGroupPython] N_element042  label="N_element : 0.760"  # scripted group (container) (typed FeaturePython)
  n = 0.027
FEATURE [App::DocumentObjectGroupPython] O_element094  label="O_element : 0.602"  # scripted group (container) (typed FeaturePython)
  n = 0.602
FEATURE [App::DocumentObjectGroupPython] Na_element019  label="Na_element : 0.102"  # scripted group (container) (typed FeaturePython)
  n = 0.001
FEATURE [App::DocumentObjectGroupPython] P_element011  label="P_element : 0.109"  # scripted group (container) (typed FeaturePython)
  n = 0.002
FEATURE [App::DocumentObjectGroupPython] S_element022  label="S_element : 0.023"  # scripted group (container) (typed FeaturePython)
  n = 0.003
FEATURE [App::DocumentObjectGroupPython] Cl_element027  label="Cl_element : 0.591"  # scripted group (container) (typed FeaturePython)
  n = 0.002
FEATURE [App::DocumentObjectGroupPython] K_element012  label="K_element : 0.018"  # scripted group (container) (typed FeaturePython)
  n = 0.002
FEATURE [App::DocumentObjectGroupPython] G4_TISSUE_SOFT_ICRP  # scripted group (container) (typed FeaturePython)
  Dunit = g/cm3
  Dvalue = 1.03
  Group = -> [H_element100,C_element110,N_element042,O_element094,Na_element019,P_element011,S_element022,Cl_element027,K_element012]
  conduct = 2
  density = 1
  expand = 3
  formula = G4_TISSUE_SOFT_ICRP
  name = G4_TISSUE_SOFT_ICRP
  specific = 4
FEATURE [App::DocumentObjectGroupPython] H_element101  label="H_element : 0.148"  # scripted group (container) (typed FeaturePython)
  n = 0.101
FEATURE [App::DocumentObjectGroupPython] C_element111  label="C_element : 0.111"  # scripted group (container) (typed FeaturePython)
  n = 0.111
FEATURE [App::DocumentObjectGroupPython] N_element043  label="N_element : 0.026"  # scripted group (container) (typed FeaturePython)
  n = 0.026
FEATURE [App::DocumentObjectGroupPython] O_element095  label="O_element : 0.762"  # scripted group (container) (typed FeaturePython)
  n = 0.762
FEATURE [App::DocumentObjectGroupPython] G4_TISSUE_SOFT_ICRU_4  label="G4_TISSUE_SOFT_ICRU-4"  # scripted group (container) (typed FeaturePython)
  Dunit = g/cm3
  Dvalue = 1
  Group = -> [H_element101,C_element111,N_element043,O_element095]
  conduct = 2
  density = 1
  expand = 3
  formula = G4_TISSUE_SOFT_ICRU-4
  name = G4_TISSUE_SOFT_ICRU-4
  specific = 4
FEATURE [App::DocumentObjectGroupPython] H_element102  label="H_element : 0.149"  # scripted group (container) (typed FeaturePython)
  n = 0.101869
FEATURE [App::DocumentObjectGroupPython] C_element112  label="C_element : 0.456"  # scripted group (container) (typed FeaturePython)
  n = 0.456179
FEATURE [App::DocumentObjectGroupPython] N_element044  label="N_element : 0.761"  # scripted group (container) (typed FeaturePython)
  n = 0.035172
FEATURE [App::DocumentObjectGroupPython] O_element096  label="O_element : 0.407"  # scripted group (container) (typed FeaturePython)
  n = 0.40678
FEATURE [App::DocumentObjectGroupPython] G4_TISSUE_METHANE  label="G4_TISSUE-METHANE"  # scripted group (container) (typed FeaturePython)
  Dunit = g/cm3
  Dvalue = 0.00106409
  Group = -> [H_element102,C_element112,N_element044,O_element096]
  conduct = 2
  density = 1
  expand = 3
  formula = G4_TISSUE-METHANE
  name = G4_TISSUE-METHANE
  specific = 4
FEATURE [App::DocumentObjectGroupPython] H_element103  label="H_element : 0.103"  # scripted group (container) (typed FeaturePython)
  n = 0.102672
FEATURE [App::DocumentObjectGroupPython] C_element113  label="C_element : 0.569"  # scripted group (container) (typed FeaturePython)
  n = 0.56894
FEATURE [App::DocumentObjectGroupPython] N_element045  label="N_element : 0.762"  # scripted group (container) (typed FeaturePython)
  n = 0.035022
FEATURE [App::DocumentObjectGroupPython] O_element097  label="O_element : 0.293"  # scripted group (container) (typed FeaturePython)
  n = 0.293366
FEATURE [App::DocumentObjectGroupPython] G4_TISSUE_PROPANE  label="G4_TISSUE-PROPANE"  # scripted group (container) (typed FeaturePython)
  Dunit = g/cm3
  Dvalue = 0.00182628
  Group = -> [H_element103,C_element113,N_element045,O_element097]
  conduct = 2
  density = 1
  expand = 3
  formula = G4_TISSUE-PROPANE
  name = G4_TISSUE-PROPANE
  specific = 4
FEATURE [App::DocumentObjectGroupPython] Ti_element003  label="Ti_element : 1"  # scripted group (container) (typed FeaturePython)
  n = 1
  ref = Ti_element
FEATURE [App::DocumentObjectGroupPython] O_element098  label="O_element : 052"  # scripted group (container) (typed FeaturePython)
  n = 2
  ref = O_element
FEATURE [App::DocumentObjectGroupPython] G4_TITANIUM_DIOXIDE  # scripted group (container) (typed FeaturePython)
  Dunit = g/cm3
  Dvalue = 4.26
  Group = -> [Ti_element003,O_element098]
  conduct = 2
  density = 1
  expand = 3
  formula = G4_TITANIUM_DIOXIDE
  name = G4_TITANIUM_DIOXIDE
  specific = 4
FEATURE [App::DocumentObjectGroupPython] C_element114  label="C_element : 061"  # scripted group (container) (typed FeaturePython)
  n = 7
  ref = C_element
FEATURE [App::DocumentObjectGroupPython] H_element104  label="H_element : 055"  # scripted group (container) (typed FeaturePython)
  n = 8
  ref = H_element
FEATURE [App::DocumentObjectGroupPython] G4_TOLUENE  # scripted group (container) (typed FeaturePython)
  Dunit = g/cm3
  Dvalue = 0.8669
  Group = -> [C_element114,H_element104]
  conduct = 2
  density = 1
  expand = 3
  formula = G4_TOLUENE
  name = G4_TOLUENE
  specific = 4
FEATURE [App::DocumentObjectGroupPython] C_element115  label="C_element : 062"  # scripted group (container) (typed FeaturePython)
  n = 2
  ref = C_element
FEATURE [App::DocumentObjectGroupPython] H_element105  label="H_element : 056"  # scripted group (container) (typed FeaturePython)
  n = 1
  ref = H_element
FEATURE [App::DocumentObjectGroupPython] Cl_element028  label="Cl_element : 014"  # scripted group (container) (typed FeaturePython)
  n = 3
  ref = Cl_element
FEATURE [App::DocumentObjectGroupPython] G4_TRICHLOROETHYLENE  # scripted group (container) (typed FeaturePython)
  Dunit = g/cm3
  Dvalue = 1.46
  Group = -> [C_element115,H_element105,Cl_element028]
  conduct = 2
  density = 1
  expand = 3
  formula = G4_TRICHLOROETHYLENE
  name = G4_TRICHLOROETHYLENE
  specific = 4
FEATURE [App::DocumentObjectGroupPython] C_element116  label="C_element : 063"  # scripted group (container) (typed FeaturePython)
  n = 6
  ref = C_element
FEATURE [App::DocumentObjectGroupPython] H_element106  label="H_element : 15"  # scripted group (container) (typed FeaturePython)
  n = 15
  ref = H_element
FEATURE [App::DocumentObjectGroupPython] O_element099  label="O_element : 053"  # scripted group (container) (typed FeaturePython)
  n = 4
  ref = O_element
FEATURE [App::DocumentObjectGroupPython] P_element012  label="P_element : 1"  # scripted group (container) (typed FeaturePython)
  n = 1
  ref = P_element
FEATURE [App::DocumentObjectGroupPython] G4_TRIETHYL_PHOSPHATE  # scripted group (container) (typed FeaturePython)
  Dunit = g/cm3
  Dvalue = 1.07
  Group = -> [C_element116,H_element106,O_element099,P_element012]
  conduct = 2
  density = 1
  expand = 3
  formula = G4_TRIETHYL_PHOSPHATE
  name = G4_TRIETHYL_PHOSPHATE
  specific = 4
FEATURE [App::DocumentObjectGroupPython] W_element003  label="W_element : 003"  # scripted group (container) (typed FeaturePython)
  n = 1
  ref = W_element
FEATURE [App::DocumentObjectGroupPython] F_element017  label="F_element : 6"  # scripted group (container) (typed FeaturePython)
  n = 6
  ref = F_element
FEATURE [App::DocumentObjectGroupPython] G4_TUNGSTEN_HEXAFLUORIDE  # scripted group (container) (typed FeaturePython)
  Dunit = g/cm3
  Dvalue = 2.4
  Group = -> [W_element003,F_element017]
  conduct = 2
  density = 1
  expand = 3
  formula = G4_TUNGSTEN_HEXAFLUORIDE
  name = G4_TUNGSTEN_HEXAFLUORIDE
  specific = 4
FEATURE [App::DocumentObjectGroupPython] U_element001  label="U_element : 1"  # scripted group (container) (typed FeaturePython)
  n = 1
  ref = U_element
FEATURE [App::DocumentObjectGroupPython] C_element117  label="C_element : 064"  # scripted group (container) (typed FeaturePython)
  n = 2
  ref = C_element
FEATURE [App::DocumentObjectGroupPython] G4_URANIUM_DICARBIDE  # scripted group (container) (typed FeaturePython)
  Dunit = g/cm3
  Dvalue = 11.28
  Group = -> [U_element001,C_element117]
  conduct = 2
  density = 1
  expand = 3
  formula = G4_URANIUM_DICARBIDE
  name = G4_URANIUM_DICARBIDE
  specific = 4
FEATURE [App::DocumentObjectGroupPython] U_element002  label="U_element : 002"  # scripted group (container) (typed FeaturePython)
  n = 1
  ref = U_element
FEATURE [App::DocumentObjectGroupPython] C_element118  label="C_element : 065"  # scripted group (container) (typed FeaturePython)
  n = 1
  ref = C_element
FEATURE [App::DocumentObjectGroupPython] G4_URANIUM_MONOCARBIDE  # scripted group (container) (typed FeaturePython)
  Dunit = g/cm3
  Dvalue = 13.63
  Group = -> [U_element002,C_element118]
  conduct = 2
  density = 1
  expand = 3
  formula = G4_URANIUM_MONOCARBIDE
  name = G4_URANIUM_MONOCARBIDE
  specific = 4
FEATURE [App::DocumentObjectGroupPython] U_element003  label="U_element : 003"  # scripted group (container) (typed FeaturePython)
  n = 1
  ref = U_element
FEATURE [App::DocumentObjectGroupPython] O_element100  label="O_element : 054"  # scripted group (container) (typed FeaturePython)
  n = 2
  ref = O_element
FEATURE [App::DocumentObjectGroupPython] G4_URANIUM_OXIDE  # scripted group (container) (typed FeaturePython)
  Dunit = g/cm3
  Dvalue = 10.96
  Group = -> [U_element003,O_element100]
  conduct = 2
  density = 1
  expand = 3
  formula = G4_URANIUM_OXIDE
  name = G4_URANIUM_OXIDE
  specific = 4
FEATURE [App::DocumentObjectGroupPython] C_element119  label="C_element : 066"  # scripted group (container) (typed FeaturePython)
  n = 1
  ref = C_element
FEATURE [App::DocumentObjectGroupPython] H_element107  label="H_element : 057"  # scripted group (container) (typed FeaturePython)
  n = 4
  ref = H_element
FEATURE [App::DocumentObjectGroupPython] N_element046  label="N_element : 019"  # scripted group (container) (typed FeaturePython)
  n = 2
  ref = N_element
FEATURE [App::DocumentObjectGroupPython] O_element101  label="O_element : 055"  # scripted group (container) (typed FeaturePython)
  n = 1
  ref = O_element
FEATURE [App::DocumentObjectGroupPython] G4_UREA  # scripted group (container) (typed FeaturePython)
  Dunit = g/cm3
  Dvalue = 1.323
  Group = -> [C_element119,H_element107,N_element046,O_element101]
  conduct = 2
  density = 1
  expand = 3
  formula = G4_UREA
  name = G4_UREA
  specific = 4
FEATURE [App::DocumentObjectGroupPython] C_element120  label="C_element : 067"  # scripted group (container) (typed FeaturePython)
  n = 5
  ref = C_element
FEATURE [App::DocumentObjectGroupPython] H_element108  label="H_element : 058"  # scripted group (container) (typed FeaturePython)
  n = 11
  ref = H_element
FEATURE [App::DocumentObjectGroupPython] N_element047  label="N_element : 020"  # scripted group (container) (typed FeaturePython)
  n = 1
  ref = N_element
FEATURE [App::DocumentObjectGroupPython] O_element102  label="O_element : 056"  # scripted group (container) (typed FeaturePython)
  n = 2
  ref = O_element
FEATURE [App::DocumentObjectGroupPython] G4_VALINE  # scripted group (container) (typed FeaturePython)
  Dunit = g/cm3
  Dvalue = 1.23
  Group = -> [C_element120,H_element108,N_element047,O_element102]
  conduct = 2
  density = 1
  expand = 3
  formula = G4_VALINE
  name = G4_VALINE
  specific = 4
FEATURE [App::DocumentObjectGroupPython] H_element109  label="H_element : 0.009"  # scripted group (container) (typed FeaturePython)
  n = 0.009417
FEATURE [App::DocumentObjectGroupPython] C_element121  label="C_element : 0.281"  # scripted group (container) (typed FeaturePython)
  n = 0.280555
FEATURE [App::DocumentObjectGroupPython] F_element018  label="F_element : 0.710"  # scripted group (container) (typed FeaturePython)
  n = 0.710028
FEATURE [App::DocumentObjectGroupPython] G4_VITON  # scripted group (container) (typed FeaturePython)
  Dunit = g/cm3
  Dvalue = 1.8
  Group = -> [H_element109,C_element121,F_element018]
  conduct = 2
  density = 1
  expand = 3
  formula = G4_VITON
  name = G4_VITON
  specific = 4
FEATURE [App::DocumentObjectGroupPython] H_element110  label="H_element : 059"  # scripted group (container) (typed FeaturePython)
  n = 2
  ref = H_element
FEATURE [App::DocumentObjectGroupPython] O_element103  label="O_element : 057"  # scripted group (container) (typed FeaturePython)
  n = 1
  ref = O_element
FEATURE [App::DocumentObjectGroupPython] G4_WATER  # scripted group (container) (typed FeaturePython)
  Dunit = g/cm3
  Dvalue = 1
  Group = -> [H_element110,O_element103]
  conduct = 2
  density = 1
  expand = 3
  formula = G4_WATER
  name = G4_WATER
  specific = 4
FEATURE [App::DocumentObjectGroupPython] H_element111  label="H_element : 060"  # scripted group (container) (typed FeaturePython)
  n = 2
  ref = H_element
FEATURE [App::DocumentObjectGroupPython] O_element104  label="O_element : 058"  # scripted group (container) (typed FeaturePython)
  n = 1
  ref = O_element
FEATURE [App::DocumentObjectGroupPython] G4_WATER_VAPOR  # scripted group (container) (typed FeaturePython)
  Dunit = g/cm3
  Dvalue = 0.000756182
  Group = -> [H_element111,O_element104]
  conduct = 2
  density = 1
  expand = 3
  formula = G4_WATER_VAPOR
  name = G4_WATER_VAPOR
  specific = 4
FEATURE [App::DocumentObjectGroupPython] C_element122  label="C_element : 068"  # scripted group (container) (typed FeaturePython)
  n = 8
  ref = C_element
FEATURE [App::DocumentObjectGroupPython] H_element112  label="H_element : 061"  # scripted group (container) (typed FeaturePython)
  n = 10
  ref = H_element
FEATURE [App::DocumentObjectGroupPython] G4_XYLENE  # scripted group (container) (typed FeaturePython)
  Dunit = g/cm3
  Dvalue = 0.87
  Group = -> [C_element122,H_element112]
  conduct = 2
  density = 1
  expand = 3
  formula = G4_XYLENE
  name = G4_XYLENE
  specific = 4
FEATURE [App::DocumentObjectGroupPython] C_element123  label="C_element : 069"  # scripted group (container) (typed FeaturePython)
  n = 1
  ref = C_element
FEATURE [App::DocumentObjectGroupPython] G4_GRAPHITE  # scripted group (container) (typed FeaturePython)
  Dunit = g/cm3
  Dvalue = 2.21
  Group = -> [C_element123]
  conduct = 2
  density = 1
  expand = 3
  formula = G4_GRAPHITE
  name = G4_GRAPHITE
  specific = 4
FEATURE [App::DocumentObjectGroupPython] NIST  # scripted group (container) (typed FeaturePython)
  Group = -> [G4_A_150_TISSUE,G4_ACETONE,G4_ACETYLENE,G4_ADENINE,G4_ADIPOSE_TISSUE_ICRP,G4_AIR,G4_ALANINE,G4_ALUMINUM_OXIDE,G4_AMBER,G4_AMMONIA,G4_ANILINE,G4_ANTHRACENE,G4_B_100_BONE,G4_BAKELITE,G4_BARIUM_FLUORIDE,G4_BARIUM_SULFATE,G4_BENZENE,G4_BERYLLIUM_OXIDE,G4_BGO,G4_BLOOD_ICRP,G4_BONE_COMPACT_ICRU,G4_BONE_CORTICAL_ICRP,G4_BORON_CARBIDE,G4_BORON_OXIDE,G4_BRAIN_ICRP,G4_BUTANE,G4_N_BUTYL_ALCOHOL,G4_C_552,+152 more]
FEATURE [App::DocumentObjectGroupPython] H_element113  label="H_element : 062"  # scripted group (container) (typed FeaturePython)
  n = 1
  ref = H_element
FEATURE [App::DocumentObjectGroupPython] G4_H  # scripted group (container) (typed FeaturePython)
  Dunit = g/cm3
  Dvalue = 8.3748e-05
  Group = -> [H_element113]
  conduct = 2
  density = 1
  expand = 3
  formula = H
  name = G4_H
  specific = 4
FEATURE [App::DocumentObjectGroupPython] He_element001  label="He_element : 1"  # scripted group (container) (typed FeaturePython)
  n = 1
  ref = He_element
FEATURE [App::DocumentObjectGroupPython] G4_He  # scripted group (container) (typed FeaturePython)
  Dunit = g/cm3
  Dvalue = 0.000166322
  Group = -> [He_element001]
  conduct = 2
  density = 1
  expand = 3
  formula = He
  name = G4_He
  specific = 4
FEATURE [App::DocumentObjectGroupPython] Li_element008  label="Li_element : 008"  # scripted group (container) (typed FeaturePython)
  n = 1
  ref = Li_element
FEATURE [App::DocumentObjectGroupPython] G4_Li  # scripted group (container) (typed FeaturePython)
  Dunit = g/cm3
  Dvalue = 0.534
  Group = -> [Li_element008]
  conduct = 2
  density = 1
  expand = 3
  formula = Li
  name = G4_Li
  specific = 4
FEATURE [App::DocumentObjectGroupPython] Be_element002  label="Be_element : 002"  # scripted group (container) (typed FeaturePython)
  n = 1
  ref = Be_element
FEATURE [App::DocumentObjectGroupPython] G4_Be  # scripted group (container) (typed FeaturePython)
  Dunit = g/cm3
  Dvalue = 1.848
  Group = -> [Be_element002]
  conduct = 2
  density = 1
  expand = 3
  formula = Be
  name = G4_Be
  specific = 4
FEATURE [App::DocumentObjectGroupPython] B_element007  label="B_element : 007"  # scripted group (container) (typed FeaturePython)
  n = 1
  ref = B_element
FEATURE [App::DocumentObjectGroupPython] G4_B  # scripted group (container) (typed FeaturePython)
  Dunit = g/cm3
  Dvalue = 2.37
  Group = -> [B_element007]
  conduct = 2
  density = 1
  expand = 3
  formula = B
  name = G4_B
  specific = 4
FEATURE [App::DocumentObjectGroupPython] C_element124  label="C_element : 070"  # scripted group (container) (typed FeaturePython)
  n = 1
  ref = C_element
FEATURE [App::DocumentObjectGroupPython] G4_C  # scripted group (container) (typed FeaturePython)
  Dunit = g/cm3
  Dvalue = 2
  Group = -> [C_element124]
  conduct = 2
  density = 1
  expand = 3
  formula = C
  name = G4_C
  specific = 4
FEATURE [App::DocumentObjectGroupPython] N_element048  label="N_element : 021"  # scripted group (container) (typed FeaturePython)
  n = 1
  ref = N_element
FEATURE [App::DocumentObjectGroupPython] G4_N  # scripted group (container) (typed FeaturePython)
  Dunit = g/cm3
  Dvalue = 0.0011652
  Group = -> [N_element048]
  conduct = 2
  density = 1
  expand = 3
  formula = N
  name = G4_N
  specific = 4
FEATURE [App::DocumentObjectGroupPython] O_element105  label="O_element : 059"  # scripted group (container) (typed FeaturePython)
  n = 1
  ref = O_element
FEATURE [App::DocumentObjectGroupPython] G4_O  # scripted group (container) (typed FeaturePython)
  Dunit = g/cm3
  Dvalue = 0.00133151
  Group = -> [O_element105]
  conduct = 2
  density = 1
  expand = 3
  formula = O
  name = G4_O
  specific = 4
FEATURE [App::DocumentObjectGroupPython] F_element019  label="F_element : 008"  # scripted group (container) (typed FeaturePython)
  n = 1
  ref = F_element
FEATURE [App::DocumentObjectGroupPython] G4_F  # scripted group (container) (typed FeaturePython)
  Dunit = g/cm3
  Dvalue = 0.00158029
  Group = -> [F_element019]
  conduct = 2
  density = 1
  expand = 3
  formula = F
  name = G4_F
  specific = 4
FEATURE [App::DocumentObjectGroupPython] Ne_element001  label="Ne_element : 1"  # scripted group (container) (typed FeaturePython)
  n = 1
  ref = Ne_element
FEATURE [App::DocumentObjectGroupPython] G4_Ne  # scripted group (container) (typed FeaturePython)
  Dunit = g/cm3
  Dvalue = 0.000838505
  Group = -> [Ne_element001]
  conduct = 2
  density = 1
  expand = 3
  formula = Ne
  name = G4_Ne
  specific = 4
FEATURE [App::DocumentObjectGroupPython] Na_element020  label="Na_element : 005"  # scripted group (container) (typed FeaturePython)
  n = 1
  ref = Na_element
FEATURE [App::DocumentObjectGroupPython] G4_Na  # scripted group (container) (typed FeaturePython)
  Dunit = g/cm3
  Dvalue = 0.971
  Group = -> [Na_element020]
  conduct = 2
  density = 1
  expand = 3
  formula = Na
  name = G4_Na
  specific = 4
FEATURE [App::DocumentObjectGroupPython] Mg_element011  label="Mg_element : 005"  # scripted group (container) (typed FeaturePython)
  n = 1
  ref = Mg_element
FEATURE [App::DocumentObjectGroupPython] G4_Mg  # scripted group (container) (typed FeaturePython)
  Dunit = g/cm3
  Dvalue = 1.74
  Group = -> [Mg_element011]
  conduct = 2
  density = 1
  expand = 3
  formula = Mg
  name = G4_Mg
  specific = 4
FEATURE [App::DocumentObjectGroupPython] Al_element004  label="Al_element : 1"  # scripted group (container) (typed FeaturePython)
  n = 1
  ref = Al_element
FEATURE [App::DocumentObjectGroupPython] G4_Al  # scripted group (container) (typed FeaturePython)
  Dunit = g/cm3
  Dvalue = 2.699
  Group = -> [Al_element004]
  conduct = 2
  density = 1
  expand = 3
  formula = Al
  name = G4_Al
  specific = 4
FEATURE [App::DocumentObjectGroupPython] Si_element007  label="Si_element : 002"  # scripted group (container) (typed FeaturePython)
  n = 1
  ref = Si_element
FEATURE [App::DocumentObjectGroupPython] G4_Si  # scripted group (container) (typed FeaturePython)
  Dunit = g/cm3
  Dvalue = 2.33
  Group = -> [Si_element007]
  conduct = 2
  density = 1
  expand = 3
  formula = Si
  name = G4_Si
  specific = 4
FEATURE [App::DocumentObjectGroupPython] P_element013  label="P_element : 002"  # scripted group (container) (typed FeaturePython)
  n = 1
  ref = P_element
FEATURE [App::DocumentObjectGroupPython] G4_P  # scripted group (container) (typed FeaturePython)
  Dunit = g/cm3
  Dvalue = 2.2
  Group = -> [P_element013]
  conduct = 2
  density = 1
  expand = 3
  formula = P
  name = G4_P
  specific = 4
FEATURE [App::DocumentObjectGroupPython] S_element023  label="S_element : 007"  # scripted group (container) (typed FeaturePython)
  n = 1
  ref = S_element
FEATURE [App::DocumentObjectGroupPython] G4_S  # scripted group (container) (typed FeaturePython)
  Dunit = g/cm3
  Dvalue = 2
  Group = -> [S_element023]
  conduct = 2
  density = 1
  expand = 3
  formula = S
  name = G4_S
  specific = 4
FEATURE [App::DocumentObjectGroupPython] Cl_element029  label="Cl_element : 015"  # scripted group (container) (typed FeaturePython)
  n = 1
  ref = Cl_element
FEATURE [App::DocumentObjectGroupPython] G4_Cl  # scripted group (container) (typed FeaturePython)
  Dunit = g/cm3
  Dvalue = 0.00299473
  Group = -> [Cl_element029]
  conduct = 2
  density = 1
  expand = 3
  formula = Cl
  name = G4_Cl
  specific = 4
FEATURE [App::DocumentObjectGroupPython] Ar_element002  label="Ar_element : 1"  # scripted group (container) (typed FeaturePython)
  n = 1
  ref = Ar_element
FEATURE [App::DocumentObjectGroupPython] G4_Ar  # scripted group (container) (typed FeaturePython)
  Dunit = g/cm3
  Dvalue = 0.00166201
  Group = -> [Ar_element002]
  conduct = 2
  density = 1
  expand = 3
  formula = Ar
  name = G4_Ar
  specific = 4
FEATURE [App::DocumentObjectGroupPython] K_element013  label="K_element : 003"  # scripted group (container) (typed FeaturePython)
  n = 1
  ref = K_element
FEATURE [App::DocumentObjectGroupPython] G4_K  # scripted group (container) (typed FeaturePython)
  Dunit = g/cm3
  Dvalue = 0.862
  Group = -> [K_element013]
  conduct = 2
  density = 1
  expand = 3
  formula = K
  name = G4_K
  specific = 4
FEATURE [App::DocumentObjectGroupPython] Ca_element014  label="Ca_element : 007"  # scripted group (container) (typed FeaturePython)
  n = 1
  ref = Ca_element
FEATURE [App::DocumentObjectGroupPython] G4_Ca  # scripted group (container) (typed FeaturePython)
  Dunit = g/cm3
  Dvalue = 1.55
  Group = -> [Ca_element014]
  conduct = 2
  density = 1
  expand = 3
  formula = Ca
  name = G4_Ca
  specific = 4
FEATURE [App::DocumentObjectGroupPython] Sc_element001  label="Sc_element : 1"  # scripted group (container) (typed FeaturePython)
  n = 1
  ref = Sc_element
FEATURE [App::DocumentObjectGroupPython] G4_Sc  # scripted group (container) (typed FeaturePython)
  Dunit = g/cm3
  Dvalue = 2.989
  Group = -> [Sc_element001]
  conduct = 2
  density = 1
  expand = 3
  formula = Sc
  name = G4_Sc
  specific = 4
FEATURE [App::DocumentObjectGroupPython] Ti_element004  label="Ti_element : 002"  # scripted group (container) (typed FeaturePython)
  n = 1
  ref = Ti_element
FEATURE [App::DocumentObjectGroupPython] G4_Ti  # scripted group (container) (typed FeaturePython)
  Dunit = g/cm3
  Dvalue = 4.54
  Group = -> [Ti_element004]
  conduct = 2
  density = 1
  expand = 3
  formula = Ti
  name = G4_Ti
  specific = 4
FEATURE [App::DocumentObjectGroupPython] V_element001  label="V_element : 1"  # scripted group (container) (typed FeaturePython)
  n = 1
  ref = V_element
FEATURE [App::DocumentObjectGroupPython] G4_V  # scripted group (container) (typed FeaturePython)
  Dunit = g/cm3
  Dvalue = 6.11
  Group = -> [V_element001]
  conduct = 2
  density = 1
  expand = 3
  formula = V
  name = G4_V
  specific = 4
FEATURE [App::DocumentObjectGroupPython] Cr_element001  label="Cr_element : 1"  # scripted group (container) (typed FeaturePython)
  n = 1
  ref = Cr_element
FEATURE [App::DocumentObjectGroupPython] G4_Cr  # scripted group (container) (typed FeaturePython)
  Dunit = g/cm3
  Dvalue = 7.18
  Group = -> [Cr_element001]
  conduct = 2
  density = 1
  expand = 3
  formula = Cr
  name = G4_Cr
  specific = 4
FEATURE [App::DocumentObjectGroupPython] Mn_element001  label="Mn_element : 1"  # scripted group (container) (typed FeaturePython)
  n = 1
  ref = Mn_element
FEATURE [App::DocumentObjectGroupPython] G4_Mn  # scripted group (container) (typed FeaturePython)
  Dunit = g/cm3
  Dvalue = 7.44
  Group = -> [Mn_element001]
  conduct = 2
  density = 1
  expand = 3
  formula = Mn
  name = G4_Mn
  specific = 4
FEATURE [App::DocumentObjectGroupPython] Fe_element007  label="Fe_element : 004"  # scripted group (container) (typed FeaturePython)
  n = 1
  ref = Fe_element
FEATURE [App::DocumentObjectGroupPython] G4_Fe  # scripted group (container) (typed FeaturePython)
  Dunit = g/cm3
  Dvalue = 7.874
  Group = -> [Fe_element007]
  conduct = 2
  density = 1
  expand = 3
  formula = Fe
  name = G4_Fe
  specific = 4
FEATURE [App::DocumentObjectGroupPython] Co_element001  label="Co_element : 1"  # scripted group (container) (typed FeaturePython)
  n = 1
  ref = Co_element
FEATURE [App::DocumentObjectGroupPython] G4_Co  # scripted group (container) (typed FeaturePython)
  Dunit = g/cm3
  Dvalue = 8.9
  Group = -> [Co_element001]
  conduct = 2
  density = 1
  expand = 3
  formula = Co
  name = G4_Co
  specific = 4
FEATURE [App::DocumentObjectGroupPython] Ni_element001  label="Ni_element : 1"  # scripted group (container) (typed FeaturePython)
  n = 1
  ref = Ni_element
FEATURE [App::DocumentObjectGroupPython] G4_Ni  # scripted group (container) (typed FeaturePython)
  Dunit = g/cm3
  Dvalue = 8.902
  Group = -> [Ni_element001]
  conduct = 2
  density = 1
  expand = 3
  formula = Ni
  name = G4_Ni
  specific = 4
FEATURE [App::DocumentObjectGroupPython] Cu_element001  label="Cu_element : 1"  # scripted group (container) (typed FeaturePython)
  n = 1
  ref = Cu_element
FEATURE [App::DocumentObjectGroupPython] G4_Cu  # scripted group (container) (typed FeaturePython)
  Dunit = g/cm3
  Dvalue = 8.96
  Group = -> [Cu_element001]
  conduct = 2
  density = 1
  expand = 3
  formula = Cu
  name = G4_Cu
  specific = 4
FEATURE [App::DocumentObjectGroupPython] Zn_element001  label="Zn_element : 1"  # scripted group (container) (typed FeaturePython)
  n = 1
  ref = Zn_element
FEATURE [App::DocumentObjectGroupPython] G4_Zn  # scripted group (container) (typed FeaturePython)
  Dunit = g/cm3
  Dvalue = 7.133
  Group = -> [Zn_element001]
  conduct = 2
  density = 1
  expand = 3
  formula = Zn
  name = G4_Zn
  specific = 4
FEATURE [App::DocumentObjectGroupPython] Ga_element002  label="Ga_element : 002"  # scripted group (container) (typed FeaturePython)
  n = 1
  ref = Ga_element
FEATURE [App::DocumentObjectGroupPython] G4_Ga  # scripted group (container) (typed FeaturePython)
  Dunit = g/cm3
  Dvalue = 5.904
  Group = -> [Ga_element002]
  conduct = 2
  density = 1
  expand = 3
  formula = Ga
  name = G4_Ga
  specific = 4
FEATURE [App::DocumentObjectGroupPython] Ge_element002  label="Ge_element : 1"  # scripted group (container) (typed FeaturePython)
  n = 1
  ref = Ge_element
FEATURE [App::DocumentObjectGroupPython] G4_Ge  # scripted group (container) (typed FeaturePython)
  Dunit = g/cm3
  Dvalue = 5.323
  Group = -> [Ge_element002]
  conduct = 2
  density = 1
  expand = 3
  formula = Ge
  name = G4_Ge
  specific = 4
FEATURE [App::DocumentObjectGroupPython] As_element003  label="As_element : 002"  # scripted group (container) (typed FeaturePython)
  n = 1
  ref = As_element
FEATURE [App::DocumentObjectGroupPython] G4_As  # scripted group (container) (typed FeaturePython)
  Dunit = g/cm3
  Dvalue = 5.73
  Group = -> [As_element003]
  conduct = 2
  density = 1
  expand = 3
  formula = As
  name = G4_As
  specific = 4
FEATURE [App::DocumentObjectGroupPython] Se_element001  label="Se_element : 1"  # scripted group (container) (typed FeaturePython)
  n = 1
  ref = Se_element
FEATURE [App::DocumentObjectGroupPython] G4_Se  # scripted group (container) (typed FeaturePython)
  Dunit = g/cm3
  Dvalue = 4.5
  Group = -> [Se_element001]
  conduct = 2
  density = 1
  expand = 3
  formula = Se
  name = G4_Se
  specific = 4
FEATURE [App::DocumentObjectGroupPython] Br_element007  label="Br_element : 004"  # scripted group (container) (typed FeaturePython)
  n = 1
  ref = Br_element
FEATURE [App::DocumentObjectGroupPython] G4_Br  # scripted group (container) (typed FeaturePython)
  Dunit = g/cm3
  Dvalue = 0.0070721
  Group = -> [Br_element007]
  conduct = 2
  density = 1
  expand = 3
  formula = Br
  name = G4_Br
  specific = 4
FEATURE [App::DocumentObjectGroupPython] Kr_element001  label="Kr_element : 1"  # scripted group (container) (typed FeaturePython)
  n = 1
  ref = Kr_element
FEATURE [App::DocumentObjectGroupPython] G4_Kr  # scripted group (container) (typed FeaturePython)
  Dunit = g/cm3
  Dvalue = 0.00347832
  Group = -> [Kr_element001]
  conduct = 2
  density = 1
  expand = 3
  formula = Kr
  name = G4_Kr
  specific = 4
FEATURE [App::DocumentObjectGroupPython] Rb_element001  label="Rb_element : 1"  # scripted group (container) (typed FeaturePython)
  n = 1
  ref = Rb_element
FEATURE [App::DocumentObjectGroupPython] G4_Rb  # scripted group (container) (typed FeaturePython)
  Dunit = g/cm3
  Dvalue = 1.532
  Group = -> [Rb_element001]
  conduct = 2
  density = 1
  expand = 3
  formula = Rb
  name = G4_Rb
  specific = 4
FEATURE [App::DocumentObjectGroupPython] Sr_element001  label="Sr_element : 1"  # scripted group (container) (typed FeaturePython)
  n = 1
  ref = Sr_element
FEATURE [App::DocumentObjectGroupPython] G4_Sr  # scripted group (container) (typed FeaturePython)
  Dunit = g/cm3
  Dvalue = 2.54
  Group = -> [Sr_element001]
  conduct = 2
  density = 1
  expand = 3
  formula = Sr
  name = G4_Sr
  specific = 4
FEATURE [App::DocumentObjectGroupPython] Y_element001  label="Y_element : 1"  # scripted group (container) (typed FeaturePython)
  n = 1
  ref = Y_element
FEATURE [App::DocumentObjectGroupPython] G4_Y  # scripted group (container) (typed FeaturePython)
  Dunit = g/cm3
  Dvalue = 4.469
  Group = -> [Y_element001]
  conduct = 2
  density = 1
  expand = 3
  formula = Y
  name = G4_Y
  specific = 4
FEATURE [App::DocumentObjectGroupPython] Zr_element001  label="Zr_element : 1"  # scripted group (container) (typed FeaturePython)
  n = 1
  ref = Zr_element
FEATURE [App::DocumentObjectGroupPython] G4_Zr  # scripted group (container) (typed FeaturePython)
  Dunit = g/cm3
  Dvalue = 6.506
  Group = -> [Zr_element001]
  conduct = 2
  density = 1
  expand = 3
  formula = Zr
  name = G4_Zr
  specific = 4
FEATURE [App::DocumentObjectGroupPython] Nb_element001  label="Nb_element : 1"  # scripted group (container) (typed FeaturePython)
  n = 1
  ref = Nb_element
FEATURE [App::DocumentObjectGroupPython] G4_Nb  # scripted group (container) (typed FeaturePython)
  Dunit = g/cm3
  Dvalue = 8.57
  Group = -> [Nb_element001]
  conduct = 2
  density = 1
  expand = 3
  formula = Nb
  name = G4_Nb
  specific = 4
FEATURE [App::DocumentObjectGroupPython] Mo_element001  label="Mo_element : 1"  # scripted group (container) (typed FeaturePython)
  n = 1
  ref = Mo_element
FEATURE [App::DocumentObjectGroupPython] G4_Mo  # scripted group (container) (typed FeaturePython)
  Dunit = g/cm3
  Dvalue = 10.22
  Group = -> [Mo_element001]
  conduct = 2
  density = 1
  expand = 3
  formula = Mo
  name = G4_Mo
  specific = 4
FEATURE [App::DocumentObjectGroupPython] Tc_element001  label="Tc_element : 1"  # scripted group (container) (typed FeaturePython)
  n = 1
  ref = Tc_element
FEATURE [App::DocumentObjectGroupPython] G4_Tc  # scripted group (container) (typed FeaturePython)
  Dunit = g/cm3
  Dvalue = 11.5
  Group = -> [Tc_element001]
  conduct = 2
  density = 1
  expand = 3
  formula = Tc
  name = G4_Tc
  specific = 4
FEATURE [App::DocumentObjectGroupPython] Ru_element001  label="Ru_element : 1"  # scripted group (container) (typed FeaturePython)
  n = 1
  ref = Ru_element
FEATURE [App::DocumentObjectGroupPython] G4_Ru  # scripted group (container) (typed FeaturePython)
  Dunit = g/cm3
  Dvalue = 12.41
  Group = -> [Ru_element001]
  conduct = 2
  density = 1
  expand = 3
  formula = Ru
  name = G4_Ru
  specific = 4
FEATURE [App::DocumentObjectGroupPython] Rh_element001  label="Rh_element : 1"  # scripted group (container) (typed FeaturePython)
  n = 1
  ref = Rh_element
FEATURE [App::DocumentObjectGroupPython] G4_Rh  # scripted group (container) (typed FeaturePython)
  Dunit = g/cm3
  Dvalue = 12.41
  Group = -> [Rh_element001]
  conduct = 2
  density = 1
  expand = 3
  formula = Rh
  name = G4_Rh
  specific = 4
FEATURE [App::DocumentObjectGroupPython] Pd_element001  label="Pd_element : 1"  # scripted group (container) (typed FeaturePython)
  n = 1
  ref = Pd_element
FEATURE [App::DocumentObjectGroupPython] G4_Pd  # scripted group (container) (typed FeaturePython)
  Dunit = g/cm3
  Dvalue = 12.02
  Group = -> [Pd_element001]
  conduct = 2
  density = 1
  expand = 3
  formula = Pd
  name = G4_Pd
  specific = 4
FEATURE [App::DocumentObjectGroupPython] Ag_element006  label="Ag_element : 004"  # scripted group (container) (typed FeaturePython)
  n = 1
  ref = Ag_element
FEATURE [App::DocumentObjectGroupPython] G4_Ag  # scripted group (container) (typed FeaturePython)
  Dunit = g/cm3
  Dvalue = 10.5
  Group = -> [Ag_element006]
  conduct = 2
  density = 1
  expand = 3
  formula = Ag
  name = G4_Ag
  specific = 4
FEATURE [App::DocumentObjectGroupPython] Cd_element003  label="Cd_element : 003"  # scripted group (container) (typed FeaturePython)
  n = 1
  ref = Cd_element
FEATURE [App::DocumentObjectGroupPython] G4_Cd  # scripted group (container) (typed FeaturePython)
  Dunit = g/cm3
  Dvalue = 8.65
  Group = -> [Cd_element003]
  conduct = 2
  density = 1
  expand = 3
  formula = Cd
  name = G4_Cd
  specific = 4
FEATURE [App::DocumentObjectGroupPython] In_element001  label="In_element : 1"  # scripted group (container) (typed FeaturePython)
  n = 1
  ref = In_element
FEATURE [App::DocumentObjectGroupPython] G4_In  # scripted group (container) (typed FeaturePython)
  Dunit = g/cm3
  Dvalue = 7.31
  Group = -> [In_element001]
  conduct = 2
  density = 1
  expand = 3
  formula = In
  name = G4_In
  specific = 4
FEATURE [App::DocumentObjectGroupPython] Sn_element001  label="Sn_element : 1"  # scripted group (container) (typed FeaturePython)
  n = 1
  ref = Sn_element
FEATURE [App::DocumentObjectGroupPython] G4_Sn  # scripted group (container) (typed FeaturePython)
  Dunit = g/cm3
  Dvalue = 7.31
  Group = -> [Sn_element001]
  conduct = 2
  density = 1
  expand = 3
  formula = Sn
  name = G4_Sn
  specific = 4
FEATURE [App::DocumentObjectGroupPython] Sb_element001  label="Sb_element : 1"  # scripted group (container) (typed FeaturePython)
  n = 1
  ref = Sb_element
FEATURE [App::DocumentObjectGroupPython] G4_Sb  # scripted group (container) (typed FeaturePython)
  Dunit = g/cm3
  Dvalue = 6.691
  Group = -> [Sb_element001]
  conduct = 2
  density = 1
  expand = 3
  formula = Sb
  name = G4_Sb
  specific = 4
FEATURE [App::DocumentObjectGroupPython] Te_element002  label="Te_element : 002"  # scripted group (container) (typed FeaturePython)
  n = 1
  ref = Te_element
FEATURE [App::DocumentObjectGroupPython] G4_Te  # scripted group (container) (typed FeaturePython)
  Dunit = g/cm3
  Dvalue = 6.24
  Group = -> [Te_element002]
  conduct = 2
  density = 1
  expand = 3
  formula = Te
  name = G4_Te
  specific = 4
FEATURE [App::DocumentObjectGroupPython] I_element010  label="I_element : 006"  # scripted group (container) (typed FeaturePython)
  n = 1
  ref = I_element
FEATURE [App::DocumentObjectGroupPython] G4_I  # scripted group (container) (typed FeaturePython)
  Dunit = g/cm3
  Dvalue = 4.93
  Group = -> [I_element010]
  conduct = 2
  density = 1
  expand = 3
  formula = I
  name = G4_I
  specific = 4
FEATURE [App::DocumentObjectGroupPython] Xe_element001  label="Xe_element : 1"  # scripted group (container) (typed FeaturePython)
  n = 1
  ref = Xe_element
FEATURE [App::DocumentObjectGroupPython] G4_Xe  # scripted group (container) (typed FeaturePython)
  Dunit = g/cm3
  Dvalue = 0.00548536
  Group = -> [Xe_element001]
  conduct = 2
  density = 1
  expand = 3
  formula = Xe
  name = G4_Xe
  specific = 4
FEATURE [App::DocumentObjectGroupPython] Cs_element003  label="Cs_element : 003"  # scripted group (container) (typed FeaturePython)
  n = 1
  ref = Cs_element
FEATURE [App::DocumentObjectGroupPython] G4_Cs  # scripted group (container) (typed FeaturePython)
  Dunit = g/cm3
  Dvalue = 1.873
  Group = -> [Cs_element003]
  conduct = 2
  density = 1
  expand = 3
  formula = Cs
  name = G4_Cs
  specific = 4
FEATURE [App::DocumentObjectGroupPython] Ba_element003  label="Ba_element : 003"  # scripted group (container) (typed FeaturePython)
  n = 1
  ref = Ba_element
FEATURE [App::DocumentObjectGroupPython] G4_Ba  # scripted group (container) (typed FeaturePython)
  Dunit = g/cm3
  Dvalue = 3.5
  Group = -> [Ba_element003]
  conduct = 2
  density = 1
  expand = 3
  formula = Ba
  name = G4_Ba
  specific = 4
FEATURE [App::DocumentObjectGroupPython] La_element003  label="La_element : 003"  # scripted group (container) (typed FeaturePython)
  n = 1
  ref = La_element
FEATURE [App::DocumentObjectGroupPython] G4_La  # scripted group (container) (typed FeaturePython)
  Dunit = g/cm3
  Dvalue = 6.154
  Group = -> [La_element003]
  conduct = 2
  density = 1
  expand = 3
  formula = La
  name = G4_La
  specific = 4
FEATURE [App::DocumentObjectGroupPython] Ce_element002  label="Ce_element : 1"  # scripted group (container) (typed FeaturePython)
  n = 1
  ref = Ce_element
FEATURE [App::DocumentObjectGroupPython] G4_Ce  # scripted group (container) (typed FeaturePython)
  Dunit = g/cm3
  Dvalue = 6.657
  Group = -> [Ce_element002]
  conduct = 2
  density = 1
  expand = 3
  formula = Ce
  name = G4_Ce
  specific = 4
FEATURE [App::DocumentObjectGroupPython] Pr_element001  label="Pr_element : 1"  # scripted group (container) (typed FeaturePython)
  n = 1
  ref = Pr_element
FEATURE [App::DocumentObjectGroupPython] G4_Pr  # scripted group (container) (typed FeaturePython)
  Dunit = g/cm3
  Dvalue = 6.71
  Group = -> [Pr_element001]
  conduct = 2
  density = 1
  expand = 3
  formula = Pr
  name = G4_Pr
  specific = 4
FEATURE [App::DocumentObjectGroupPython] Nd_element001  label="Nd_element : 1"  # scripted group (container) (typed FeaturePython)
  n = 1
  ref = Nd_element
FEATURE [App::DocumentObjectGroupPython] G4_Nd  # scripted group (container) (typed FeaturePython)
  Dunit = g/cm3
  Dvalue = 6.9
  Group = -> [Nd_element001]
  conduct = 2
  density = 1
  expand = 3
  formula = Nd
  name = G4_Nd
  specific = 4
FEATURE [App::DocumentObjectGroupPython] Pm_element001  label="Pm_element : 1"  # scripted group (container) (typed FeaturePython)
  n = 1
  ref = Pm_element
FEATURE [App::DocumentObjectGroupPython] G4_Pm  # scripted group (container) (typed FeaturePython)
  Dunit = g/cm3
  Dvalue = 7.22
  Group = -> [Pm_element001]
  conduct = 2
  density = 1
  expand = 3
  formula = Pm
  name = G4_Pm
  specific = 4
FEATURE [App::DocumentObjectGroupPython] Sm_element001  label="Sm_element : 1"  # scripted group (container) (typed FeaturePython)
  n = 1
  ref = Sm_element
FEATURE [App::DocumentObjectGroupPython] G4_Sm  # scripted group (container) (typed FeaturePython)
  Dunit = g/cm3
  Dvalue = 7.46
  Group = -> [Sm_element001]
  conduct = 2
  density = 1
  expand = 3
  formula = Sm
  name = G4_Sm
  specific = 4
FEATURE [App::DocumentObjectGroupPython] Eu_element001  label="Eu_element : 1"  # scripted group (container) (typed FeaturePython)
  n = 1
  ref = Eu_element
FEATURE [App::DocumentObjectGroupPython] G4_Eu  # scripted group (container) (typed FeaturePython)
  Dunit = g/cm3
  Dvalue = 5.243
  Group = -> [Eu_element001]
  conduct = 2
  density = 1
  expand = 3
  formula = Eu
  name = G4_Eu
  specific = 4
FEATURE [App::DocumentObjectGroupPython] Gd_element002  label="Gd_element : 1"  # scripted group (container) (typed FeaturePython)
  n = 1
  ref = Gd_element
FEATURE [App::DocumentObjectGroupPython] G4_Gd  # scripted group (container) (typed FeaturePython)
  Dunit = g/cm3
  Dvalue = 7.9004
  Group = -> [Gd_element002]
  conduct = 2
  density = 1
  expand = 3
  formula = Gd
  name = G4_Gd
  specific = 4
FEATURE [App::DocumentObjectGroupPython] Tb_element001  label="Tb_element : 1"  # scripted group (container) (typed FeaturePython)
  n = 1
  ref = Tb_element
FEATURE [App::DocumentObjectGroupPython] G4_Tb  # scripted group (container) (typed FeaturePython)
  Dunit = g/cm3
  Dvalue = 8.229
  Group = -> [Tb_element001]
  conduct = 2
  density = 1
  expand = 3
  formula = Tb
  name = G4_Tb
  specific = 4
FEATURE [App::DocumentObjectGroupPython] Dy_element001  label="Dy_element : 1"  # scripted group (container) (typed FeaturePython)
  n = 1
  ref = Dy_element
FEATURE [App::DocumentObjectGroupPython] G4_Dy  # scripted group (container) (typed FeaturePython)
  Dunit = g/cm3
  Dvalue = 8.55
  Group = -> [Dy_element001]
  conduct = 2
  density = 1
  expand = 3
  formula = Dy
  name = G4_Dy
  specific = 4
FEATURE [App::DocumentObjectGroupPython] Ho_element001  label="Ho_element : 1"  # scripted group (container) (typed FeaturePython)
  n = 1
  ref = Ho_element
FEATURE [App::DocumentObjectGroupPython] G4_Ho  # scripted group (container) (typed FeaturePython)
  Dunit = g/cm3
  Dvalue = 8.795
  Group = -> [Ho_element001]
  conduct = 2
  density = 1
  expand = 3
  formula = Ho
  name = G4_Ho
  specific = 4
FEATURE [App::DocumentObjectGroupPython] Er_element001  label="Er_element : 1"  # scripted group (container) (typed FeaturePython)
  n = 1
  ref = Er_element
FEATURE [App::DocumentObjectGroupPython] G4_Er  # scripted group (container) (typed FeaturePython)
  Dunit = g/cm3
  Dvalue = 9.066
  Group = -> [Er_element001]
  conduct = 2
  density = 1
  expand = 3
  formula = Er
  name = G4_Er
  specific = 4
FEATURE [App::DocumentObjectGroupPython] Tm_element001  label="Tm_element : 1"  # scripted group (container) (typed FeaturePython)
  n = 1
  ref = Tm_element
FEATURE [App::DocumentObjectGroupPython] G4_Tm  # scripted group (container) (typed FeaturePython)
  Dunit = g/cm3
  Dvalue = 9.321
  Group = -> [Tm_element001]
  conduct = 2
  density = 1
  expand = 3
  formula = Tm
  name = G4_Tm
  specific = 4
FEATURE [App::DocumentObjectGroupPython] Yb_element001  label="Yb_element : 1"  # scripted group (container) (typed FeaturePython)
  n = 1
  ref = Yb_element
FEATURE [App::DocumentObjectGroupPython] G4_Yb  # scripted group (container) (typed FeaturePython)
  Dunit = g/cm3
  Dvalue = 6.73
  Group = -> [Yb_element001]
  conduct = 2
  density = 1
  expand = 3
  formula = Yb
  name = G4_Yb
  specific = 4
FEATURE [App::DocumentObjectGroupPython] Lu_element001  label="Lu_element : 1"  # scripted group (container) (typed FeaturePython)
  n = 1
  ref = Lu_element
FEATURE [App::DocumentObjectGroupPython] G4_Lu  # scripted group (container) (typed FeaturePython)
  Dunit = g/cm3
  Dvalue = 9.84
  Group = -> [Lu_element001]
  conduct = 2
  density = 1
  expand = 3
  formula = Lu
  name = G4_Lu
  specific = 4
FEATURE [App::DocumentObjectGroupPython] Hf_element001  label="Hf_element : 1"  # scripted group (container) (typed FeaturePython)
  n = 1
  ref = Hf_element
FEATURE [App::DocumentObjectGroupPython] G4_Hf  # scripted group (container) (typed FeaturePython)
  Dunit = g/cm3
  Dvalue = 13.31
  Group = -> [Hf_element001]
  conduct = 2
  density = 1
  expand = 3
  formula = Hf
  name = G4_Hf
  specific = 4
FEATURE [App::DocumentObjectGroupPython] Ta_element001  label="Ta_element : 1"  # scripted group (container) (typed FeaturePython)
  n = 1
  ref = Ta_element
FEATURE [App::DocumentObjectGroupPython] G4_Ta  # scripted group (container) (typed FeaturePython)
  Dunit = g/cm3
  Dvalue = 16.654
  Group = -> [Ta_element001]
  conduct = 2
  density = 1
  expand = 3
  formula = Ta
  name = G4_Ta
  specific = 4
FEATURE [App::DocumentObjectGroupPython] W_element004  label="W_element : 004"  # scripted group (container) (typed FeaturePython)
  n = 1
  ref = W_element
FEATURE [App::DocumentObjectGroupPython] G4_W  # scripted group (container) (typed FeaturePython)
  Dunit = g/cm3
  Dvalue = 19.3
  Group = -> [W_element004]
  conduct = 2
  density = 1
  expand = 3
  formula = W
  name = G4_W
  specific = 4
FEATURE [App::DocumentObjectGroupPython] Re_element001  label="Re_element : 1"  # scripted group (container) (typed FeaturePython)
  n = 1
  ref = Re_element
FEATURE [App::DocumentObjectGroupPython] G4_Re  # scripted group (container) (typed FeaturePython)
  Dunit = g/cm3
  Dvalue = 21.02
  Group = -> [Re_element001]
  conduct = 2
  density = 1
  expand = 3
  formula = Re
  name = G4_Re
  specific = 4
FEATURE [App::DocumentObjectGroupPython] Os_element001  label="Os_element : 1"  # scripted group (container) (typed FeaturePython)
  n = 1
  ref = Os_element
FEATURE [App::DocumentObjectGroupPython] G4_Os  # scripted group (container) (typed FeaturePython)
  Dunit = g/cm3
  Dvalue = 22.57
  Group = -> [Os_element001]
  conduct = 2
  density = 1
  expand = 3
  formula = Os
  name = G4_Os
  specific = 4
FEATURE [App::DocumentObjectGroupPython] Ir_element001  label="Ir_element : 1"  # scripted group (container) (typed FeaturePython)
  n = 1
  ref = Ir_element
FEATURE [App::DocumentObjectGroupPython] G4_Ir  # scripted group (container) (typed FeaturePython)
  Dunit = g/cm3
  Dvalue = 22.42
  Group = -> [Ir_element001]
  conduct = 2
  density = 1
  expand = 3
  formula = Ir
  name = G4_Ir
  specific = 4
FEATURE [App::DocumentObjectGroupPython] Pt_element001  label="Pt_element : 1"  # scripted group (container) (typed FeaturePython)
  n = 1
  ref = Pt_element
FEATURE [App::DocumentObjectGroupPython] G4_Pt  # scripted group (container) (typed FeaturePython)
  Dunit = g/cm3
  Dvalue = 21.45
  Group = -> [Pt_element001]
  conduct = 2
  density = 1
  expand = 3
  formula = Pt
  name = G4_Pt
  specific = 4
FEATURE [App::DocumentObjectGroupPython] Au_element001  label="Au_element : 1"  # scripted group (container) (typed FeaturePython)
  n = 1
  ref = Au_element
FEATURE [App::DocumentObjectGroupPython] G4_Au  # scripted group (container) (typed FeaturePython)
  Dunit = g/cm3
  Dvalue = 19.32
  Group = -> [Au_element001]
  conduct = 2
  density = 1
  expand = 3
  formula = Au
  name = G4_Au
  specific = 4
FEATURE [App::DocumentObjectGroupPython] Hg_element002  label="Hg_element : 002"  # scripted group (container) (typed FeaturePython)
  n = 1
  ref = Hg_element
FEATURE [App::DocumentObjectGroupPython] G4_Hg  # scripted group (container) (typed FeaturePython)
  Dunit = g/cm3
  Dvalue = 13.546
  Group = -> [Hg_element002]
  conduct = 2
  density = 1
  expand = 3
  formula = Hg
  name = G4_Hg
  specific = 4
FEATURE [App::DocumentObjectGroupPython] Tl_element002  label="Tl_element : 002"  # scripted group (container) (typed FeaturePython)
  n = 1
  ref = Tl_element
FEATURE [App::DocumentObjectGroupPython] G4_Tl  # scripted group (container) (typed FeaturePython)
  Dunit = g/cm3
  Dvalue = 11.72
  Group = -> [Tl_element002]
  conduct = 2
  density = 1
  expand = 3
  formula = Tl
  name = G4_Tl
  specific = 4
FEATURE [App::DocumentObjectGroupPython] Pb_element003  label="Pb_element : 1"  # scripted group (container) (typed FeaturePython)
  n = 1
  ref = Pb_element
FEATURE [App::DocumentObjectGroupPython] G4_Pb  # scripted group (container) (typed FeaturePython)
  Dunit = g/cm3
  Dvalue = 11.35
  Group = -> [Pb_element003]
  conduct = 2
  density = 1
  expand = 3
  formula = Pb
  name = G4_Pb
  specific = 4
FEATURE [App::DocumentObjectGroupPython] Bi_element002  label="Bi_element : 1"  # scripted group (container) (typed FeaturePython)
  n = 1
  ref = Bi_element
FEATURE [App::DocumentObjectGroupPython] G4_Bi  # scripted group (container) (typed FeaturePython)
  Dunit = g/cm3
  Dvalue = 9.747
  Group = -> [Bi_element002]
  conduct = 2
  density = 1
  expand = 3
  formula = Bi
  name = G4_Bi
  specific = 4
FEATURE [App::DocumentObjectGroupPython] Po_element001  label="Po_element : 1"  # scripted group (container) (typed FeaturePython)
  n = 1
  ref = Po_element
FEATURE [App::DocumentObjectGroupPython] G4_Po  # scripted group (container) (typed FeaturePython)
  Dunit = g/cm3
  Dvalue = 9.32
  Group = -> [Po_element001]
  conduct = 2
  density = 1
  expand = 3
  formula = Po
  name = G4_Po
  specific = 4
FEATURE [App::DocumentObjectGroupPython] At_element001  label="At_element : 1"  # scripted group (container) (typed FeaturePython)
  n = 1
  ref = At_element
FEATURE [App::DocumentObjectGroupPython] G4_At  # scripted group (container) (typed FeaturePython)
  Dunit = g/cm3
  Dvalue = 9.32
  Group = -> [At_element001]
  conduct = 2
  density = 1
  expand = 3
  formula = At
  name = G4_At
  specific = 4
FEATURE [App::DocumentObjectGroupPython] Rn_element001  label="Rn_element : 1"  # scripted group (container) (typed FeaturePython)
  n = 1
  ref = Rn_element
FEATURE [App::DocumentObjectGroupPython] G4_Rn  # scripted group (container) (typed FeaturePython)
  Dunit = g/cm3
  Dvalue = 0.00900662
  Group = -> [Rn_element001]
  conduct = 2
  density = 1
  expand = 3
  formula = Rn
  name = G4_Rn
  specific = 4
FEATURE [App::DocumentObjectGroupPython] Fr_element001  label="Fr_element : 1"  # scripted group (container) (typed FeaturePython)
  n = 1
  ref = Fr_element
FEATURE [App::DocumentObjectGroupPython] G4_Fr  # scripted group (container) (typed FeaturePython)
  Dunit = g/cm3
  Dvalue = 1
  Group = -> [Fr_element001]
  conduct = 2
  density = 1
  expand = 3
  formula = Fr
  name = G4_Fr
  specific = 4
FEATURE [App::DocumentObjectGroupPython] Ra_element001  label="Ra_element : 1"  # scripted group (container) (typed FeaturePython)
  n = 1
  ref = Ra_element
FEATURE [App::DocumentObjectGroupPython] G4_Ra  # scripted group (container) (typed FeaturePython)
  Dunit = g/cm3
  Dvalue = 5
  Group = -> [Ra_element001]
  conduct = 2
  density = 1
  expand = 3
  formula = Ra
  name = G4_Ra
  specific = 4
FEATURE [App::DocumentObjectGroupPython] Ac_element001  label="Ac_element : 1"  # scripted group (container) (typed FeaturePython)
  n = 1
  ref = Ac_element
FEATURE [App::DocumentObjectGroupPython] G4_Ac  # scripted group (container) (typed FeaturePython)
  Dunit = g/cm3
  Dvalue = 10.07
  Group = -> [Ac_element001]
  conduct = 2
  density = 1
  expand = 3
  formula = Ac
  name = G4_Ac
  specific = 4
FEATURE [App::DocumentObjectGroupPython] Th_element001  label="Th_element : 1"  # scripted group (container) (typed FeaturePython)
  n = 1
  ref = Th_element
FEATURE [App::DocumentObjectGroupPython] G4_Th  # scripted group (container) (typed FeaturePython)
  Dunit = g/cm3
  Dvalue = 11.72
  Group = -> [Th_element001]
  conduct = 2
  density = 1
  expand = 3
  formula = Th
  name = G4_Th
  specific = 4
FEATURE [App::DocumentObjectGroupPython] Pa_element001  label="Pa_element : 1"  # scripted group (container) (typed FeaturePython)
  n = 1
  ref = Pa_element
FEATURE [App::DocumentObjectGroupPython] G4_Pa  # scripted group (container) (typed FeaturePython)
  Dunit = g/cm3
  Dvalue = 15.37
  Group = -> [Pa_element001]
  conduct = 2
  density = 1
  expand = 3
  formula = Pa
  name = G4_Pa
  specific = 4
FEATURE [App::DocumentObjectGroupPython] U_element004  label="U_element : 004"  # scripted group (container) (typed FeaturePython)
  n = 1
  ref = U_element
FEATURE [App::DocumentObjectGroupPython] G4_U  # scripted group (container) (typed FeaturePython)
  Dunit = g/cm3
  Dvalue = 18.95
  Group = -> [U_element004]
  conduct = 2
  density = 1
  expand = 3
  formula = U
  name = G4_U
  specific = 4
FEATURE [App::DocumentObjectGroupPython] Np_element001  label="Np_element : 1"  # scripted group (container) (typed FeaturePython)
  n = 1
  ref = Np_element
FEATURE [App::DocumentObjectGroupPython] G4_Np  # scripted group (container) (typed FeaturePython)
  Dunit = g/cm3
  Dvalue = 20.25
  Group = -> [Np_element001]
  conduct = 2
  density = 1
  expand = 3
  formula = Np
  name = G4_Np
  specific = 4
FEATURE [App::DocumentObjectGroupPython] Pu_element002  label="Pu_element : 002"  # scripted group (container) (typed FeaturePython)
  n = 1
  ref = Pu_element
FEATURE [App::DocumentObjectGroupPython] G4_Pu  # scripted group (container) (typed FeaturePython)
  Dunit = g/cm3
  Dvalue = 19.84
  Group = -> [Pu_element002]
  conduct = 2
  density = 1
  expand = 3
  formula = Pu
  name = G4_Pu
  specific = 4
FEATURE [App::DocumentObjectGroupPython] Am_element001  label="Am_element : 1"  # scripted group (container) (typed FeaturePython)
  n = 1
  ref = Am_element
FEATURE [App::DocumentObjectGroupPython] G4_Am  # scripted group (container) (typed FeaturePython)
  Dunit = g/cm3
  Dvalue = 13.67
  Group = -> [Am_element001]
  conduct = 2
  density = 1
  expand = 3
  formula = Am
  name = G4_Am
  specific = 4
FEATURE [App::DocumentObjectGroupPython] Cm_element001  label="Cm_element : 1"  # scripted group (container) (typed FeaturePython)
  n = 1
  ref = Cm_element
FEATURE [App::DocumentObjectGroupPython] G4_Cm  # scripted group (container) (typed FeaturePython)
  Dunit = g/cm3
  Dvalue = 13.51
  Group = -> [Cm_element001]
  conduct = 2
  density = 1
  expand = 3
  formula = Cm
  name = G4_Cm
  specific = 4
FEATURE [App::DocumentObjectGroupPython] Bk_element001  label="Bk_element : 1"  # scripted group (container) (typed FeaturePython)
  n = 1
  ref = Bk_element
FEATURE [App::DocumentObjectGroupPython] G4_Bk  # scripted group (container) (typed FeaturePython)
  Dunit = g/cm3
  Dvalue = 14
  Group = -> [Bk_element001]
  conduct = 2
  density = 1
  expand = 3
  formula = Bk
  name = G4_Bk
  specific = 4
FEATURE [App::DocumentObjectGroupPython] Cf_element001  label="Cf_element : 1"  # scripted group (container) (typed FeaturePython)
  n = 1
  ref = Cf_element
FEATURE [App::DocumentObjectGroupPython] G4_Cf  # scripted group (container) (typed FeaturePython)
  Dunit = g/cm3
  Dvalue = 10
  Group = -> [Cf_element001]
  conduct = 2
  density = 1
  expand = 3
  formula = Cf
  name = G4_Cf
  specific = 4
FEATURE [App::DocumentObjectGroupPython] Element  # scripted group (container) (typed FeaturePython)
  Group = -> [G4_H,G4_He,G4_Li,G4_Be,G4_B,G4_C,G4_N,G4_O,G4_F,G4_Ne,G4_Na,G4_Mg,G4_Al,G4_Si,G4_P,G4_S,G4_Cl,G4_Ar,G4_K,G4_Ca,G4_Sc,G4_Ti,G4_V,G4_Cr,G4_Mn,G4_Fe,G4_Co,G4_Ni,G4_Cu,G4_Zn,G4_Ga,G4_Ge,G4_As,G4_Se,G4_Br,G4_Kr,G4_Rb,G4_Sr,G4_Y,G4_Zr,G4_Nb,G4_Mo,G4_Tc,G4_Ru,G4_Rh,G4_Pd,G4_Ag,G4_Cd,G4_In,G4_Sn,G4_Sb,G4_Te,G4_I,G4_Xe,G4_Cs,G4_Ba,G4_La,G4_Ce,G4_Pr,G4_Nd,G4_Pm,G4_Sm,G4_Eu,G4_Gd,G4_Tb,G4_Dy,G4_Ho,G4_Er,+30 more]
FEATURE [App::DocumentObjectGroupPython] H_element114  label="H_element : 063"  # scripted group (container) (typed FeaturePython)
  n = 2
  ref = H_element
FEATURE [App::DocumentObjectGroupPython] G4_lH2  # scripted group (container) (typed FeaturePython)
  Dunit = g/cm3
  Dvalue = 0.0708
  Group = -> [H_element114]
  conduct = 2
  density = 1
  expand = 3
  formula = G4_lH2
  name = G4_lH2
  specific = 4
FEATURE [App::DocumentObjectGroupPython] N_element049  label="N_element : 022"  # scripted group (container) (typed FeaturePython)
  n = 2
  ref = N_element
FEATURE [App::DocumentObjectGroupPython] G4_lN2  # scripted group (container) (typed FeaturePython)
  Dunit = g/cm3
  Dvalue = 0.807
  Group = -> [N_element049]
  conduct = 2
  density = 1
  expand = 3
  formula = G4_lN2
  name = G4_lN2
  specific = 4
FEATURE [App::DocumentObjectGroupPython] O_element106  label="O_element : 060"  # scripted group (container) (typed FeaturePython)
  n = 2
  ref = O_element
FEATURE [App::DocumentObjectGroupPython] G4_lO2  # scripted group (container) (typed FeaturePython)
  Dunit = g/cm3
  Dvalue = 1.141
  Group = -> [O_element106]
  conduct = 2
  density = 1
  expand = 3
  formula = G4_lO2
  name = G4_lO2
  specific = 4
FEATURE [App::DocumentObjectGroupPython] Ar  label="Ar : 1"  # scripted group (container) (typed FeaturePython)
  n = 1
  ref = Ar
FEATURE [App::DocumentObjectGroupPython] G4_lAr  # scripted group (container) (typed FeaturePython)
  Dunit = g/cm3
  Dvalue = 1.396
  Group = -> [Ar]
  conduct = 2
  density = 1
  expand = 3
  formula = G4_lAr
  name = G4_lAr
  specific = 4
FEATURE [App::DocumentObjectGroupPython] Br  label="Br : 1"  # scripted group (container) (typed FeaturePython)
  n = 1
  ref = Br
FEATURE [App::DocumentObjectGroupPython] G4_lBr  # scripted group (container) (typed FeaturePython)
  Dunit = g/cm3
  Dvalue = 3.1028
  Group = -> [Br]
  conduct = 2
  density = 1
  expand = 3
  formula = G4_lBr
  name = G4_lBr
  specific = 4
FEATURE [App::DocumentObjectGroupPython] Kr  label="Kr : 1"  # scripted group (container) (typed FeaturePython)
  n = 1
  ref = Kr
FEATURE [App::DocumentObjectGroupPython] G4_lKr  # scripted group (container) (typed FeaturePython)
  Dunit = g/cm3
  Dvalue = 2.418
  Group = -> [Kr]
  conduct = 2
  density = 1
  expand = 3
  formula = G4_lKr
  name = G4_lKr
  specific = 4
FEATURE [App::DocumentObjectGroupPython] Xe  label="Xe : 1"  # scripted group (container) (typed FeaturePython)
  n = 1
  ref = Xe
FEATURE [App::DocumentObjectGroupPython] G4_lXe  # scripted group (container) (typed FeaturePython)
  Dunit = g/cm3
  Dvalue = 2.953
  Group = -> [Xe]
  conduct = 2
  density = 1
  expand = 3
  formula = G4_lXe
  name = G4_lXe
  specific = 4
FEATURE [App::DocumentObjectGroupPython] O_element107  label="O_element : 061"  # scripted group (container) (typed FeaturePython)
  n = 4
  ref = O_element
FEATURE [App::DocumentObjectGroupPython] Pb_element004  label="Pb_element : 002"  # scripted group (container) (typed FeaturePython)
  n = 1
  ref = Pb_element
FEATURE [App::DocumentObjectGroupPython] W_element005  label="W_element : 005"  # scripted group (container) (typed FeaturePython)
  n = 1
  ref = W_element
FEATURE [App::DocumentObjectGroupPython] G4_PbWO4  # scripted group (container) (typed FeaturePython)
  Dunit = g/cm3
  Dvalue = 8.28
  Group = -> [O_element107,Pb_element004,W_element005]
  conduct = 2
  density = 1
  expand = 3
  formula = G4_PbWO4
  name = G4_PbWO4
  specific = 4
FEATURE [App::DocumentObjectGroupPython] alactic  label="alactic : 1"  # scripted group (container) (typed FeaturePython)
  n = 1
  ref = alactic
FEATURE [App::DocumentObjectGroupPython] G4_Galactic  # scripted group (container) (typed FeaturePython)
  Dunit = g/cm3
  Dvalue = 0
  Group = -> [alactic]
  conduct = 2
  density = 1
  expand = 3
  formula = G4_Galactic
  name = G4_Galactic
  specific = 4
FEATURE [App::DocumentObjectGroupPython] RAPHITE_POROUS  label="RAPHITE_POROUS : 1"  # scripted group (container) (typed FeaturePython)
  n = 1
  ref = RAPHITE_POROUS
FEATURE [App::DocumentObjectGroupPython] G4_GRAPHITE_POROUS  # scripted group (container) (typed FeaturePython)
  Dunit = g/cm3
  Dvalue = 1.7
  Group = -> [RAPHITE_POROUS]
  conduct = 2
  density = 1
  expand = 3
  formula = G4_GRAPHITE_POROUS
  name = G4_GRAPHITE_POROUS
  specific = 4
FEATURE [App::DocumentObjectGroupPython] H_element115  label="H_element : 0.150"  # scripted group (container) (typed FeaturePython)
  n = 0.080538
FEATURE [App::DocumentObjectGroupPython] C_element125  label="C_element : 0.600"  # scripted group (container) (typed FeaturePython)
  n = 0.599848
FEATURE [App::DocumentObjectGroupPython] O_element108  label="O_element : 0.320"  # scripted group (container) (typed FeaturePython)
  n = 0.319614
FEATURE [App::DocumentObjectGroupPython] G4_LUCITE  # scripted group (container) (typed FeaturePython)
  Dunit = g/cm3
  Dvalue = 1.19
  Group = -> [H_element115,C_element125,O_element108]
  conduct = 2
  density = 1
  expand = 3
  formula = G4_LUCITE
  name = G4_LUCITE
  specific = 4
FEATURE [App::DocumentObjectGroupPython] Cu_element002  label="Cu_element : 62"  # scripted group (container) (typed FeaturePython)
  n = 62
  ref = Cu_element
FEATURE [App::DocumentObjectGroupPython] Zn_element002  label="Zn_element : 35"  # scripted group (container) (typed FeaturePython)
  n = 35
  ref = Zn_element
FEATURE [App::DocumentObjectGroupPython] Pb_element005  label="Pb_element : 3"  # scripted group (container) (typed FeaturePython)
  n = 3
  ref = Pb_element
FEATURE [App::DocumentObjectGroupPython] G4_BRASS  # scripted group (container) (typed FeaturePython)
  Dunit = g/cm3
  Dvalue = 8.52
  Group = -> [Cu_element002,Zn_element002,Pb_element005]
  conduct = 2
  density = 1
  expand = 3
  formula = G4_BRASS
  name = G4_BRASS
  specific = 4
FEATURE [App::DocumentObjectGroupPython] Cu_element003  label="Cu_element : 89"  # scripted group (container) (typed FeaturePython)
  n = 89
  ref = Cu_element
FEATURE [App::DocumentObjectGroupPython] Zn_element003  label="Zn_element : 9"  # scripted group (container) (typed FeaturePython)
  n = 9
  ref = Zn_element
FEATURE [App::DocumentObjectGroupPython] Pb_element006  label="Pb_element : 2"  # scripted group (container) (typed FeaturePython)
  n = 2
  ref = Pb_element
FEATURE [App::DocumentObjectGroupPython] G4_BRONZE  # scripted group (container) (typed FeaturePython)
  Dunit = g/cm3
  Dvalue = 8.82
  Group = -> [Cu_element003,Zn_element003,Pb_element006]
  conduct = 2
  density = 1
  expand = 3
  formula = G4_BRONZE
  name = G4_BRONZE
  specific = 4
FEATURE [App::DocumentObjectGroupPython] Fe_element008  label="Fe_element : 74"  # scripted group (container) (typed FeaturePython)
  n = 74
  ref = Fe_element
FEATURE [App::DocumentObjectGroupPython] Cr_element002  label="Cr_element : 18"  # scripted group (container) (typed FeaturePython)
  n = 18
  ref = Cr_element
FEATURE [App::DocumentObjectGroupPython] Ni_element002  label="Ni_element : 8"  # scripted group (container) (typed FeaturePython)
  n = 8
  ref = Ni_element
FEATURE [App::DocumentObjectGroupPython] G4_STAINLESS_STEEL  label="G4_STAINLESS-STEEL"  # scripted group (container) (typed FeaturePython)
  Dunit = g/cm3
  Dvalue = 8
  Group = -> [Fe_element008,Cr_element002,Ni_element002]
  conduct = 2
  density = 1
  expand = 3
  formula = G4_STAINLESS-STEEL
  name = G4_STAINLESS-STEEL
  specific = 4
FEATURE [App::DocumentObjectGroupPython] H_element116  label="H_element : 064"  # scripted group (container) (typed FeaturePython)
  n = 18
  ref = H_element
FEATURE [App::DocumentObjectGroupPython] C_element126  label="C_element : 071"  # scripted group (container) (typed FeaturePython)
  n = 12
  ref = C_element
FEATURE [App::DocumentObjectGroupPython] O_element109  label="O_element : 062"  # scripted group (container) (typed FeaturePython)
  n = 7
  ref = O_element
FEATURE [App::DocumentObjectGroupPython] G4_CR39  # scripted group (container) (typed FeaturePython)
  Dunit = g/cm3
  Dvalue = 1.32
  Group = -> [H_element116,C_element126,O_element109]
  conduct = 2
  density = 1
  expand = 3
  formula = G4_CR39
  name = G4_CR39
  specific = 4
FEATURE [App::DocumentObjectGroupPython] H_element117  label="H_element : 38"  # scripted group (container) (typed FeaturePython)
  n = 38
  ref = H_element
FEATURE [App::DocumentObjectGroupPython] C_element127  label="C_element : 072"  # scripted group (container) (typed FeaturePython)
  n = 18
  ref = C_element
FEATURE [App::DocumentObjectGroupPython] O_element110  label="O_element : 063"  # scripted group (container) (typed FeaturePython)
  n = 1
  ref = O_element
FEATURE [App::DocumentObjectGroupPython] G4_OCTADECANOL  # scripted group (container) (typed FeaturePython)
  Dunit = g/cm3
  Dvalue = 0.812
  Group = -> [H_element117,C_element127,O_element110]
  conduct = 2
  density = 1
  expand = 3
  formula = G4_OCTADECANOL
  name = G4_OCTADECANOL
  specific = 4
FEATURE [App::DocumentObjectGroupPython] HEP  # scripted group (container) (typed FeaturePython)
  Group = -> [G4_lH2,G4_lN2,G4_lO2,G4_lAr,G4_lBr,G4_lKr,G4_lXe,G4_PbWO4,G4_Galactic,G4_GRAPHITE_POROUS,G4_LUCITE,G4_BRASS,G4_BRONZE,G4_STAINLESS_STEEL,G4_CR39,G4_OCTADECANOL]
FEATURE [App::DocumentObjectGroupPython] C_element128  label="C_element : 073"  # scripted group (container) (typed FeaturePython)
  n = 14
  ref = C_element
FEATURE [App::DocumentObjectGroupPython] H_element118  label="H_element : 065"  # scripted group (container) (typed FeaturePython)
  n = 10
  ref = H_element
FEATURE [App::DocumentObjectGroupPython] O_element111  label="O_element : 064"  # scripted group (container) (typed FeaturePython)
  n = 2
  ref = O_element
FEATURE [App::DocumentObjectGroupPython] N_element050  label="N_element : 023"  # scripted group (container) (typed FeaturePython)
  n = 2
  ref = N_element
FEATURE [App::DocumentObjectGroupPython] G4_KEVLAR  # scripted group (container) (typed FeaturePython)
  Dunit = g/cm3
  Dvalue = 1.44
  Group = -> [C_element128,H_element118,O_element111,N_element050]
  conduct = 2
  density = 1
  expand = 3
  formula = G4_KEVLAR
  name = G4_KEVLAR
  specific = 4
FEATURE [App::DocumentObjectGroupPython] C_element129  label="C_element : 074"  # scripted group (container) (typed FeaturePython)
  n = 10
  ref = C_element
FEATURE [App::DocumentObjectGroupPython] H_element119  label="H_element : 066"  # scripted group (container) (typed FeaturePython)
  n = 8
  ref = H_element
FEATURE [App::DocumentObjectGroupPython] O_element112  label="O_element : 065"  # scripted group (container) (typed FeaturePython)
  n = 4
  ref = O_element
FEATURE [App::DocumentObjectGroupPython] G4_DACRON  # scripted group (container) (typed FeaturePython)
  Dunit = g/cm3
  Dvalue = 1.4
  Group = -> [C_element129,H_element119,O_element112]
  conduct = 2
  density = 1
  expand = 3
  formula = G4_DACRON
  name = G4_DACRON
  specific = 4
FEATURE [App::DocumentObjectGroupPython] C_element130  label="C_element : 075"  # scripted group (container) (typed FeaturePython)
  n = 4
  ref = C_element
FEATURE [App::DocumentObjectGroupPython] H_element120  label="H_element : 067"  # scripted group (container) (typed FeaturePython)
  n = 5
  ref = H_element
FEATURE [App::DocumentObjectGroupPython] Cl_element030  label="Cl_element : 016"  # scripted group (container) (typed FeaturePython)
  n = 1
  ref = Cl_element
FEATURE [App::DocumentObjectGroupPython] G4_NEOPRENE  # scripted group (container) (typed FeaturePython)
  Dunit = g/cm3
  Dvalue = 1.23
  Group = -> [C_element130,H_element120,Cl_element030]
  conduct = 2
  density = 1
  expand = 3
  formula = G4_NEOPRENE
  name = G4_NEOPRENE
  specific = 4
FEATURE [App::DocumentObjectGroupPython] Space  # scripted group (container) (typed FeaturePython)
  Group = -> [G4_KEVLAR,G4_DACRON,G4_NEOPRENE]
FEATURE [App::DocumentObjectGroupPython] H_element121  label="H_element : 068"  # scripted group (container) (typed FeaturePython)
  n = 5
  ref = H_element
FEATURE [App::DocumentObjectGroupPython] C_element131  label="C_element : 076"  # scripted group (container) (typed FeaturePython)
  n = 4
  ref = C_element
FEATURE [App::DocumentObjectGroupPython] N_element051  label="N_element : 3"  # scripted group (container) (typed FeaturePython)
  n = 3
  ref = N_element
FEATURE [App::DocumentObjectGroupPython] O_element113  label="O_element : 066"  # scripted group (container) (typed FeaturePython)
  n = 1
  ref = O_element
FEATURE [App::DocumentObjectGroupPython] G4_CYTOSINE  # scripted group (container) (typed FeaturePython)
  Dunit = g/cm3
  Dvalue = 1.55
  Group = -> [H_element121,C_element131,N_element051,O_element113]
  conduct = 2
  density = 1
  expand = 3
  formula = G4_CYTOSINE
  name = G4_CYTOSINE
  specific = 4
FEATURE [App::DocumentObjectGroupPython] H_element122  label="H_element : 069"  # scripted group (container) (typed FeaturePython)
  n = 6
  ref = H_element
FEATURE [App::DocumentObjectGroupPython] C_element132  label="C_element : 077"  # scripted group (container) (typed FeaturePython)
  n = 5
  ref = C_element
FEATURE [App::DocumentObjectGroupPython] N_element052  label="N_element : 024"  # scripted group (container) (typed FeaturePython)
  n = 2
  ref = N_element
FEATURE [App::DocumentObjectGroupPython] O_element114  label="O_element : 067"  # scripted group (container) (typed FeaturePython)
  n = 2
  ref = O_element
FEATURE [App::DocumentObjectGroupPython] G4_THYMINE  # scripted group (container) (typed FeaturePython)
  Dunit = g/cm3
  Dvalue = 1.23
  Group = -> [H_element122,C_element132,N_element052,O_element114]
  conduct = 2
  density = 1
  expand = 3
  formula = G4_THYMINE
  name = G4_THYMINE
  specific = 4
FEATURE [App::DocumentObjectGroupPython] H_element123  label="H_element : 070"  # scripted group (container) (typed FeaturePython)
  n = 4
  ref = H_element
FEATURE [App::DocumentObjectGroupPython] C_element133  label="C_element : 078"  # scripted group (container) (typed FeaturePython)
  n = 4
  ref = C_element
FEATURE [App::DocumentObjectGroupPython] N_element053  label="N_element : 025"  # scripted group (container) (typed FeaturePython)
  n = 2
  ref = N_element
FEATURE [App::DocumentObjectGroupPython] O_element115  label="O_element : 068"  # scripted group (container) (typed FeaturePython)
  n = 2
  ref = O_element
FEATURE [App::DocumentObjectGroupPython] G4_URACIL  # scripted group (container) (typed FeaturePython)
  Dunit = g/cm3
  Dvalue = 1.32
  Group = -> [H_element123,C_element133,N_element053,O_element115]
  conduct = 2
  density = 1
  expand = 3
  formula = G4_URACIL
  name = G4_URACIL
  specific = 4
FEATURE [App::DocumentObjectGroupPython] H_element124  label="H_element : 071"  # scripted group (container) (typed FeaturePython)
  n = 4
  ref = H_element
FEATURE [App::DocumentObjectGroupPython] C_element134  label="C_element : 079"  # scripted group (container) (typed FeaturePython)
  n = 5
  ref = C_element
FEATURE [App::DocumentObjectGroupPython] N_element054  label="N_element : 026"  # scripted group (container) (typed FeaturePython)
  n = 5
  ref = N_element
FEATURE [App::DocumentObjectGroupPython] G4_DNA_ADENINE  # scripted group (container) (typed FeaturePython)
  Dunit = g/cm3
  Dvalue = 1
  Group = -> [H_element124,C_element134,N_element054]
  conduct = 2
  density = 1
  expand = 3
  formula = G4_DNA_ADENINE
  name = G4_DNA_ADENINE
  specific = 4
FEATURE [App::DocumentObjectGroupPython] H_element125  label="H_element : 072"  # scripted group (container) (typed FeaturePython)
  n = 4
  ref = H_element
FEATURE [App::DocumentObjectGroupPython] C_element135  label="C_element : 080"  # scripted group (container) (typed FeaturePython)
  n = 5
  ref = C_element
FEATURE [App::DocumentObjectGroupPython] N_element055  label="N_element : 027"  # scripted group (container) (typed FeaturePython)
  n = 5
  ref = N_element
FEATURE [App::DocumentObjectGroupPython] O_element116  label="O_element : 069"  # scripted group (container) (typed FeaturePython)
  n = 1
  ref = O_element
FEATURE [App::DocumentObjectGroupPython] G4_DNA_GUANINE  # scripted group (container) (typed FeaturePython)
  Dunit = g/cm3
  Dvalue = 1
  Group = -> [H_element125,C_element135,N_element055,O_element116]
  conduct = 2
  density = 1
  expand = 3
  formula = G4_DNA_GUANINE
  name = G4_DNA_GUANINE
  specific = 4
FEATURE [App::DocumentObjectGroupPython] H_element126  label="H_element : 073"  # scripted group (container) (typed FeaturePython)
  n = 4
  ref = H_element
FEATURE [App::DocumentObjectGroupPython] C_element136  label="C_element : 081"  # scripted group (container) (typed FeaturePython)
  n = 4
  ref = C_element
FEATURE [App::DocumentObjectGroupPython] N_element056  label="N_element : 028"  # scripted group (container) (typed FeaturePython)
  n = 3
  ref = N_element
FEATURE [App::DocumentObjectGroupPython] O_element117  label="O_element : 070"  # scripted group (container) (typed FeaturePython)
  n = 1
  ref = O_element
FEATURE [App::DocumentObjectGroupPython] G4_DNA_CYTOSINE  # scripted group (container) (typed FeaturePython)
  Dunit = g/cm3
  Dvalue = 1
  Group = -> [H_element126,C_element136,N_element056,O_element117]
  conduct = 2
  density = 1
  expand = 3
  formula = G4_DNA_CYTOSINE
  name = G4_DNA_CYTOSINE
  specific = 4
FEATURE [App::DocumentObjectGroupPython] H_element127  label="H_element : 074"  # scripted group (container) (typed FeaturePython)
  n = 5
  ref = H_element
FEATURE [App::DocumentObjectGroupPython] C_element137  label="C_element : 082"  # scripted group (container) (typed FeaturePython)
  n = 5
  ref = C_element
FEATURE [App::DocumentObjectGroupPython] N_element057  label="N_element : 029"  # scripted group (container) (typed FeaturePython)
  n = 2
  ref = N_element
FEATURE [App::DocumentObjectGroupPython] O_element118  label="O_element : 071"  # scripted group (container) (typed FeaturePython)
  n = 2
  ref = O_element
FEATURE [App::DocumentObjectGroupPython] G4_DNA_THYMINE  # scripted group (container) (typed FeaturePython)
  Dunit = g/cm3
  Dvalue = 1
  Group = -> [H_element127,C_element137,N_element057,O_element118]
  conduct = 2
  density = 1
  expand = 3
  formula = G4_DNA_THYMINE
  name = G4_DNA_THYMINE
  specific = 4
FEATURE [App::DocumentObjectGroupPython] H_element128  label="H_element : 075"  # scripted group (container) (typed FeaturePython)
  n = 3
  ref = H_element
FEATURE [App::DocumentObjectGroupPython] C_element138  label="C_element : 083"  # scripted group (container) (typed FeaturePython)
  n = 4
  ref = C_element
FEATURE [App::DocumentObjectGroupPython] N_element058  label="N_element : 030"  # scripted group (container) (typed FeaturePython)
  n = 2
  ref = N_element
FEATURE [App::DocumentObjectGroupPython] O_element119  label="O_element : 072"  # scripted group (container) (typed FeaturePython)
  n = 2
  ref = O_element
FEATURE [App::DocumentObjectGroupPython] G4_DNA_URACIL  # scripted group (container) (typed FeaturePython)
  Dunit = g/cm3
  Dvalue = 1
  Group = -> [H_element128,C_element138,N_element058,O_element119]
  conduct = 2
  density = 1
  expand = 3
  formula = G4_DNA_URACIL
  name = G4_DNA_URACIL
  specific = 4
FEATURE [App::DocumentObjectGroupPython] H_element129  label="H_element : 076"  # scripted group (container) (typed FeaturePython)
  n = 10
  ref = H_element
FEATURE [App::DocumentObjectGroupPython] C_element139  label="C_element : 084"  # scripted group (container) (typed FeaturePython)
  n = 10
  ref = C_element
FEATURE [App::DocumentObjectGroupPython] N_element059  label="N_element : 031"  # scripted group (container) (typed FeaturePython)
  n = 5
  ref = N_element
FEATURE [App::DocumentObjectGroupPython] O_element120  label="O_element : 073"  # scripted group (container) (typed FeaturePython)
  n = 4
  ref = O_element
FEATURE [App::DocumentObjectGroupPython] G4_DNA_ADENOSINE  # scripted group (container) (typed FeaturePython)
  Dunit = g/cm3
  Dvalue = 1
  Group = -> [H_element129,C_element139,N_element059,O_element120]
  conduct = 2
  density = 1
  expand = 3
  formula = G4_DNA_ADENOSINE
  name = G4_DNA_ADENOSINE
  specific = 4
FEATURE [App::DocumentObjectGroupPython] H_element130  label="H_element : 077"  # scripted group (container) (typed FeaturePython)
  n = 10
  ref = H_element
FEATURE [App::DocumentObjectGroupPython] C_element140  label="C_element : 085"  # scripted group (container) (typed FeaturePython)
  n = 10
  ref = C_element
FEATURE [App::DocumentObjectGroupPython] N_element060  label="N_element : 032"  # scripted group (container) (typed FeaturePython)
  n = 5
  ref = N_element
FEATURE [App::DocumentObjectGroupPython] O_element121  label="O_element : 074"  # scripted group (container) (typed FeaturePython)
  n = 5
  ref = O_element
FEATURE [App::DocumentObjectGroupPython] G4_DNA_GUANOSINE  # scripted group (container) (typed FeaturePython)
  Dunit = g/cm3
  Dvalue = 1
  Group = -> [H_element130,C_element140,N_element060,O_element121]
  conduct = 2
  density = 1
  expand = 3
  formula = G4_DNA_GUANOSINE
  name = G4_DNA_GUANOSINE
  specific = 4
FEATURE [App::DocumentObjectGroupPython] H_element131  label="H_element : 078"  # scripted group (container) (typed FeaturePython)
  n = 10
  ref = H_element
FEATURE [App::DocumentObjectGroupPython] C_element141  label="C_element : 086"  # scripted group (container) (typed FeaturePython)
  n = 9
  ref = C_element
FEATURE [App::DocumentObjectGroupPython] N_element061  label="N_element : 033"  # scripted group (container) (typed FeaturePython)
  n = 3
  ref = N_element
FEATURE [App::DocumentObjectGroupPython] O_element122  label="O_element : 075"  # scripted group (container) (typed FeaturePython)
  n = 5
  ref = O_element
FEATURE [App::DocumentObjectGroupPython] G4_DNA_CYTIDINE  # scripted group (container) (typed FeaturePython)
  Dunit = g/cm3
  Dvalue = 1
  Group = -> [H_element131,C_element141,N_element061,O_element122]
  conduct = 2
  density = 1
  expand = 3
  formula = G4_DNA_CYTIDINE
  name = G4_DNA_CYTIDINE
  specific = 4
FEATURE [App::DocumentObjectGroupPython] H_element132  label="H_element : 079"  # scripted group (container) (typed FeaturePython)
  n = 9
  ref = H_element
FEATURE [App::DocumentObjectGroupPython] C_element142  label="C_element : 087"  # scripted group (container) (typed FeaturePython)
  n = 9
  ref = C_element
FEATURE [App::DocumentObjectGroupPython] N_element062  label="N_element : 034"  # scripted group (container) (typed FeaturePython)
  n = 2
  ref = N_element
FEATURE [App::DocumentObjectGroupPython] O_element123  label="O_element : 076"  # scripted group (container) (typed FeaturePython)
  n = 6
  ref = O_element
FEATURE [App::DocumentObjectGroupPython] G4_DNA_URIDINE  # scripted group (container) (typed FeaturePython)
  Dunit = g/cm3
  Dvalue = 1
  Group = -> [H_element132,C_element142,N_element062,O_element123]
  conduct = 2
  density = 1
  expand = 3
  formula = G4_DNA_URIDINE
  name = G4_DNA_URIDINE
  specific = 4
FEATURE [App::DocumentObjectGroupPython] H_element133  label="H_element : 080"  # scripted group (container) (typed FeaturePython)
  n = 11
  ref = H_element
FEATURE [App::DocumentObjectGroupPython] C_element143  label="C_element : 088"  # scripted group (container) (typed FeaturePython)
  n = 10
  ref = C_element
FEATURE [App::DocumentObjectGroupPython] N_element063  label="N_element : 035"  # scripted group (container) (typed FeaturePython)
  n = 2
  ref = N_element
FEATURE [App::DocumentObjectGroupPython] O_element124  label="O_element : 077"  # scripted group (container) (typed FeaturePython)
  n = 6
  ref = O_element
FEATURE [App::DocumentObjectGroupPython] G4_DNA_METHYLURIDINE  # scripted group (container) (typed FeaturePython)
  Dunit = g/cm3
  Dvalue = 1
  Group = -> [H_element133,C_element143,N_element063,O_element124]
  conduct = 2
  density = 1
  expand = 3
  formula = G4_DNA_METHYLURIDINE
  name = G4_DNA_METHYLURIDINE
  specific = 4
FEATURE [App::DocumentObjectGroupPython] P_element014  label="P_element : 003"  # scripted group (container) (typed FeaturePython)
  n = 1
  ref = P_element
FEATURE [App::DocumentObjectGroupPython] O_element125  label="O_element : 078"  # scripted group (container) (typed FeaturePython)
  n = 3
  ref = O_element
FEATURE [App::DocumentObjectGroupPython] G4_DNA_MONOPHOSPHATE  # scripted group (container) (typed FeaturePython)
  Dunit = g/cm3
  Dvalue = 1
  Group = -> [P_element014,O_element125]
  conduct = 2
  density = 1
  expand = 3
  formula = G4_DNA_MONOPHOSPHATE
  name = G4_DNA_MONOPHOSPHATE
  specific = 4
FEATURE [App::DocumentObjectGroupPython] H_element134  label="H_element : 081"  # scripted group (container) (typed FeaturePython)
  n = 10
  ref = H_element
FEATURE [App::DocumentObjectGroupPython] C_element144  label="C_element : 089"  # scripted group (container) (typed FeaturePython)
  n = 10
  ref = C_element
FEATURE [App::DocumentObjectGroupPython] N_element064  label="N_element : 036"  # scripted group (container) (typed FeaturePython)
  n = 5
  ref = N_element
FEATURE [App::DocumentObjectGroupPython] O_element126  label="O_element : 079"  # scripted group (container) (typed FeaturePython)
  n = 7
  ref = O_element
FEATURE [App::DocumentObjectGroupPython] P_element015  label="P_element : 004"  # scripted group (container) (typed FeaturePython)
  n = 1
  ref = P_element
FEATURE [App::DocumentObjectGroupPython] G4_DNA_A  # scripted group (container) (typed FeaturePython)
  Dunit = g/cm3
  Dvalue = 1
  Group = -> [H_element134,C_element144,N_element064,O_element126,P_element015]
  conduct = 2
  density = 1
  expand = 3
  formula = G4_DNA_A
  name = G4_DNA_A
  specific = 4
FEATURE [App::DocumentObjectGroupPython] H_element135  label="H_element : 082"  # scripted group (container) (typed FeaturePython)
  n = 10
  ref = H_element
FEATURE [App::DocumentObjectGroupPython] C_element145  label="C_element : 090"  # scripted group (container) (typed FeaturePython)
  n = 10
  ref = C_element
FEATURE [App::DocumentObjectGroupPython] N_element065  label="N_element : 037"  # scripted group (container) (typed FeaturePython)
  n = 5
  ref = N_element
FEATURE [App::DocumentObjectGroupPython] O_element127  label="O_element : 8"  # scripted group (container) (typed FeaturePython)
  n = 8
  ref = O_element
FEATURE [App::DocumentObjectGroupPython] P_element016  label="P_element : 005"  # scripted group (container) (typed FeaturePython)
  n = 1
  ref = P_element
FEATURE [App::DocumentObjectGroupPython] G4_DNA_G  # scripted group (container) (typed FeaturePython)
  Dunit = g/cm3
  Dvalue = 1
  Group = -> [H_element135,C_element145,N_element065,O_element127,P_element016]
  conduct = 2
  density = 1
  expand = 3
  formula = G4_DNA_G
  name = G4_DNA_G
  specific = 4
FEATURE [App::DocumentObjectGroupPython] H_element136  label="H_element : 083"  # scripted group (container) (typed FeaturePython)
  n = 10
  ref = H_element
FEATURE [App::DocumentObjectGroupPython] C_element146  label="C_element : 091"  # scripted group (container) (typed FeaturePython)
  n = 9
  ref = C_element
FEATURE [App::DocumentObjectGroupPython] N_element066  label="N_element : 038"  # scripted group (container) (typed FeaturePython)
  n = 3
  ref = N_element
FEATURE [App::DocumentObjectGroupPython] O_element128  label="O_element : 080"  # scripted group (container) (typed FeaturePython)
  n = 8
  ref = O_element
FEATURE [App::DocumentObjectGroupPython] P_element017  label="P_element : 006"  # scripted group (container) (typed FeaturePython)
  n = 1
  ref = P_element
FEATURE [App::DocumentObjectGroupPython] G4_DNA_C  # scripted group (container) (typed FeaturePython)
  Dunit = g/cm3
  Dvalue = 1
  Group = -> [H_element136,C_element146,N_element066,O_element128,P_element017]
  conduct = 2
  density = 1
  expand = 3
  formula = G4_DNA_C
  name = G4_DNA_C
  specific = 4
FEATURE [App::DocumentObjectGroupPython] H_element137  label="H_element : 084"  # scripted group (container) (typed FeaturePython)
  n = 9
  ref = H_element
FEATURE [App::DocumentObjectGroupPython] C_element147  label="C_element : 092"  # scripted group (container) (typed FeaturePython)
  n = 9
  ref = C_element
FEATURE [App::DocumentObjectGroupPython] N_element067  label="N_element : 039"  # scripted group (container) (typed FeaturePython)
  n = 2
  ref = N_element
FEATURE [App::DocumentObjectGroupPython] O_element129  label="O_element : 9"  # scripted group (container) (typed FeaturePython)
  n = 9
  ref = O_element
FEATURE [App::DocumentObjectGroupPython] P_element018  label="P_element : 007"  # scripted group (container) (typed FeaturePython)
  n = 1
  ref = P_element
FEATURE [App::DocumentObjectGroupPython] G4_DNA_U  # scripted group (container) (typed FeaturePython)
  Dunit = g/cm3
  Dvalue = 1
  Group = -> [H_element137,C_element147,N_element067,O_element129,P_element018]
  conduct = 2
  density = 1
  expand = 3
  formula = G4_DNA_U
  name = G4_DNA_U
  specific = 4
FEATURE [App::DocumentObjectGroupPython] H_element138  label="H_element : 085"  # scripted group (container) (typed FeaturePython)
  n = 11
  ref = H_element
FEATURE [App::DocumentObjectGroupPython] C_element148  label="C_element : 093"  # scripted group (container) (typed FeaturePython)
  n = 10
  ref = C_element
FEATURE [App::DocumentObjectGroupPython] N_element068  label="N_element : 040"  # scripted group (container) (typed FeaturePython)
  n = 2
  ref = N_element
FEATURE [App::DocumentObjectGroupPython] O_element130  label="O_element : 081"  # scripted group (container) (typed FeaturePython)
  n = 9
  ref = O_element
FEATURE [App::DocumentObjectGroupPython] P_element019  label="P_element : 008"  # scripted group (container) (typed FeaturePython)
  n = 1
  ref = P_element
FEATURE [App::DocumentObjectGroupPython] G4_DNA_MU  # scripted group (container) (typed FeaturePython)
  Dunit = g/cm3
  Dvalue = 1
  Group = -> [H_element138,C_element148,N_element068,O_element130,P_element019]
  conduct = 2
  density = 1
  expand = 3
  formula = G4_DNA_MU
  name = G4_DNA_MU
  specific = 4
FEATURE [App::DocumentObjectGroupPython] BioChemical  # scripted group (container) (typed FeaturePython)
  Group = -> [G4_CYTOSINE,G4_THYMINE,G4_URACIL,G4_DNA_ADENINE,G4_DNA_GUANINE,G4_DNA_CYTOSINE,G4_DNA_THYMINE,G4_DNA_URACIL,G4_DNA_ADENOSINE,G4_DNA_GUANOSINE,G4_DNA_CYTIDINE,G4_DNA_URIDINE,G4_DNA_METHYLURIDINE,G4_DNA_MONOPHOSPHATE,G4_DNA_A,G4_DNA_G,G4_DNA_C,G4_DNA_U,G4_DNA_MU]
FEATURE [App::DocumentObjectGroupPython] G4Materials  # scripted group (container) (typed FeaturePython)
  Group = -> [NIST,Element,HEP,Space,BioChemical]
  version = 1
FEATURE [App::DocumentObjectGroupPython] Geant4  # scripted group (container) (typed FeaturePython)
  Group = -> [G4Isotopes,G4Elements,G4Materials]
FEATURE [App::DocumentObjectGroupPython] Materials  # scripted group (container) (typed FeaturePython)
  Group = -> [Geant4]
FEATURE [Part::FeaturePython] GDMLBox_WorldBox  # WARN: FeaturePython — macro-defined, semantics opaque (R4)
  lunit = 2
  material = 5
  x = 273
  y = 273
  z = 130
FEATURE [Part::FeaturePython] GDMLBox_Box  # WARN: FeaturePython — macro-defined, semantics opaque (R4)
  lunit = 2
  material = 0
  x = 10
  y = 10
  z = 10
FEATURE [App::Part] LV_Box
  Group = -> [GDMLBox_Box]
  Origin = -> Origin002
  Placement = pos=(20,0,0) rot=(0,0,1;0rad)
FEATURE [Part::FeaturePython] Array  # Draft array (typed FeaturePython)
  AlwaysSyncPlacement = false
  Angle = 180
  ArrayType = 1
  Axis = (0,0,1)
  Base = -> LV_Box
  Center = (0,0,0)
  Count = 5
  ExpandArray = false
  Fuse = false
  IntervalAxis = (0,0,0)
  IntervalX = (100,0,0)
  IntervalY = (0,100,0)
  IntervalZ = (0,0,100)
  NumberCircles = 3
  NumberPolar = 5
  NumberX = 2
  NumberY = 2
  NumberZ = 1
  PlacementList = 5 placements: [(20,0,0),(14.1421,14.1421,0),(3.55271e-15,20,0),(-14.1421,14.1421,0),(-20,2.44929e-15,0)]
  RadialDistance = 50
  ScaleList = (5) [(1,1,1),(1,1,1),(1,1,1),(1,1,1),(1,1,1)]
  Symmetry = 1
  TangentialDistance = 25
FEATURE [App::Part] Part  label="experiment"
  Group = -> [LV_Box,Array]
  Origin = -> Origin001
FEATURE [App::Part] worldVOL
  Group = -> [GDMLBox_WorldBox,Part]
  Origin = -> Origin
